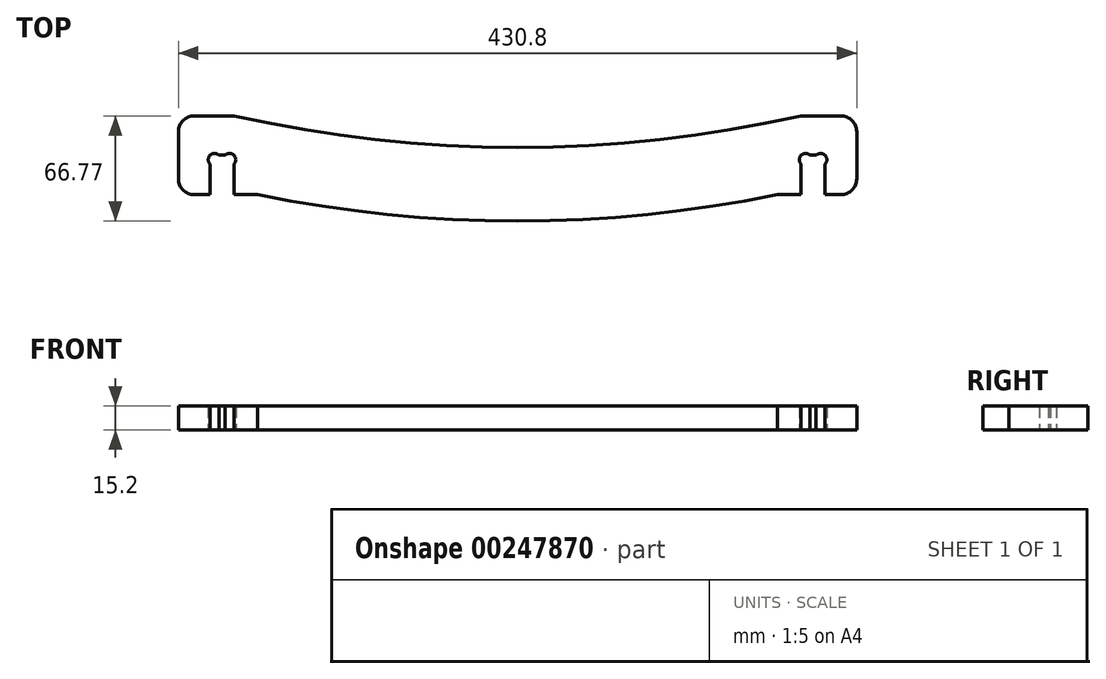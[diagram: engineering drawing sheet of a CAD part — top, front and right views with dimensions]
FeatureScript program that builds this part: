
annotation { "Feature Type Name" : "Feature", "Feature Type Description" : "" }
export const myFeature = defineFeature(function(context is Context, id is Id, definition is map)
    precondition{}
    {
        {
            var Q0;
            Q0=qCreatedBy(makeId("Top.planeOp"),FACE);
            var sketch = newSketch(context, id + "F0", { "sketchPlane" : qUnion([Q0])});
            skLineSegment(sketch, "E0", {"start": v(-2580, 2029) * mm, "end": v(-1360, 2029) * mm});
            skLineSegment(sketch, "E1", {"start": v(-1360, 2029) * mm, "end": v(-1360, -411) * mm});
            skLineSegment(sketch, "E2", {"start": v(-1360, -411) * mm, "end": v(-2580, -411) * mm});
            skLineSegment(sketch, "E3", {"start": v(-2580, -411) * mm, "end": v(-2580, 2029) * mm});
            skLineSegment(sketch, "E4", {"start": v(-2560, 2009) * mm, "end": v(-1380, 2009) * mm});
            skLineSegment(sketch, "E5", {"start": v(-1380, 2009) * mm, "end": v(-1380, -391) * mm});
            skLineSegment(sketch, "E6", {"start": v(-1380, -391) * mm, "end": v(-2560, -391) * mm});
            skLineSegment(sketch, "E7", {"start": v(-2560, -391) * mm, "end": v(-2560, 2009) * mm});
            skLineSegment(sketch, "E8", {"start": v(-1720.35, -206.09) * mm, "end": v(-1725.36, -224.77) * mm});
            skArc(sketch, "E9", {"start": v(-1725.36, -224.77) * mm, "mid": v(-1726.83, -230.23) * mm, "end": v(-1732.29, -228.77) * mm});
            skLineSegment(sketch, "E10", {"start": v(-1732.29, -228.77) * mm, "end": v(-1736.04, -227.76) * mm});
            skArc(sketch, "E11", {"start": v(-1736.04, -227.76) * mm, "mid": v(-1741.5, -226.3) * mm, "end": v(-1740.04, -220.84) * mm});
            skLineSegment(sketch, "E12", {"start": v(-1740.04, -220.84) * mm, "end": v(-1735.04, -202.15) * mm});
            skLineSegment(sketch, "E13", {"start": v(-1735.04, -202.15) * mm, "end": v(-1754.16, -197.03) * mm});
            skLineSegment(sketch, "E14", {"start": v(-1754.16, -197.03) * mm, "end": v(-1759.17, -215.71) * mm});
            skArc(sketch, "E15", {"start": v(-1759.17, -215.71) * mm, "mid": v(-1760.63, -221.18) * mm, "end": v(-1766.1, -219.71) * mm});
            skLineSegment(sketch, "E16", {"start": v(-1766.1, -219.71) * mm, "end": v(-1769.85, -218.7) * mm});
            skArc(sketch, "E17", {"start": v(-1769.85, -218.7) * mm, "mid": v(-1775.31, -217.24) * mm, "end": v(-1773.85, -211.78) * mm});
            skLineSegment(sketch, "E18", {"start": v(-1773.85, -211.78) * mm, "end": v(-1768.84, -193.1) * mm});
            skLineSegment(sketch, "E19", {"start": v(-1768.84, -193.1) * mm, "end": v(-1787.97, -187.97) * mm});
            skLineSegment(sketch, "E20", {"start": v(-1787.97, -187.97) * mm, "end": v(-1792.98, -206.65) * mm});
            skArc(sketch, "E21", {"start": v(-1792.98, -206.65) * mm, "mid": v(-1794.44, -212.12) * mm, "end": v(-1799.9, -210.65) * mm});
            skLineSegment(sketch, "E22", {"start": v(-1799.9, -210.65) * mm, "end": v(-1803.66, -209.65) * mm});
            skArc(sketch, "E23", {"start": v(-1803.66, -209.65) * mm, "mid": v(-1809.12, -208.18) * mm, "end": v(-1807.66, -202.72) * mm});
            skLineSegment(sketch, "E24", {"start": v(-1807.66, -202.72) * mm, "end": v(-1802.65, -184.03) * mm});
            skLineSegment(sketch, "E25", {"start": v(-1802.65, -184.03) * mm, "end": v(-1821.78, -178.9) * mm});
            skLineSegment(sketch, "E26", {"start": v(-1821.78, -178.9) * mm, "end": v(-1826.78, -197.6) * mm});
            skArc(sketch, "E27", {"start": v(-1826.78, -197.6) * mm, "mid": v(-1828.25, -203.06) * mm, "end": v(-1833.71, -201.6) * mm});
            skLineSegment(sketch, "E28", {"start": v(-1833.71, -201.6) * mm, "end": v(-1837.47, -200.59) * mm});
            skArc(sketch, "E29", {"start": v(-1837.47, -200.59) * mm, "mid": v(-1842.93, -199.12) * mm, "end": v(-1841.47, -193.66) * mm});
            skLineSegment(sketch, "E30", {"start": v(-1841.47, -193.66) * mm, "end": v(-1836.46, -174.98) * mm});
            skLineSegment(sketch, "E31", {"start": v(-1836.46, -174.98) * mm, "end": v(-1855.58, -169.85) * mm});
            skLineSegment(sketch, "E32", {"start": v(-1855.58, -169.85) * mm, "end": v(-1860.6, -188.54) * mm});
            skArc(sketch, "E33", {"start": v(-1860.6, -188.54) * mm, "mid": v(-1862.05, -194) * mm, "end": v(-1867.52, -192.53) * mm});
            skLineSegment(sketch, "E34", {"start": v(-1867.52, -192.54) * mm, "end": v(-1871.27, -191.53) * mm});
            skArc(sketch, "E35", {"start": v(-1871.27, -191.53) * mm, "mid": v(-1876.74, -190.07) * mm, "end": v(-1875.27, -184.6) * mm});
            skLineSegment(sketch, "E36", {"start": v(-1875.27, -184.6) * mm, "end": v(-1870.27, -165.92) * mm});
            skLineSegment(sketch, "E37", {"start": v(-1870.27, -165.92) * mm, "end": v(-1891.6, -160.2) * mm});
            skArc(sketch, "E38", {"start": v(-1891.6, -160.2) * mm, "mid": v(-1902.18, -158.55) * mm, "end": v(-1912.87, -159.2) * mm});
            skLineSegment(sketch, "E39", {"start": v(-1912.87, -159.2) * mm, "end": v(-2017.76, -176.28) * mm});
            skArc(sketch, "E40", {"start": v(-2017.76, -176.28) * mm, "mid": v(-2042.3, -169.28) * mm, "end": v(-2052.57, -145.92) * mm});
            skLineSegment(sketch, "E41", {"start": v(-2052.57, -145.92) * mm, "end": v(-2051.8, -115.24) * mm});
            skLineSegment(sketch, "E42", {"start": v(-2051.8, -115.24) * mm, "end": v(-2071.14, -114.76) * mm});
            skArc(sketch, "E43", {"start": v(-2071.14, -114.76) * mm, "mid": v(-2076.8, -114.62) * mm, "end": v(-2076.66, -108.97) * mm});
            skLineSegment(sketch, "E44", {"start": v(-2076.66, -108.97) * mm, "end": v(-2076.56, -105.08) * mm});
            skArc(sketch, "E45", {"start": v(-2076.56, -105.08) * mm, "mid": v(-2076.42, -99.43) * mm, "end": v(-2070.77, -99.57) * mm});
            skLineSegment(sketch, "E46", {"start": v(-2070.77, -99.57) * mm, "end": v(-2051.43, -100.05) * mm});
            skLineSegment(sketch, "E47", {"start": v(-2051.43, -100.05) * mm, "end": v(-2050.93, -80.25) * mm});
            skLineSegment(sketch, "E48", {"start": v(-2050.93, -80.25) * mm, "end": v(-2070.27, -79.77) * mm});
            skArc(sketch, "E49", {"start": v(-2070.27, -79.77) * mm, "mid": v(-2075.93, -79.63) * mm, "end": v(-2075.79, -73.98) * mm});
            skLineSegment(sketch, "E50", {"start": v(-2075.79, -73.98) * mm, "end": v(-2075.69, -70.1) * mm});
            skArc(sketch, "E51", {"start": v(-2075.69, -70.1) * mm, "mid": v(-2075.55, -64.44) * mm, "end": v(-2069.9, -64.58) * mm});
            skLineSegment(sketch, "E52", {"start": v(-2069.9, -64.58) * mm, "end": v(-2050.56, -65.06) * mm});
            skLineSegment(sketch, "E53", {"start": v(-2050.56, -65.06) * mm, "end": v(-2050.06, -45.27) * mm});
            skLineSegment(sketch, "E54", {"start": v(-2050.06, -45.27) * mm, "end": v(-2069.4, -44.78) * mm});
            skArc(sketch, "E55", {"start": v(-2069.4, -44.78) * mm, "mid": v(-2075.05, -44.64) * mm, "end": v(-2074.91, -38.99) * mm});
            skLineSegment(sketch, "E56", {"start": v(-2074.91, -38.99) * mm, "end": v(-2074.82, -35.1) * mm});
            skArc(sketch, "E57", {"start": v(-2074.82, -35.1) * mm, "mid": v(-2074.68, -29.45) * mm, "end": v(-2069.02, -29.59) * mm});
            skLineSegment(sketch, "E58", {"start": v(-2069.02, -29.59) * mm, "end": v(-2049.68, -30.07) * mm});
            skLineSegment(sketch, "E59", {"start": v(-2049.68, -30.07) * mm, "end": v(-2049.2, -10.28) * mm});
            skLineSegment(sketch, "E60", {"start": v(-2049.2, -10.28) * mm, "end": v(-2068.53, -9.8) * mm});
            skArc(sketch, "E61", {"start": v(-2068.53, -9.8) * mm, "mid": v(-2074.18, -9.65) * mm, "end": v(-2074.04, -4) * mm});
            skLineSegment(sketch, "E62", {"start": v(-2074.04, -4) * mm, "end": v(-2073.94, -0.11) * mm});
            skArc(sketch, "E63", {"start": v(-2073.94, -0.11) * mm, "mid": v(-2073.8, 5.54) * mm, "end": v(-2068.15, 5.4) * mm});
            skLineSegment(sketch, "E64", {"start": v(-2068.15, 5.4) * mm, "end": v(-2048.81, 4.92) * mm});
            skLineSegment(sketch, "E65", {"start": v(-2048.81, 4.92) * mm, "end": v(-2048.32, 24.71) * mm});
            skLineSegment(sketch, "E66", {"start": v(-2048.32, 24.71) * mm, "end": v(-2067.66, 25.2) * mm});
            skArc(sketch, "E67", {"start": v(-2067.66, 25.2) * mm, "mid": v(-2073.31, 25.34) * mm, "end": v(-2073.17, 31) * mm});
            skLineSegment(sketch, "E68", {"start": v(-2073.17, 31) * mm, "end": v(-2073.07, 34.88) * mm});
            skArc(sketch, "E69", {"start": v(-2073.07, 34.88) * mm, "mid": v(-2072.93, 40.53) * mm, "end": v(-2067.28, 40.4) * mm});
            skLineSegment(sketch, "E70", {"start": v(-2067.28, 40.4) * mm, "end": v(-2047.94, 39.9) * mm});
            skLineSegment(sketch, "E71", {"start": v(-2047.94, 39.9) * mm, "end": v(-2047.45, 59.7) * mm});
            skLineSegment(sketch, "E72", {"start": v(-2047.45, 59.7) * mm, "end": v(-2066.78, 60.18) * mm});
            skArc(sketch, "E73", {"start": v(-2066.78, 60.18) * mm, "mid": v(-2072.44, 60.33) * mm, "end": v(-2072.3, 65.98) * mm});
            skLineSegment(sketch, "E74", {"start": v(-2072.3, 65.98) * mm, "end": v(-2072.2, 69.87) * mm});
            skArc(sketch, "E75", {"start": v(-2072.2, 69.87) * mm, "mid": v(-2072.06, 75.52) * mm, "end": v(-2066.4, 75.38) * mm});
            skLineSegment(sketch, "E76", {"start": v(-2066.4, 75.38) * mm, "end": v(-2047.07, 74.9) * mm});
            skLineSegment(sketch, "E77", {"start": v(-2047.07, 74.9) * mm, "end": v(-2046.57, 94.7) * mm});
            skLineSegment(sketch, "E78", {"start": v(-2046.57, 94.7) * mm, "end": v(-2065.91, 95.17) * mm});
            skArc(sketch, "E79", {"start": v(-2065.91, 95.17) * mm, "mid": v(-2071.57, 95.31) * mm, "end": v(-2071.42, 100.97) * mm});
            skLineSegment(sketch, "E80", {"start": v(-2071.42, 100.97) * mm, "end": v(-2071.33, 104.85) * mm});
            skArc(sketch, "E81", {"start": v(-2071.33, 104.85) * mm, "mid": v(-2071.19, 110.5) * mm, "end": v(-2065.53, 110.37) * mm});
            skLineSegment(sketch, "E82", {"start": v(-2065.53, 110.37) * mm, "end": v(-2046.2, 109.89) * mm});
            skLineSegment(sketch, "E83", {"start": v(-2046.2, 109.89) * mm, "end": v(-2045.7, 129.68) * mm});
            skLineSegment(sketch, "E84", {"start": v(-2045.7, 129.68) * mm, "end": v(-2065.04, 130.16) * mm});
            skArc(sketch, "E85", {"start": v(-2065.04, 130.16) * mm, "mid": v(-2070.7, 130.3) * mm, "end": v(-2070.55, 135.96) * mm});
            skLineSegment(sketch, "E86", {"start": v(-2070.55, 135.96) * mm, "end": v(-2070.46, 139.84) * mm});
            skArc(sketch, "E87", {"start": v(-2070.46, 139.84) * mm, "mid": v(-2070.31, 145.5) * mm, "end": v(-2064.66, 145.36) * mm});
            skLineSegment(sketch, "E88", {"start": v(-2064.66, 145.36) * mm, "end": v(-2045.32, 144.88) * mm});
            skLineSegment(sketch, "E89", {"start": v(-2045.32, 144.88) * mm, "end": v(-2044.83, 164.67) * mm});
            skLineSegment(sketch, "E90", {"start": v(-2044.83, 164.67) * mm, "end": v(-2064.17, 165.15) * mm});
            skArc(sketch, "E91", {"start": v(-2064.17, 165.15) * mm, "mid": v(-2069.82, 165.3) * mm, "end": v(-2069.68, 170.95) * mm});
            skLineSegment(sketch, "E92", {"start": v(-2069.68, 170.95) * mm, "end": v(-2069.58, 174.83) * mm});
            skArc(sketch, "E93", {"start": v(-2069.58, 174.83) * mm, "mid": v(-2069.44, 180.49) * mm, "end": v(-2063.79, 180.35) * mm});
            skLineSegment(sketch, "E94", {"start": v(-2063.79, 180.35) * mm, "end": v(-2044.45, 179.86) * mm});
            skLineSegment(sketch, "E95", {"start": v(-2044.45, 179.86) * mm, "end": v(-2043.96, 199.66) * mm});
            skLineSegment(sketch, "E96", {"start": v(-2043.96, 199.66) * mm, "end": v(-2063.3, 200.14) * mm});
            skArc(sketch, "E97", {"start": v(-2063.3, 200.14) * mm, "mid": v(-2068.95, 200.28) * mm, "end": v(-2068.8, 205.94) * mm});
            skLineSegment(sketch, "E98", {"start": v(-2068.8, 205.94) * mm, "end": v(-2068.71, 209.82) * mm});
            skArc(sketch, "E99", {"start": v(-2068.71, 209.82) * mm, "mid": v(-2068.57, 215.48) * mm, "end": v(-2062.92, 215.34) * mm});
            skLineSegment(sketch, "E100", {"start": v(-2062.92, 215.34) * mm, "end": v(-2043.58, 214.85) * mm});
            skLineSegment(sketch, "E101", {"start": v(-2043.58, 214.85) * mm, "end": v(-2043.09, 234.63) * mm});
            skLineSegment(sketch, "E102", {"start": v(-2043.09, 234.63) * mm, "end": v(-2267.72, 254.88) * mm});
            skArc(sketch, "E103", {"start": v(-2267.72, 254.88) * mm, "mid": v(-2273.35, 255.39) * mm, "end": v(-2272.84, 261.02) * mm});
            skLineSegment(sketch, "E104", {"start": v(-2272.84, 261.02) * mm, "end": v(-2272.5, 264.9) * mm});
            skArc(sketch, "E105", {"start": v(-2272.5, 264.9) * mm, "mid": v(-2271.99, 270.53) * mm, "end": v(-2266.35, 270.02) * mm});
            skLineSegment(sketch, "E106", {"start": v(-2266.35, 270.02) * mm, "end": v(-2042.7, 249.86) * mm});
            skLineSegment(sketch, "E107", {"start": v(-2042.7, 249.86) * mm, "end": v(-2042.7, 249.96) * mm});
            skArc(sketch, "E108", {"start": v(-2042.7, 249.96) * mm, "mid": v(-2050.38, 270.53) * mm, "end": v(-2070, 280.37) * mm});
            skLineSegment(sketch, "E109", {"start": v(-2070, 280.37) * mm, "end": v(-2502.63, 319.37) * mm});
            skLineSegment(sketch, "E110", {"start": v(-2502.63, 319.37) * mm, "end": v(-2502.63, 256.1) * mm});
            skLineSegment(sketch, "E111", {"start": v(-2502.63, 256.1) * mm, "end": v(-2121.48, 221.73) * mm});
            skArc(sketch, "E112", {"start": v(-2121.48, 221.73) * mm, "mid": v(-2101.78, 211.82) * mm, "end": v(-2094.19, 191.1) * mm});
            skLineSegment(sketch, "E113", {"start": v(-2094.19, 191.1) * mm, "end": v(-2102.69, -150) * mm});
            skArc(sketch, "E114", {"start": v(-2102.69, -150) * mm, "mid": v(-2108.54, -167.07) * mm, "end": v(-2123.12, -177.7) * mm});
            skLineSegment(sketch, "E115", {"start": v(-2123.12, -177.7) * mm, "end": v(-2502.63, -299.61) * mm});
            skLineSegment(sketch, "E116", {"start": v(-2502.63, -299.61) * mm, "end": v(-2502.63, -349.61) * mm});
            skLineSegment(sketch, "E117", {"start": v(-2502.63, -349.61) * mm, "end": v(-2352.73, -314.3) * mm});
            skLineSegment(sketch, "E118", {"start": v(-2352.73, -314.3) * mm, "end": v(-2357.16, -295.47) * mm});
            skArc(sketch, "E119", {"start": v(-2357.16, -295.47) * mm, "mid": v(-2358.46, -289.97) * mm, "end": v(-2352.95, -288.67) * mm});
            skLineSegment(sketch, "E120", {"start": v(-2352.95, -288.67) * mm, "end": v(-2349.17, -287.78) * mm});
            skArc(sketch, "E121", {"start": v(-2349.17, -287.78) * mm, "mid": v(-2343.66, -286.48) * mm, "end": v(-2342.37, -291.99) * mm});
            skLineSegment(sketch, "E122", {"start": v(-2342.37, -291.99) * mm, "end": v(-2337.93, -310.81) * mm});
            skLineSegment(sketch, "E123", {"start": v(-2337.93, -310.81) * mm, "end": v(-1916.35, -211.5) * mm});
            skArc(sketch, "E124", {"start": v(-1916.35, -211.5) * mm, "mid": v(-1904.12, -210.17) * mm, "end": v(-1891.94, -211.87) * mm});
            skLineSegment(sketch, "E125", {"start": v(-1891.94, -211.87) * mm, "end": v(-1685.1, -267.3) * mm});
            skArc(sketch, "E126", {"start": v(-1685.1, -267.3) * mm, "mid": v(-1677.5, -266.3) * mm, "end": v(-1672.85, -260.23) * mm});
            skLineSegment(sketch, "E127", {"start": v(-1672.85, -260.23) * mm, "end": v(-1665.08, -231.25) * mm});
            skArc(sketch, "E128", {"start": v(-1665.08, -231.25) * mm, "mid": v(-1666.08, -223.66) * mm, "end": v(-1672.16, -219) * mm});
            skLineSegment(sketch, "E129", {"start": v(-1672.16, -219) * mm, "end": v(-1686.55, -215.14) * mm});
            skLineSegment(sketch, "E130", {"start": v(-1686.55, -215.14) * mm, "end": v(-1691.55, -233.83) * mm});
            skArc(sketch, "E131", {"start": v(-1691.55, -233.83) * mm, "mid": v(-1693.02, -239.3) * mm, "end": v(-1698.48, -237.83) * mm});
            skLineSegment(sketch, "E132", {"start": v(-1698.48, -237.83) * mm, "end": v(-1702.24, -236.82) * mm});
            skArc(sketch, "E133", {"start": v(-1702.24, -236.82) * mm, "mid": v(-1707.7, -235.36) * mm, "end": v(-1706.24, -229.9) * mm});
            skLineSegment(sketch, "E134", {"start": v(-1706.24, -229.9) * mm, "end": v(-1701.23, -211.21) * mm});
            skLineSegment(sketch, "E135", {"start": v(-1701.23, -211.21) * mm, "end": v(-1720.26, -206.11) * mm});
            skArc(sketch, "E136", {"start": v(-1681.43, -338.92) * mm, "mid": v(-1675.77, -338.92) * mm, "end": v(-1675.77, -344.58) * mm});
            skLineSegment(sketch, "E137", {"start": v(-1675.77, -344.58) * mm, "end": v(-1675.77, -348.47) * mm});
            skArc(sketch, "E138", {"start": v(-1675.77, -348.47) * mm, "mid": v(-1675.77, -354.12) * mm, "end": v(-1681.43, -354.12) * mm});
            skLineSegment(sketch, "E139", {"start": v(-1681.43, -354.12) * mm, "end": v(-1905.99, -354.12) * mm});
            skLineSegment(sketch, "E140", {"start": v(-1905.99, -354.12) * mm, "end": v(-1905.99, -374.22) * mm});
            skLineSegment(sketch, "E141", {"start": v(-1905.99, -374.22) * mm, "end": v(-1455.55, -374.22) * mm});
            skArc(sketch, "E142", {"start": v(-1455.55, -374.22) * mm, "mid": v(-1448.48, -371.3) * mm, "end": v(-1445.55, -364.22) * mm});
            skLineSegment(sketch, "E143", {"start": v(-1445.55, -364.22) * mm, "end": v(-1445.55, -338.79) * mm});
            skArc(sketch, "E144", {"start": v(-1445.55, -338.79) * mm, "mid": v(-1465.55, -158.82) * mm, "end": v(-1445.55, 21.14) * mm});
            skLineSegment(sketch, "E145", {"start": v(-1445.55, 21.14) * mm, "end": v(-1445.55, 46.58) * mm});
            skArc(sketch, "E146", {"start": v(-1445.55, 46.58) * mm, "mid": v(-1448.48, 53.65) * mm, "end": v(-1455.55, 56.58) * mm});
            skLineSegment(sketch, "E147", {"start": v(-1455.55, 56.58) * mm, "end": v(-1905.99, 56.58) * mm});
            skLineSegment(sketch, "E148", {"start": v(-1905.99, 56.58) * mm, "end": v(-1905.99, 36.48) * mm});
            skLineSegment(sketch, "E149", {"start": v(-1905.99, 36.48) * mm, "end": v(-1681.43, 36.48) * mm});
            skArc(sketch, "E150", {"start": v(-1681.43, 36.48) * mm, "mid": v(-1675.77, 36.48) * mm, "end": v(-1675.77, 30.82) * mm});
            skLineSegment(sketch, "E151", {"start": v(-1675.77, 30.82) * mm, "end": v(-1675.77, 26.93) * mm});
            skArc(sketch, "E152", {"start": v(-1675.77, 26.93) * mm, "mid": v(-1675.77, 21.28) * mm, "end": v(-1681.43, 21.28) * mm});
            skLineSegment(sketch, "E153", {"start": v(-1681.43, 21.28) * mm, "end": v(-1905.99, 21.28) * mm});
            skLineSegment(sketch, "E154", {"start": v(-1905.99, 21.28) * mm, "end": v(-1905.99, 1.18) * mm});
            skLineSegment(sketch, "E155", {"start": v(-1905.99, 1.18) * mm, "end": v(-1508.65, 1.18) * mm});
            skArc(sketch, "E156", {"start": v(-1508.65, 1.18) * mm, "mid": v(-1500.97, -2.42) * mm, "end": v(-1498.82, -10.63) * mm});
            skArc(sketch, "E157", {"start": v(-1498.82, -10.63) * mm, "mid": v(-1512.32, -158.82) * mm, "end": v(-1498.82, -307.01) * mm});
            skArc(sketch, "E158", {"start": v(-1498.82, -307.01) * mm, "mid": v(-1500.97, -315.22) * mm, "end": v(-1508.65, -318.82) * mm});
            skLineSegment(sketch, "E159", {"start": v(-1508.65, -318.82) * mm, "end": v(-1905.99, -318.82) * mm});
            skLineSegment(sketch, "E160", {"start": v(-1905.99, -318.82) * mm, "end": v(-1905.99, -338.92) * mm});
            skLineSegment(sketch, "E161", {"start": v(-1905.99, -338.92) * mm, "end": v(-1681.43, -338.92) * mm});
            skArc(sketch, "E162", {"start": v(-1935.54, -36.1) * mm, "mid": v(-1929.88, -36.1) * mm, "end": v(-1929.88, -41.77) * mm});
            skLineSegment(sketch, "E163", {"start": v(-1929.88, -41.77) * mm, "end": v(-1929.88, -61.1) * mm});
            skLineSegment(sketch, "E164", {"start": v(-1929.88, -61.1) * mm, "end": v(-1554.68, -61.1) * mm});
            skLineSegment(sketch, "E165", {"start": v(-1554.68, -61.1) * mm, "end": v(-1554.68, -41.77) * mm});
            skArc(sketch, "E166", {"start": v(-1554.68, -41.77) * mm, "mid": v(-1554.68, -36.1) * mm, "end": v(-1549.03, -36.1) * mm});
            skLineSegment(sketch, "E167", {"start": v(-1549.03, -36.1) * mm, "end": v(-1545.14, -36.1) * mm});
            skArc(sketch, "E168", {"start": v(-1545.14, -36.1) * mm, "mid": v(-1539.48, -36.1) * mm, "end": v(-1539.48, -41.77) * mm});
            skLineSegment(sketch, "E169", {"start": v(-1539.48, -41.77) * mm, "end": v(-1539.48, -61.1) * mm});
            skLineSegment(sketch, "E170", {"start": v(-1539.48, -61.1) * mm, "end": v(-1534.78, -61.1) * mm});
            skArc(sketch, "E171", {"start": v(-1534.78, -61.1) * mm, "mid": v(-1527.71, -58.18) * mm, "end": v(-1524.78, -51.1) * mm});
            skLineSegment(sketch, "E172", {"start": v(-1524.78, -51.1) * mm, "end": v(-1524.78, -21.1) * mm});
            skArc(sketch, "E173", {"start": v(-1524.78, -21.1) * mm, "mid": v(-1527.71, -14.04) * mm, "end": v(-1534.78, -11.1) * mm});
            skLineSegment(sketch, "E174", {"start": v(-1534.78, -11.1) * mm, "end": v(-1949.78, -11.1) * mm});
            skArc(sketch, "E175", {"start": v(-1949.78, -11.1) * mm, "mid": v(-1956.85, -14.04) * mm, "end": v(-1959.78, -21.1) * mm});
            skLineSegment(sketch, "E176", {"start": v(-1959.78, -21.1) * mm, "end": v(-1959.78, -51.1) * mm});
            skArc(sketch, "E177", {"start": v(-1959.78, -51.1) * mm, "mid": v(-1956.85, -58.18) * mm, "end": v(-1949.78, -61.1) * mm});
            skLineSegment(sketch, "E178", {"start": v(-1949.78, -61.1) * mm, "end": v(-1945.08, -61.1) * mm});
            skLineSegment(sketch, "E179", {"start": v(-1945.08, -61.1) * mm, "end": v(-1945.08, -41.77) * mm});
            skArc(sketch, "E180", {"start": v(-1945.08, -41.77) * mm, "mid": v(-1945.08, -36.1) * mm, "end": v(-1939.43, -36.1) * mm});
            skLineSegment(sketch, "E181", {"start": v(-1939.43, -36.1) * mm, "end": v(-1935.54, -36.1) * mm});
            skArc(sketch, "E182", {"start": v(-2222.39, -382.07) * mm, "mid": v(-2052.48, -319.46) * mm, "end": v(-1872.97, -295.7) * mm});
            skLineSegment(sketch, "E183", {"start": v(-1872.97, -295.7) * mm, "end": v(-1848.28, -289.59) * mm});
            skArc(sketch, "E184", {"start": v(-1848.28, -289.59) * mm, "mid": v(-1842.12, -285.05) * mm, "end": v(-1840.98, -277.48) * mm});
            skLineSegment(sketch, "E185", {"start": v(-1840.98, -277.48) * mm, "end": v(-1848.17, -248.36) * mm});
            skArc(sketch, "E186", {"start": v(-1848.17, -248.36) * mm, "mid": v(-1852.71, -242.2) * mm, "end": v(-1860.28, -241.06) * mm});
            skLineSegment(sketch, "E187", {"start": v(-1860.28, -241.06) * mm, "end": v(-1870.08, -243.48) * mm});
            skLineSegment(sketch, "E188", {"start": v(-1870.08, -243.48) * mm, "end": v(-1865.44, -262.26) * mm});
            skArc(sketch, "E189", {"start": v(-1865.44, -262.26) * mm, "mid": v(-1864.09, -267.75) * mm, "end": v(-1869.58, -269.1) * mm});
            skLineSegment(sketch, "E190", {"start": v(-1869.58, -269.1) * mm, "end": v(-1873.35, -270.04) * mm});
            skArc(sketch, "E191", {"start": v(-1873.35, -270.04) * mm, "mid": v(-1878.84, -271.4) * mm, "end": v(-1880.2, -265.9) * mm});
            skLineSegment(sketch, "E192", {"start": v(-1880.2, -265.9) * mm, "end": v(-1884.84, -247.13) * mm});
            skLineSegment(sketch, "E193", {"start": v(-1884.84, -247.13) * mm, "end": v(-1899.5, -250.75) * mm});
            skArc(sketch, "E194", {"start": v(-1899.5, -250.75) * mm, "mid": v(-2063.7, -274.06) * mm, "end": v(-2219.86, -329.94) * mm});
            skLineSegment(sketch, "E195", {"start": v(-2219.86, -329.94) * mm, "end": v(-2234.52, -333.57) * mm});
            skLineSegment(sketch, "E196", {"start": v(-2234.52, -333.57) * mm, "end": v(-2229.87, -352.34) * mm});
            skArc(sketch, "E197", {"start": v(-2229.87, -352.34) * mm, "mid": v(-2228.52, -357.84) * mm, "end": v(-2234, -359.2) * mm});
            skLineSegment(sketch, "E198", {"start": v(-2234, -359.2) * mm, "end": v(-2237.78, -360.13) * mm});
            skArc(sketch, "E199", {"start": v(-2237.78, -360.13) * mm, "mid": v(-2243.27, -361.48) * mm, "end": v(-2244.63, -356) * mm});
            skLineSegment(sketch, "E200", {"start": v(-2244.63, -356) * mm, "end": v(-2249.27, -337.21) * mm});
            skLineSegment(sketch, "E201", {"start": v(-2249.27, -337.21) * mm, "end": v(-2259.08, -339.64) * mm});
            skArc(sketch, "E202", {"start": v(-2259.08, -339.64) * mm, "mid": v(-2265.24, -344.18) * mm, "end": v(-2266.38, -351.74) * mm});
            skLineSegment(sketch, "E203", {"start": v(-2266.38, -351.74) * mm, "end": v(-2259.19, -380.86) * mm});
            skArc(sketch, "E204", {"start": v(-2259.19, -380.86) * mm, "mid": v(-2254.65, -387.02) * mm, "end": v(-2247.08, -388.17) * mm});
            skLineSegment(sketch, "E205", {"start": v(-2247.08, -388.17) * mm, "end": v(-2222.39, -382.07) * mm});
            skArc(sketch, "E206", {"start": v(-1385, 120.69) * mm, "mid": v(-1405, 300.65) * mm, "end": v(-1385, 480.62) * mm});
            skLineSegment(sketch, "E207", {"start": v(-1385, 480.62) * mm, "end": v(-1385, 506.05) * mm});
            skArc(sketch, "E208", {"start": v(-1385, 506.05) * mm, "mid": v(-1387.93, 513.12) * mm, "end": v(-1395, 516.05) * mm});
            skLineSegment(sketch, "E209", {"start": v(-1395, 516.05) * mm, "end": v(-1425, 516.05) * mm});
            skArc(sketch, "E210", {"start": v(-1425, 516.05) * mm, "mid": v(-1432.06, 513.12) * mm, "end": v(-1435, 506.05) * mm});
            skLineSegment(sketch, "E211", {"start": v(-1435, 506.05) * mm, "end": v(-1435, 495.95) * mm});
            skLineSegment(sketch, "E212", {"start": v(-1435, 495.95) * mm, "end": v(-1415.65, 495.95) * mm});
            skArc(sketch, "E213", {"start": v(-1415.65, 495.95) * mm, "mid": v(-1410, 495.95) * mm, "end": v(-1410, 490.3) * mm});
            skLineSegment(sketch, "E214", {"start": v(-1410, 490.3) * mm, "end": v(-1410, 486.41) * mm});
            skArc(sketch, "E215", {"start": v(-1410, 486.41) * mm, "mid": v(-1410, 480.75) * mm, "end": v(-1415.65, 480.75) * mm});
            skLineSegment(sketch, "E216", {"start": v(-1415.65, 480.75) * mm, "end": v(-1435, 480.75) * mm});
            skLineSegment(sketch, "E217", {"start": v(-1435, 480.75) * mm, "end": v(-1435, 465.65) * mm});
            skArc(sketch, "E218", {"start": v(-1435, 465.65) * mm, "mid": v(-1451.77, 300.65) * mm, "end": v(-1435, 135.65) * mm});
            skLineSegment(sketch, "E219", {"start": v(-1435, 135.65) * mm, "end": v(-1435, 120.55) * mm});
            skLineSegment(sketch, "E220", {"start": v(-1435, 120.55) * mm, "end": v(-1415.65, 120.55) * mm});
            skArc(sketch, "E221", {"start": v(-1415.65, 120.55) * mm, "mid": v(-1410, 120.55) * mm, "end": v(-1410, 114.9) * mm});
            skLineSegment(sketch, "E222", {"start": v(-1410, 114.9) * mm, "end": v(-1410, 111.01) * mm});
            skArc(sketch, "E223", {"start": v(-1410, 111.01) * mm, "mid": v(-1410, 105.35) * mm, "end": v(-1415.65, 105.35) * mm});
            skLineSegment(sketch, "E224", {"start": v(-1415.65, 105.35) * mm, "end": v(-1435, 105.35) * mm});
            skLineSegment(sketch, "E225", {"start": v(-1435, 105.35) * mm, "end": v(-1435, 95.25) * mm});
            skArc(sketch, "E226", {"start": v(-1435, 95.25) * mm, "mid": v(-1432.06, 88.18) * mm, "end": v(-1425, 85.25) * mm});
            skLineSegment(sketch, "E227", {"start": v(-1425, 85.25) * mm, "end": v(-1395, 85.25) * mm});
            skArc(sketch, "E228", {"start": v(-1395, 85.25) * mm, "mid": v(-1387.93, 88.18) * mm, "end": v(-1385, 95.25) * mm});
            skLineSegment(sketch, "E229", {"start": v(-1385, 95.25) * mm, "end": v(-1385, 120.69) * mm});
            skArc(sketch, "E230", {"start": v(-2159.63, -49.76) * mm, "mid": v(-2339.6, -69.76) * mm, "end": v(-2519.57, -49.76) * mm});
            skLineSegment(sketch, "E231", {"start": v(-2519.57, -49.76) * mm, "end": v(-2545, -49.76) * mm});
            skArc(sketch, "E232", {"start": v(-2545, -49.76) * mm, "mid": v(-2552.07, -52.7) * mm, "end": v(-2555, -59.76) * mm});
            skLineSegment(sketch, "E233", {"start": v(-2555, -59.76) * mm, "end": v(-2555, -89.75) * mm});
            skArc(sketch, "E234", {"start": v(-2555, -89.75) * mm, "mid": v(-2552.07, -96.83) * mm, "end": v(-2545, -99.75) * mm});
            skLineSegment(sketch, "E235", {"start": v(-2545, -99.75) * mm, "end": v(-2534.9, -99.75) * mm});
            skLineSegment(sketch, "E236", {"start": v(-2534.9, -99.75) * mm, "end": v(-2534.9, -80.41) * mm});
            skArc(sketch, "E237", {"start": v(-2534.9, -80.41) * mm, "mid": v(-2534.9, -74.75) * mm, "end": v(-2529.24, -74.75) * mm});
            skLineSegment(sketch, "E238", {"start": v(-2529.24, -74.75) * mm, "end": v(-2525.36, -74.75) * mm});
            skArc(sketch, "E239", {"start": v(-2525.36, -74.75) * mm, "mid": v(-2519.7, -74.75) * mm, "end": v(-2519.7, -80.41) * mm});
            skLineSegment(sketch, "E240", {"start": v(-2519.7, -80.41) * mm, "end": v(-2519.7, -99.75) * mm});
            skLineSegment(sketch, "E241", {"start": v(-2519.7, -99.75) * mm, "end": v(-2504.6, -99.75) * mm});
            skArc(sketch, "E242", {"start": v(-2504.6, -99.75) * mm, "mid": v(-2339.6, -116.53) * mm, "end": v(-2174.6, -99.75) * mm});
            skLineSegment(sketch, "E243", {"start": v(-2174.6, -99.75) * mm, "end": v(-2159.5, -99.75) * mm});
            skLineSegment(sketch, "E244", {"start": v(-2159.5, -99.75) * mm, "end": v(-2159.5, -80.41) * mm});
            skArc(sketch, "E245", {"start": v(-2159.5, -80.41) * mm, "mid": v(-2159.5, -74.75) * mm, "end": v(-2153.84, -74.75) * mm});
            skLineSegment(sketch, "E246", {"start": v(-2153.84, -74.75) * mm, "end": v(-2149.96, -74.75) * mm});
            skArc(sketch, "E247", {"start": v(-2149.96, -74.75) * mm, "mid": v(-2144.3, -74.75) * mm, "end": v(-2144.3, -80.41) * mm});
            skLineSegment(sketch, "E248", {"start": v(-2144.3, -80.41) * mm, "end": v(-2144.3, -99.75) * mm});
            skLineSegment(sketch, "E249", {"start": v(-2144.3, -99.75) * mm, "end": v(-2134.2, -99.75) * mm});
            skArc(sketch, "E250", {"start": v(-2134.2, -99.75) * mm, "mid": v(-2127.13, -96.83) * mm, "end": v(-2124.2, -89.75) * mm});
            skLineSegment(sketch, "E251", {"start": v(-2124.2, -89.75) * mm, "end": v(-2124.2, -59.76) * mm});
            skArc(sketch, "E252", {"start": v(-2124.2, -59.76) * mm, "mid": v(-2127.13, -52.7) * mm, "end": v(-2134.2, -49.76) * mm});
            skLineSegment(sketch, "E253", {"start": v(-2134.2, -49.76) * mm, "end": v(-2159.63, -49.76) * mm});
            skArc(sketch, "E254", {"start": v(-2159.63, -115.3) * mm, "mid": v(-2339.6, -135.3) * mm, "end": v(-2519.57, -115.3) * mm});
            skLineSegment(sketch, "E255", {"start": v(-2519.57, -115.3) * mm, "end": v(-2545, -115.3) * mm});
            skArc(sketch, "E256", {"start": v(-2545, -115.3) * mm, "mid": v(-2552.07, -118.22) * mm, "end": v(-2555, -125.3) * mm});
            skLineSegment(sketch, "E257", {"start": v(-2555, -125.3) * mm, "end": v(-2555, -155.29) * mm});
            skArc(sketch, "E258", {"start": v(-2555, -155.29) * mm, "mid": v(-2552.07, -162.36) * mm, "end": v(-2545, -165.29) * mm});
            skLineSegment(sketch, "E259", {"start": v(-2545, -165.29) * mm, "end": v(-2534.9, -165.29) * mm});
            skLineSegment(sketch, "E260", {"start": v(-2534.9, -165.29) * mm, "end": v(-2534.9, -145.94) * mm});
            skArc(sketch, "E261", {"start": v(-2534.9, -145.94) * mm, "mid": v(-2534.9, -140.29) * mm, "end": v(-2529.24, -140.29) * mm});
            skLineSegment(sketch, "E262", {"start": v(-2529.24, -140.29) * mm, "end": v(-2525.36, -140.29) * mm});
            skArc(sketch, "E263", {"start": v(-2525.36, -140.29) * mm, "mid": v(-2519.7, -140.29) * mm, "end": v(-2519.7, -145.94) * mm});
            skLineSegment(sketch, "E264", {"start": v(-2519.7, -145.94) * mm, "end": v(-2519.7, -165.29) * mm});
            skLineSegment(sketch, "E265", {"start": v(-2519.7, -165.29) * mm, "end": v(-2504.6, -165.29) * mm});
            skArc(sketch, "E266", {"start": v(-2504.6, -165.29) * mm, "mid": v(-2339.6, -182.06) * mm, "end": v(-2174.6, -165.29) * mm});
            skLineSegment(sketch, "E267", {"start": v(-2174.6, -165.29) * mm, "end": v(-2159.5, -165.29) * mm});
            skLineSegment(sketch, "E268", {"start": v(-2159.5, -165.29) * mm, "end": v(-2159.5, -145.94) * mm});
            skArc(sketch, "E269", {"start": v(-2159.5, -145.94) * mm, "mid": v(-2159.5, -140.29) * mm, "end": v(-2153.84, -140.29) * mm});
            skLineSegment(sketch, "E270", {"start": v(-2153.84, -140.29) * mm, "end": v(-2149.96, -140.29) * mm});
            skArc(sketch, "E271", {"start": v(-2149.96, -140.29) * mm, "mid": v(-2144.3, -140.29) * mm, "end": v(-2144.3, -145.94) * mm});
            skLineSegment(sketch, "E272", {"start": v(-2144.3, -145.94) * mm, "end": v(-2144.3, -165.29) * mm});
            skLineSegment(sketch, "E273", {"start": v(-2144.3, -165.29) * mm, "end": v(-2134.2, -165.29) * mm});
            skArc(sketch, "E274", {"start": v(-2134.2, -165.29) * mm, "mid": v(-2127.13, -162.36) * mm, "end": v(-2124.2, -155.29) * mm});
            skLineSegment(sketch, "E275", {"start": v(-2124.2, -155.29) * mm, "end": v(-2124.2, -125.3) * mm});
            skArc(sketch, "E276", {"start": v(-2124.2, -125.3) * mm, "mid": v(-2127.13, -118.22) * mm, "end": v(-2134.2, -115.3) * mm});
            skLineSegment(sketch, "E277", {"start": v(-2134.2, -115.3) * mm, "end": v(-2159.63, -115.3) * mm});
            skArc(sketch, "E278", {"start": v(-1866.53, 72.65) * mm, "mid": v(-1686.56, 92.65) * mm, "end": v(-1506.6, 72.65) * mm});
            skLineSegment(sketch, "E279", {"start": v(-1506.6, 72.65) * mm, "end": v(-1481.16, 72.65) * mm});
            skArc(sketch, "E280", {"start": v(-1481.16, 72.65) * mm, "mid": v(-1474.09, 75.58) * mm, "end": v(-1471.16, 82.65) * mm});
            skLineSegment(sketch, "E281", {"start": v(-1471.16, 82.65) * mm, "end": v(-1471.16, 112.65) * mm});
            skArc(sketch, "E282", {"start": v(-1471.16, 112.65) * mm, "mid": v(-1474.09, 119.72) * mm, "end": v(-1481.16, 122.65) * mm});
            skLineSegment(sketch, "E283", {"start": v(-1481.16, 122.65) * mm, "end": v(-1491.26, 122.65) * mm});
            skLineSegment(sketch, "E284", {"start": v(-1491.26, 122.65) * mm, "end": v(-1491.26, 103.3) * mm});
            skArc(sketch, "E285", {"start": v(-1491.26, 103.3) * mm, "mid": v(-1491.26, 97.65) * mm, "end": v(-1496.92, 97.65) * mm});
            skLineSegment(sketch, "E286", {"start": v(-1496.92, 97.65) * mm, "end": v(-1500.8, 97.65) * mm});
            skArc(sketch, "E287", {"start": v(-1500.8, 97.65) * mm, "mid": v(-1506.46, 97.65) * mm, "end": v(-1506.46, 103.3) * mm});
            skLineSegment(sketch, "E288", {"start": v(-1506.46, 103.3) * mm, "end": v(-1506.46, 122.65) * mm});
            skLineSegment(sketch, "E289", {"start": v(-1506.46, 122.65) * mm, "end": v(-1521.56, 122.65) * mm});
            skArc(sketch, "E290", {"start": v(-1521.56, 122.65) * mm, "mid": v(-1686.56, 139.42) * mm, "end": v(-1851.56, 122.65) * mm});
            skLineSegment(sketch, "E291", {"start": v(-1851.56, 122.65) * mm, "end": v(-1866.66, 122.65) * mm});
            skLineSegment(sketch, "E292", {"start": v(-1866.66, 122.65) * mm, "end": v(-1866.66, 103.3) * mm});
            skArc(sketch, "E293", {"start": v(-1866.66, 103.3) * mm, "mid": v(-1866.66, 97.65) * mm, "end": v(-1872.32, 97.65) * mm});
            skLineSegment(sketch, "E294", {"start": v(-1872.32, 97.65) * mm, "end": v(-1876.2, 97.65) * mm});
            skArc(sketch, "E295", {"start": v(-1876.2, 97.65) * mm, "mid": v(-1881.86, 97.65) * mm, "end": v(-1881.86, 103.3) * mm});
            skLineSegment(sketch, "E296", {"start": v(-1881.86, 103.3) * mm, "end": v(-1881.86, 122.65) * mm});
            skLineSegment(sketch, "E297", {"start": v(-1881.86, 122.65) * mm, "end": v(-1891.96, 122.65) * mm});
            skArc(sketch, "E298", {"start": v(-1891.96, 122.65) * mm, "mid": v(-1899.03, 119.72) * mm, "end": v(-1901.96, 112.65) * mm});
            skLineSegment(sketch, "E299", {"start": v(-1901.96, 112.65) * mm, "end": v(-1901.96, 82.65) * mm});
            skArc(sketch, "E300", {"start": v(-1901.96, 82.65) * mm, "mid": v(-1899.03, 75.58) * mm, "end": v(-1891.96, 72.65) * mm});
            skLineSegment(sketch, "E301", {"start": v(-1891.96, 72.65) * mm, "end": v(-1866.53, 72.65) * mm});
            skArc(sketch, "E302", {"start": v(-1866.53, 138.19) * mm, "mid": v(-1686.56, 158.19) * mm, "end": v(-1506.6, 138.19) * mm});
            skLineSegment(sketch, "E303", {"start": v(-1506.6, 138.19) * mm, "end": v(-1481.16, 138.19) * mm});
            skArc(sketch, "E304", {"start": v(-1481.16, 138.19) * mm, "mid": v(-1474.09, 141.11) * mm, "end": v(-1471.16, 148.19) * mm});
            skLineSegment(sketch, "E305", {"start": v(-1471.16, 148.19) * mm, "end": v(-1471.16, 178.18) * mm});
            skArc(sketch, "E306", {"start": v(-1471.16, 178.18) * mm, "mid": v(-1474.09, 185.25) * mm, "end": v(-1481.16, 188.18) * mm});
            skLineSegment(sketch, "E307", {"start": v(-1481.16, 188.18) * mm, "end": v(-1491.26, 188.18) * mm});
            skLineSegment(sketch, "E308", {"start": v(-1491.26, 188.18) * mm, "end": v(-1491.26, 168.83) * mm});
            skArc(sketch, "E309", {"start": v(-1491.26, 168.83) * mm, "mid": v(-1491.26, 163.18) * mm, "end": v(-1496.92, 163.18) * mm});
            skLineSegment(sketch, "E310", {"start": v(-1496.92, 163.18) * mm, "end": v(-1500.8, 163.18) * mm});
            skArc(sketch, "E311", {"start": v(-1500.8, 163.18) * mm, "mid": v(-1506.46, 163.18) * mm, "end": v(-1506.46, 168.83) * mm});
            skLineSegment(sketch, "E312", {"start": v(-1506.46, 168.83) * mm, "end": v(-1506.46, 188.18) * mm});
            skLineSegment(sketch, "E313", {"start": v(-1506.46, 188.18) * mm, "end": v(-1521.56, 188.18) * mm});
            skArc(sketch, "E314", {"start": v(-1521.56, 188.18) * mm, "mid": v(-1686.56, 204.96) * mm, "end": v(-1851.56, 188.18) * mm});
            skLineSegment(sketch, "E315", {"start": v(-1851.56, 188.18) * mm, "end": v(-1866.66, 188.18) * mm});
            skLineSegment(sketch, "E316", {"start": v(-1866.66, 188.18) * mm, "end": v(-1866.66, 168.83) * mm});
            skArc(sketch, "E317", {"start": v(-1866.66, 168.83) * mm, "mid": v(-1866.66, 163.18) * mm, "end": v(-1872.32, 163.18) * mm});
            skLineSegment(sketch, "E318", {"start": v(-1872.32, 163.18) * mm, "end": v(-1876.2, 163.18) * mm});
            skArc(sketch, "E319", {"start": v(-1876.2, 163.18) * mm, "mid": v(-1881.86, 163.18) * mm, "end": v(-1881.86, 168.83) * mm});
            skLineSegment(sketch, "E320", {"start": v(-1881.86, 168.83) * mm, "end": v(-1881.86, 188.18) * mm});
            skLineSegment(sketch, "E321", {"start": v(-1881.86, 188.18) * mm, "end": v(-1891.96, 188.18) * mm});
            skArc(sketch, "E322", {"start": v(-1891.96, 188.18) * mm, "mid": v(-1899.03, 185.25) * mm, "end": v(-1901.96, 178.18) * mm});
            skLineSegment(sketch, "E323", {"start": v(-1901.96, 178.18) * mm, "end": v(-1901.96, 148.19) * mm});
            skArc(sketch, "E324", {"start": v(-1901.96, 148.19) * mm, "mid": v(-1899.03, 141.11) * mm, "end": v(-1891.96, 138.19) * mm});
            skLineSegment(sketch, "E325", {"start": v(-1891.96, 138.19) * mm, "end": v(-1866.53, 138.19) * mm});
            skLineSegment(sketch, "E326", {"start": v(-1683.67, 500.3) * mm, "end": v(-1658.98, 506.4) * mm});
            skArc(sketch, "E327", {"start": v(-1658.98, 506.4) * mm, "mid": v(-1652.82, 510.94) * mm, "end": v(-1651.67, 518.51) * mm});
            skLineSegment(sketch, "E328", {"start": v(-1651.67, 518.51) * mm, "end": v(-1658.87, 547.63) * mm});
            skArc(sketch, "E329", {"start": v(-1658.87, 547.63) * mm, "mid": v(-1663.41, 553.79) * mm, "end": v(-1670.98, 554.93) * mm});
            skLineSegment(sketch, "E330", {"start": v(-1670.98, 554.93) * mm, "end": v(-1680.78, 552.51) * mm});
            skLineSegment(sketch, "E331", {"start": v(-1680.78, 552.51) * mm, "end": v(-1676.14, 533.73) * mm});
            skArc(sketch, "E332", {"start": v(-1676.14, 533.73) * mm, "mid": v(-1674.78, 528.24) * mm, "end": v(-1680.27, 526.88) * mm});
            skLineSegment(sketch, "E333", {"start": v(-1680.27, 526.88) * mm, "end": v(-1684.05, 525.95) * mm});
            skArc(sketch, "E334", {"start": v(-1684.05, 525.95) * mm, "mid": v(-1689.54, 524.6) * mm, "end": v(-1690.9, 530.09) * mm});
            skLineSegment(sketch, "E335", {"start": v(-1690.9, 530.09) * mm, "end": v(-1695.54, 548.86) * mm});
            skLineSegment(sketch, "E336", {"start": v(-1695.54, 548.86) * mm, "end": v(-1710.2, 545.24) * mm});
            skArc(sketch, "E337", {"start": v(-1710.2, 545.24) * mm, "mid": v(-1874.4, 521.93) * mm, "end": v(-2030.55, 466.05) * mm});
            skLineSegment(sketch, "E338", {"start": v(-2030.55, 466.05) * mm, "end": v(-2045.21, 462.43) * mm});
            skLineSegment(sketch, "E339", {"start": v(-2045.21, 462.43) * mm, "end": v(-2040.57, 443.65) * mm});
            skArc(sketch, "E340", {"start": v(-2040.57, 443.65) * mm, "mid": v(-2039.21, 438.16) * mm, "end": v(-2044.7, 436.8) * mm});
            skLineSegment(sketch, "E341", {"start": v(-2044.7, 436.8) * mm, "end": v(-2048.48, 435.87) * mm});
            skArc(sketch, "E342", {"start": v(-2048.48, 435.87) * mm, "mid": v(-2053.97, 434.5) * mm, "end": v(-2055.33, 440) * mm});
            skLineSegment(sketch, "E343", {"start": v(-2055.33, 440) * mm, "end": v(-2059.97, 458.78) * mm});
            skLineSegment(sketch, "E344", {"start": v(-2059.97, 458.78) * mm, "end": v(-2069.77, 456.35) * mm});
            skArc(sketch, "E345", {"start": v(-2069.77, 456.35) * mm, "mid": v(-2075.94, 451.81) * mm, "end": v(-2077.08, 444.25) * mm});
            skLineSegment(sketch, "E346", {"start": v(-2077.08, 444.25) * mm, "end": v(-2069.88, 415.13) * mm});
            skArc(sketch, "E347", {"start": v(-2069.88, 415.13) * mm, "mid": v(-2065.34, 408.97) * mm, "end": v(-2057.78, 407.82) * mm});
            skLineSegment(sketch, "E348", {"start": v(-2057.78, 407.82) * mm, "end": v(-2033.09, 413.93) * mm});
            skArc(sketch, "E349", {"start": v(-2033.09, 413.93) * mm, "mid": v(-1863.18, 476.53) * mm, "end": v(-1683.67, 500.3) * mm});
            skLineSegment(sketch, "E350", {"start": v(-2135.13, 480.57) * mm, "end": v(-2109.7, 480.57) * mm});
            skArc(sketch, "E351", {"start": v(-2109.7, 480.57) * mm, "mid": v(-2102.63, 483.5) * mm, "end": v(-2099.7, 490.57) * mm});
            skLineSegment(sketch, "E352", {"start": v(-2099.7, 490.57) * mm, "end": v(-2099.7, 520.56) * mm});
            skArc(sketch, "E353", {"start": v(-2099.7, 520.56) * mm, "mid": v(-2102.63, 527.63) * mm, "end": v(-2109.7, 530.56) * mm});
            skLineSegment(sketch, "E354", {"start": v(-2109.7, 530.56) * mm, "end": v(-2119.8, 530.56) * mm});
            skLineSegment(sketch, "E355", {"start": v(-2119.8, 530.56) * mm, "end": v(-2119.8, 511.22) * mm});
            skArc(sketch, "E356", {"start": v(-2119.8, 511.22) * mm, "mid": v(-2119.8, 505.56) * mm, "end": v(-2125.45, 505.56) * mm});
            skLineSegment(sketch, "E357", {"start": v(-2125.45, 505.56) * mm, "end": v(-2129.34, 505.56) * mm});
            skArc(sketch, "E358", {"start": v(-2129.34, 505.56) * mm, "mid": v(-2135, 505.56) * mm, "end": v(-2135, 511.22) * mm});
            skLineSegment(sketch, "E359", {"start": v(-2135, 511.22) * mm, "end": v(-2135, 530.56) * mm});
            skLineSegment(sketch, "E360", {"start": v(-2135, 530.56) * mm, "end": v(-2150.1, 530.56) * mm});
            skArc(sketch, "E361", {"start": v(-2150.1, 530.56) * mm, "mid": v(-2315.1, 547.34) * mm, "end": v(-2480.1, 530.56) * mm});
            skLineSegment(sketch, "E362", {"start": v(-2480.1, 530.56) * mm, "end": v(-2495.2, 530.56) * mm});
            skLineSegment(sketch, "E363", {"start": v(-2495.2, 530.56) * mm, "end": v(-2495.2, 511.22) * mm});
            skArc(sketch, "E364", {"start": v(-2495.2, 511.22) * mm, "mid": v(-2495.2, 505.56) * mm, "end": v(-2500.85, 505.56) * mm});
            skLineSegment(sketch, "E365", {"start": v(-2500.85, 505.56) * mm, "end": v(-2504.74, 505.56) * mm});
            skArc(sketch, "E366", {"start": v(-2504.74, 505.56) * mm, "mid": v(-2510.4, 505.56) * mm, "end": v(-2510.4, 511.22) * mm});
            skLineSegment(sketch, "E367", {"start": v(-2510.4, 511.22) * mm, "end": v(-2510.4, 530.56) * mm});
            skLineSegment(sketch, "E368", {"start": v(-2510.4, 530.56) * mm, "end": v(-2520.5, 530.56) * mm});
            skArc(sketch, "E369", {"start": v(-2520.5, 530.56) * mm, "mid": v(-2527.57, 527.63) * mm, "end": v(-2530.5, 520.56) * mm});
            skLineSegment(sketch, "E370", {"start": v(-2530.5, 520.56) * mm, "end": v(-2530.5, 490.57) * mm});
            skArc(sketch, "E371", {"start": v(-2530.5, 490.57) * mm, "mid": v(-2527.57, 483.5) * mm, "end": v(-2520.5, 480.57) * mm});
            skLineSegment(sketch, "E372", {"start": v(-2520.5, 480.57) * mm, "end": v(-2495.06, 480.57) * mm});
            skArc(sketch, "E373", {"start": v(-2495.06, 480.57) * mm, "mid": v(-2315.1, 500.57) * mm, "end": v(-2135.13, 480.57) * mm});
            skLineSegment(sketch, "E374", {"start": v(-2135.13, 415.03) * mm, "end": v(-2109.7, 415.03) * mm});
            skArc(sketch, "E375", {"start": v(-2109.7, 415.03) * mm, "mid": v(-2102.63, 417.96) * mm, "end": v(-2099.7, 425.03) * mm});
            skLineSegment(sketch, "E376", {"start": v(-2099.7, 425.03) * mm, "end": v(-2099.7, 455.03) * mm});
            skArc(sketch, "E377", {"start": v(-2099.7, 455.03) * mm, "mid": v(-2102.63, 462.1) * mm, "end": v(-2109.7, 465.03) * mm});
            skLineSegment(sketch, "E378", {"start": v(-2109.7, 465.03) * mm, "end": v(-2119.8, 465.03) * mm});
            skLineSegment(sketch, "E379", {"start": v(-2119.8, 465.03) * mm, "end": v(-2119.8, 445.68) * mm});
            skArc(sketch, "E380", {"start": v(-2119.8, 445.68) * mm, "mid": v(-2119.8, 440.03) * mm, "end": v(-2125.45, 440.03) * mm});
            skLineSegment(sketch, "E381", {"start": v(-2125.45, 440.03) * mm, "end": v(-2129.34, 440.03) * mm});
            skArc(sketch, "E382", {"start": v(-2129.34, 440.03) * mm, "mid": v(-2135, 440.03) * mm, "end": v(-2135, 445.68) * mm});
            skLineSegment(sketch, "E383", {"start": v(-2135, 445.68) * mm, "end": v(-2135, 465.03) * mm});
            skLineSegment(sketch, "E384", {"start": v(-2135, 465.03) * mm, "end": v(-2150.1, 465.03) * mm});
            skArc(sketch, "E385", {"start": v(-2150.1, 465.03) * mm, "mid": v(-2315.1, 481.8) * mm, "end": v(-2480.1, 465.03) * mm});
            skLineSegment(sketch, "E386", {"start": v(-2480.1, 465.03) * mm, "end": v(-2495.2, 465.03) * mm});
            skLineSegment(sketch, "E387", {"start": v(-2495.2, 465.03) * mm, "end": v(-2495.2, 445.68) * mm});
            skArc(sketch, "E388", {"start": v(-2495.2, 445.68) * mm, "mid": v(-2495.2, 440.03) * mm, "end": v(-2500.85, 440.03) * mm});
            skLineSegment(sketch, "E389", {"start": v(-2500.85, 440.03) * mm, "end": v(-2504.74, 440.03) * mm});
            skArc(sketch, "E390", {"start": v(-2504.74, 440.03) * mm, "mid": v(-2510.4, 440.03) * mm, "end": v(-2510.4, 445.68) * mm});
            skLineSegment(sketch, "E391", {"start": v(-2510.4, 445.68) * mm, "end": v(-2510.4, 465.03) * mm});
            skLineSegment(sketch, "E392", {"start": v(-2510.4, 465.03) * mm, "end": v(-2520.5, 465.03) * mm});
            skArc(sketch, "E393", {"start": v(-2520.5, 465.03) * mm, "mid": v(-2527.57, 462.1) * mm, "end": v(-2530.5, 455.03) * mm});
            skLineSegment(sketch, "E394", {"start": v(-2530.5, 455.03) * mm, "end": v(-2530.5, 425.03) * mm});
            skArc(sketch, "E395", {"start": v(-2530.5, 425.03) * mm, "mid": v(-2527.57, 417.96) * mm, "end": v(-2520.5, 415.03) * mm});
            skLineSegment(sketch, "E396", {"start": v(-2520.5, 415.03) * mm, "end": v(-2495.06, 415.03) * mm});
            skArc(sketch, "E397", {"start": v(-2495.06, 415.03) * mm, "mid": v(-2315.1, 435.03) * mm, "end": v(-2135.13, 415.03) * mm});
            skArc(sketch, "E398", {"start": v(-1866.53, 269.25) * mm, "mid": v(-1686.56, 289.25) * mm, "end": v(-1506.6, 269.25) * mm});
            skLineSegment(sketch, "E399", {"start": v(-1506.6, 269.25) * mm, "end": v(-1481.16, 269.25) * mm});
            skArc(sketch, "E400", {"start": v(-1481.16, 269.25) * mm, "mid": v(-1474.09, 272.18) * mm, "end": v(-1471.16, 279.25) * mm});
            skLineSegment(sketch, "E401", {"start": v(-1471.16, 279.25) * mm, "end": v(-1471.16, 309.24) * mm});
            skArc(sketch, "E402", {"start": v(-1471.16, 309.24) * mm, "mid": v(-1474.09, 316.31) * mm, "end": v(-1481.16, 319.24) * mm});
            skLineSegment(sketch, "E403", {"start": v(-1481.16, 319.24) * mm, "end": v(-1491.26, 319.24) * mm});
            skLineSegment(sketch, "E404", {"start": v(-1491.26, 319.24) * mm, "end": v(-1491.26, 299.9) * mm});
            skArc(sketch, "E405", {"start": v(-1491.26, 299.9) * mm, "mid": v(-1491.26, 294.24) * mm, "end": v(-1496.92, 294.24) * mm});
            skLineSegment(sketch, "E406", {"start": v(-1496.92, 294.24) * mm, "end": v(-1500.8, 294.24) * mm});
            skArc(sketch, "E407", {"start": v(-1500.8, 294.24) * mm, "mid": v(-1506.46, 294.24) * mm, "end": v(-1506.46, 299.9) * mm});
            skLineSegment(sketch, "E408", {"start": v(-1506.46, 299.9) * mm, "end": v(-1506.46, 319.24) * mm});
            skLineSegment(sketch, "E409", {"start": v(-1506.46, 319.24) * mm, "end": v(-1521.56, 319.24) * mm});
            skArc(sketch, "E410", {"start": v(-1521.56, 319.24) * mm, "mid": v(-1686.56, 336.02) * mm, "end": v(-1851.56, 319.24) * mm});
            skLineSegment(sketch, "E411", {"start": v(-1851.56, 319.24) * mm, "end": v(-1866.66, 319.24) * mm});
            skLineSegment(sketch, "E412", {"start": v(-1866.66, 319.24) * mm, "end": v(-1866.66, 299.9) * mm});
            skArc(sketch, "E413", {"start": v(-1866.66, 299.9) * mm, "mid": v(-1866.66, 294.24) * mm, "end": v(-1872.32, 294.24) * mm});
            skLineSegment(sketch, "E414", {"start": v(-1872.32, 294.24) * mm, "end": v(-1876.2, 294.24) * mm});
            skArc(sketch, "E415", {"start": v(-1876.2, 294.24) * mm, "mid": v(-1881.86, 294.24) * mm, "end": v(-1881.86, 299.9) * mm});
            skLineSegment(sketch, "E416", {"start": v(-1881.86, 299.9) * mm, "end": v(-1881.86, 319.24) * mm});
            skLineSegment(sketch, "E417", {"start": v(-1881.86, 319.24) * mm, "end": v(-1891.96, 319.24) * mm});
            skArc(sketch, "E418", {"start": v(-1891.96, 319.24) * mm, "mid": v(-1899.03, 316.31) * mm, "end": v(-1901.96, 309.24) * mm});
            skLineSegment(sketch, "E419", {"start": v(-1901.96, 309.24) * mm, "end": v(-1901.96, 279.25) * mm});
            skArc(sketch, "E420", {"start": v(-1901.96, 279.25) * mm, "mid": v(-1899.03, 272.18) * mm, "end": v(-1891.96, 269.25) * mm});
            skLineSegment(sketch, "E421", {"start": v(-1891.96, 269.25) * mm, "end": v(-1866.53, 269.25) * mm});
            skArc(sketch, "E422", {"start": v(-1866.53, 203.72) * mm, "mid": v(-1686.56, 223.72) * mm, "end": v(-1506.6, 203.72) * mm});
            skLineSegment(sketch, "E423", {"start": v(-1506.6, 203.72) * mm, "end": v(-1481.16, 203.72) * mm});
            skArc(sketch, "E424", {"start": v(-1481.16, 203.72) * mm, "mid": v(-1474.09, 206.65) * mm, "end": v(-1471.16, 213.72) * mm});
            skLineSegment(sketch, "E425", {"start": v(-1471.16, 213.72) * mm, "end": v(-1471.16, 243.7) * mm});
            skArc(sketch, "E426", {"start": v(-1471.16, 243.7) * mm, "mid": v(-1474.09, 250.78) * mm, "end": v(-1481.16, 253.7) * mm});
            skLineSegment(sketch, "E427", {"start": v(-1481.16, 253.7) * mm, "end": v(-1491.26, 253.7) * mm});
            skLineSegment(sketch, "E428", {"start": v(-1491.26, 253.7) * mm, "end": v(-1491.26, 234.37) * mm});
            skArc(sketch, "E429", {"start": v(-1491.26, 234.37) * mm, "mid": v(-1491.26, 228.7) * mm, "end": v(-1496.92, 228.7) * mm});
            skLineSegment(sketch, "E430", {"start": v(-1496.92, 228.7) * mm, "end": v(-1500.8, 228.7) * mm});
            skArc(sketch, "E431", {"start": v(-1500.8, 228.7) * mm, "mid": v(-1506.46, 228.7) * mm, "end": v(-1506.46, 234.37) * mm});
            skLineSegment(sketch, "E432", {"start": v(-1506.46, 234.37) * mm, "end": v(-1506.46, 253.7) * mm});
            skLineSegment(sketch, "E433", {"start": v(-1506.46, 253.7) * mm, "end": v(-1521.56, 253.7) * mm});
            skArc(sketch, "E434", {"start": v(-1521.56, 253.7) * mm, "mid": v(-1686.56, 270.49) * mm, "end": v(-1851.56, 253.7) * mm});
            skLineSegment(sketch, "E435", {"start": v(-1851.56, 253.7) * mm, "end": v(-1866.66, 253.7) * mm});
            skLineSegment(sketch, "E436", {"start": v(-1866.66, 253.7) * mm, "end": v(-1866.66, 234.37) * mm});
            skArc(sketch, "E437", {"start": v(-1866.66, 234.37) * mm, "mid": v(-1866.66, 228.7) * mm, "end": v(-1872.32, 228.7) * mm});
            skLineSegment(sketch, "E438", {"start": v(-1872.32, 228.7) * mm, "end": v(-1876.2, 228.7) * mm});
            skArc(sketch, "E439", {"start": v(-1876.2, 228.7) * mm, "mid": v(-1881.86, 228.7) * mm, "end": v(-1881.86, 234.37) * mm});
            skLineSegment(sketch, "E440", {"start": v(-1881.86, 234.37) * mm, "end": v(-1881.86, 253.7) * mm});
            skLineSegment(sketch, "E441", {"start": v(-1881.86, 253.7) * mm, "end": v(-1891.96, 253.7) * mm});
            skArc(sketch, "E442", {"start": v(-1891.96, 253.7) * mm, "mid": v(-1899.03, 250.78) * mm, "end": v(-1901.96, 243.7) * mm});
            skLineSegment(sketch, "E443", {"start": v(-1901.96, 243.7) * mm, "end": v(-1901.96, 213.72) * mm});
            skArc(sketch, "E444", {"start": v(-1901.96, 213.72) * mm, "mid": v(-1899.03, 206.65) * mm, "end": v(-1891.96, 203.72) * mm});
            skLineSegment(sketch, "E445", {"start": v(-1891.96, 203.72) * mm, "end": v(-1866.53, 203.72) * mm});
            skArc(sketch, "E446", {"start": v(-2159.63, 81.3) * mm, "mid": v(-2339.6, 61.3) * mm, "end": v(-2519.57, 81.3) * mm});
            skLineSegment(sketch, "E447", {"start": v(-2519.57, 81.3) * mm, "end": v(-2545, 81.3) * mm});
            skArc(sketch, "E448", {"start": v(-2545, 81.3) * mm, "mid": v(-2552.07, 78.37) * mm, "end": v(-2555, 71.3) * mm});
            skLineSegment(sketch, "E449", {"start": v(-2555, 71.3) * mm, "end": v(-2555, 41.3) * mm});
            skArc(sketch, "E450", {"start": v(-2555, 41.3) * mm, "mid": v(-2552.07, 34.24) * mm, "end": v(-2545, 31.3) * mm});
            skLineSegment(sketch, "E451", {"start": v(-2545, 31.3) * mm, "end": v(-2534.9, 31.3) * mm});
            skLineSegment(sketch, "E452", {"start": v(-2534.9, 31.3) * mm, "end": v(-2534.9, 50.65) * mm});
            skArc(sketch, "E453", {"start": v(-2534.9, 50.65) * mm, "mid": v(-2534.9, 56.3) * mm, "end": v(-2529.24, 56.3) * mm});
            skLineSegment(sketch, "E454", {"start": v(-2529.24, 56.3) * mm, "end": v(-2525.36, 56.3) * mm});
            skArc(sketch, "E455", {"start": v(-2525.36, 56.3) * mm, "mid": v(-2519.7, 56.3) * mm, "end": v(-2519.7, 50.65) * mm});
            skLineSegment(sketch, "E456", {"start": v(-2519.7, 50.65) * mm, "end": v(-2519.7, 31.3) * mm});
            skLineSegment(sketch, "E457", {"start": v(-2519.7, 31.3) * mm, "end": v(-2504.6, 31.3) * mm});
            skArc(sketch, "E458", {"start": v(-2504.6, 31.3) * mm, "mid": v(-2339.6, 14.53) * mm, "end": v(-2174.6, 31.3) * mm});
            skLineSegment(sketch, "E459", {"start": v(-2174.6, 31.3) * mm, "end": v(-2159.5, 31.3) * mm});
            skLineSegment(sketch, "E460", {"start": v(-2159.5, 31.3) * mm, "end": v(-2159.5, 50.65) * mm});
            skArc(sketch, "E461", {"start": v(-2159.5, 50.65) * mm, "mid": v(-2159.5, 56.3) * mm, "end": v(-2153.84, 56.3) * mm});
            skLineSegment(sketch, "E462", {"start": v(-2153.84, 56.3) * mm, "end": v(-2149.96, 56.3) * mm});
            skArc(sketch, "E463", {"start": v(-2149.96, 56.3) * mm, "mid": v(-2144.3, 56.3) * mm, "end": v(-2144.3, 50.65) * mm});
            skLineSegment(sketch, "E464", {"start": v(-2144.3, 50.65) * mm, "end": v(-2144.3, 31.3) * mm});
            skLineSegment(sketch, "E465", {"start": v(-2144.3, 31.3) * mm, "end": v(-2134.2, 31.3) * mm});
            skArc(sketch, "E466", {"start": v(-2134.2, 31.3) * mm, "mid": v(-2127.13, 34.24) * mm, "end": v(-2124.2, 41.3) * mm});
            skLineSegment(sketch, "E467", {"start": v(-2124.2, 41.3) * mm, "end": v(-2124.2, 71.3) * mm});
            skArc(sketch, "E468", {"start": v(-2124.2, 71.3) * mm, "mid": v(-2127.13, 78.37) * mm, "end": v(-2134.2, 81.3) * mm});
            skLineSegment(sketch, "E469", {"start": v(-2134.2, 81.3) * mm, "end": v(-2159.63, 81.3) * mm});
            skArc(sketch, "E470", {"start": v(-2159.63, 15.77) * mm, "mid": v(-2339.6, -4.23) * mm, "end": v(-2519.57, 15.77) * mm});
            skLineSegment(sketch, "E471", {"start": v(-2519.57, 15.77) * mm, "end": v(-2545, 15.77) * mm});
            skArc(sketch, "E472", {"start": v(-2545, 15.77) * mm, "mid": v(-2552.07, 12.84) * mm, "end": v(-2555, 5.77) * mm});
            skLineSegment(sketch, "E473", {"start": v(-2555, 5.77) * mm, "end": v(-2555, -24.22) * mm});
            skArc(sketch, "E474", {"start": v(-2555, -24.22) * mm, "mid": v(-2552.07, -31.3) * mm, "end": v(-2545, -34.22) * mm});
            skLineSegment(sketch, "E475", {"start": v(-2545, -34.22) * mm, "end": v(-2534.9, -34.22) * mm});
            skLineSegment(sketch, "E476", {"start": v(-2534.9, -34.22) * mm, "end": v(-2534.9, -14.88) * mm});
            skArc(sketch, "E477", {"start": v(-2534.9, -14.88) * mm, "mid": v(-2534.9, -9.22) * mm, "end": v(-2529.24, -9.22) * mm});
            skLineSegment(sketch, "E478", {"start": v(-2529.24, -9.22) * mm, "end": v(-2525.36, -9.22) * mm});
            skArc(sketch, "E479", {"start": v(-2525.36, -9.22) * mm, "mid": v(-2519.7, -9.22) * mm, "end": v(-2519.7, -14.88) * mm});
            skLineSegment(sketch, "E480", {"start": v(-2519.7, -14.88) * mm, "end": v(-2519.7, -34.22) * mm});
            skLineSegment(sketch, "E481", {"start": v(-2519.7, -34.22) * mm, "end": v(-2504.6, -34.22) * mm});
            skArc(sketch, "E482", {"start": v(-2504.6, -34.22) * mm, "mid": v(-2339.6, -51) * mm, "end": v(-2174.6, -34.22) * mm});
            skLineSegment(sketch, "E483", {"start": v(-2174.6, -34.22) * mm, "end": v(-2159.5, -34.22) * mm});
            skLineSegment(sketch, "E484", {"start": v(-2159.5, -34.22) * mm, "end": v(-2159.5, -14.88) * mm});
            skArc(sketch, "E485", {"start": v(-2159.5, -14.88) * mm, "mid": v(-2159.5, -9.22) * mm, "end": v(-2153.84, -9.22) * mm});
            skLineSegment(sketch, "E486", {"start": v(-2153.84, -9.22) * mm, "end": v(-2149.96, -9.22) * mm});
            skArc(sketch, "E487", {"start": v(-2149.96, -9.22) * mm, "mid": v(-2144.3, -9.22) * mm, "end": v(-2144.3, -14.88) * mm});
            skLineSegment(sketch, "E488", {"start": v(-2144.3, -14.88) * mm, "end": v(-2144.3, -34.22) * mm});
            skLineSegment(sketch, "E489", {"start": v(-2144.3, -34.22) * mm, "end": v(-2134.2, -34.22) * mm});
            skArc(sketch, "E490", {"start": v(-2134.2, -34.22) * mm, "mid": v(-2127.13, -31.3) * mm, "end": v(-2124.2, -24.22) * mm});
            skLineSegment(sketch, "E491", {"start": v(-2124.2, -24.22) * mm, "end": v(-2124.2, 5.77) * mm});
            skArc(sketch, "E492", {"start": v(-2124.2, 5.77) * mm, "mid": v(-2127.13, 12.84) * mm, "end": v(-2134.2, 15.77) * mm});
            skLineSegment(sketch, "E493", {"start": v(-2134.2, 15.77) * mm, "end": v(-2159.63, 15.77) * mm});
            skArc(sketch, "E494", {"start": v(-2159.63, 146.83) * mm, "mid": v(-2339.6, 126.83) * mm, "end": v(-2519.57, 146.83) * mm});
            skLineSegment(sketch, "E495", {"start": v(-2519.57, 146.83) * mm, "end": v(-2545, 146.83) * mm});
            skArc(sketch, "E496", {"start": v(-2545, 146.83) * mm, "mid": v(-2552.07, 143.9) * mm, "end": v(-2555, 136.83) * mm});
            skLineSegment(sketch, "E497", {"start": v(-2555, 136.83) * mm, "end": v(-2555, 106.84) * mm});
            skArc(sketch, "E498", {"start": v(-2555, 106.84) * mm, "mid": v(-2552.07, 99.77) * mm, "end": v(-2545, 96.84) * mm});
            skLineSegment(sketch, "E499", {"start": v(-2545, 96.84) * mm, "end": v(-2534.9, 96.84) * mm});
            skLineSegment(sketch, "E500", {"start": v(-2534.9, 96.84) * mm, "end": v(-2534.9, 116.18) * mm});
            skArc(sketch, "E501", {"start": v(-2534.9, 116.18) * mm, "mid": v(-2534.9, 121.84) * mm, "end": v(-2529.24, 121.84) * mm});
            skLineSegment(sketch, "E502", {"start": v(-2529.24, 121.84) * mm, "end": v(-2525.36, 121.84) * mm});
            skArc(sketch, "E503", {"start": v(-2525.36, 121.84) * mm, "mid": v(-2519.7, 121.84) * mm, "end": v(-2519.7, 116.18) * mm});
            skLineSegment(sketch, "E504", {"start": v(-2519.7, 116.18) * mm, "end": v(-2519.7, 96.84) * mm});
            skLineSegment(sketch, "E505", {"start": v(-2519.7, 96.84) * mm, "end": v(-2504.6, 96.84) * mm});
            skArc(sketch, "E506", {"start": v(-2504.6, 96.84) * mm, "mid": v(-2339.6, 80.06) * mm, "end": v(-2174.6, 96.84) * mm});
            skLineSegment(sketch, "E507", {"start": v(-2174.6, 96.84) * mm, "end": v(-2159.5, 96.84) * mm});
            skLineSegment(sketch, "E508", {"start": v(-2159.5, 96.84) * mm, "end": v(-2159.5, 116.18) * mm});
            skArc(sketch, "E509", {"start": v(-2159.5, 116.18) * mm, "mid": v(-2159.5, 121.84) * mm, "end": v(-2153.84, 121.84) * mm});
            skLineSegment(sketch, "E510", {"start": v(-2153.84, 121.84) * mm, "end": v(-2149.96, 121.84) * mm});
            skArc(sketch, "E511", {"start": v(-2149.96, 121.84) * mm, "mid": v(-2144.3, 121.84) * mm, "end": v(-2144.3, 116.18) * mm});
            skLineSegment(sketch, "E512", {"start": v(-2144.3, 116.18) * mm, "end": v(-2144.3, 96.84) * mm});
            skLineSegment(sketch, "E513", {"start": v(-2144.3, 96.84) * mm, "end": v(-2134.2, 96.84) * mm});
            skArc(sketch, "E514", {"start": v(-2134.2, 96.84) * mm, "mid": v(-2127.13, 99.77) * mm, "end": v(-2124.2, 106.84) * mm});
            skLineSegment(sketch, "E515", {"start": v(-2124.2, 106.84) * mm, "end": v(-2124.2, 136.83) * mm});
            skArc(sketch, "E516", {"start": v(-2124.2, 136.83) * mm, "mid": v(-2127.13, 143.9) * mm, "end": v(-2134.2, 146.83) * mm});
            skLineSegment(sketch, "E517", {"start": v(-2134.2, 146.83) * mm, "end": v(-2159.63, 146.83) * mm});
            skArc(sketch, "E518", {"start": v(-2159.63, 212.37) * mm, "mid": v(-2339.6, 192.37) * mm, "end": v(-2519.57, 212.37) * mm});
            skLineSegment(sketch, "E519", {"start": v(-2519.57, 212.37) * mm, "end": v(-2545, 212.37) * mm});
            skArc(sketch, "E520", {"start": v(-2545, 212.37) * mm, "mid": v(-2552.07, 209.44) * mm, "end": v(-2555, 202.37) * mm});
            skLineSegment(sketch, "E521", {"start": v(-2555, 202.37) * mm, "end": v(-2555, 172.37) * mm});
            skArc(sketch, "E522", {"start": v(-2555, 172.37) * mm, "mid": v(-2552.07, 165.3) * mm, "end": v(-2545, 162.37) * mm});
            skLineSegment(sketch, "E523", {"start": v(-2545, 162.37) * mm, "end": v(-2534.9, 162.37) * mm});
            skLineSegment(sketch, "E524", {"start": v(-2534.9, 162.37) * mm, "end": v(-2534.9, 181.72) * mm});
            skArc(sketch, "E525", {"start": v(-2534.9, 181.72) * mm, "mid": v(-2534.9, 187.37) * mm, "end": v(-2529.24, 187.37) * mm});
            skLineSegment(sketch, "E526", {"start": v(-2529.24, 187.37) * mm, "end": v(-2525.36, 187.37) * mm});
            skArc(sketch, "E527", {"start": v(-2525.36, 187.37) * mm, "mid": v(-2519.7, 187.37) * mm, "end": v(-2519.7, 181.72) * mm});
            skLineSegment(sketch, "E528", {"start": v(-2519.7, 181.72) * mm, "end": v(-2519.7, 162.37) * mm});
            skLineSegment(sketch, "E529", {"start": v(-2519.7, 162.37) * mm, "end": v(-2504.6, 162.37) * mm});
            skArc(sketch, "E530", {"start": v(-2504.6, 162.37) * mm, "mid": v(-2339.6, 145.6) * mm, "end": v(-2174.6, 162.37) * mm});
            skLineSegment(sketch, "E531", {"start": v(-2174.6, 162.37) * mm, "end": v(-2159.5, 162.37) * mm});
            skLineSegment(sketch, "E532", {"start": v(-2159.5, 162.37) * mm, "end": v(-2159.5, 181.72) * mm});
            skArc(sketch, "E533", {"start": v(-2159.5, 181.72) * mm, "mid": v(-2159.5, 187.37) * mm, "end": v(-2153.84, 187.37) * mm});
            skLineSegment(sketch, "E534", {"start": v(-2153.84, 187.37) * mm, "end": v(-2149.96, 187.37) * mm});
            skArc(sketch, "E535", {"start": v(-2149.96, 187.37) * mm, "mid": v(-2144.3, 187.37) * mm, "end": v(-2144.3, 181.72) * mm});
            skLineSegment(sketch, "E536", {"start": v(-2144.3, 181.72) * mm, "end": v(-2144.3, 162.37) * mm});
            skLineSegment(sketch, "E537", {"start": v(-2144.3, 162.37) * mm, "end": v(-2134.2, 162.37) * mm});
            skArc(sketch, "E538", {"start": v(-2134.2, 162.37) * mm, "mid": v(-2127.13, 165.3) * mm, "end": v(-2124.2, 172.37) * mm});
            skLineSegment(sketch, "E539", {"start": v(-2124.2, 172.37) * mm, "end": v(-2124.2, 202.37) * mm});
            skArc(sketch, "E540", {"start": v(-2124.2, 202.37) * mm, "mid": v(-2127.13, 209.44) * mm, "end": v(-2134.2, 212.37) * mm});
            skLineSegment(sketch, "E541", {"start": v(-2134.2, 212.37) * mm, "end": v(-2159.63, 212.37) * mm});
            skArc(sketch, "E542", {"start": v(-1385, -338.79) * mm, "mid": v(-1405, -158.82) * mm, "end": v(-1385, 21.14) * mm});
            skLineSegment(sketch, "E543", {"start": v(-1385, 21.14) * mm, "end": v(-1385, 46.58) * mm});
            skArc(sketch, "E544", {"start": v(-1385, 46.58) * mm, "mid": v(-1387.93, 53.65) * mm, "end": v(-1395, 56.58) * mm});
            skLineSegment(sketch, "E545", {"start": v(-1395, 56.58) * mm, "end": v(-1425, 56.58) * mm});
            skArc(sketch, "E546", {"start": v(-1425, 56.58) * mm, "mid": v(-1432.06, 53.65) * mm, "end": v(-1435, 46.58) * mm});
            skLineSegment(sketch, "E547", {"start": v(-1435, 46.58) * mm, "end": v(-1435, 36.48) * mm});
            skLineSegment(sketch, "E548", {"start": v(-1435, 36.48) * mm, "end": v(-1415.65, 36.48) * mm});
            skArc(sketch, "E549", {"start": v(-1415.65, 36.48) * mm, "mid": v(-1410, 36.48) * mm, "end": v(-1410, 30.82) * mm});
            skLineSegment(sketch, "E550", {"start": v(-1410, 30.82) * mm, "end": v(-1410, 26.93) * mm});
            skArc(sketch, "E551", {"start": v(-1410, 26.93) * mm, "mid": v(-1410, 21.28) * mm, "end": v(-1415.65, 21.28) * mm});
            skLineSegment(sketch, "E552", {"start": v(-1415.65, 21.28) * mm, "end": v(-1435, 21.28) * mm});
            skLineSegment(sketch, "E553", {"start": v(-1435, 21.28) * mm, "end": v(-1435, 6.18) * mm});
            skArc(sketch, "E554", {"start": v(-1435, 6.18) * mm, "mid": v(-1451.77, -158.82) * mm, "end": v(-1435, -323.82) * mm});
            skLineSegment(sketch, "E555", {"start": v(-1435, -323.82) * mm, "end": v(-1435, -338.92) * mm});
            skLineSegment(sketch, "E556", {"start": v(-1435, -338.92) * mm, "end": v(-1415.65, -338.92) * mm});
            skArc(sketch, "E557", {"start": v(-1415.65, -338.92) * mm, "mid": v(-1410, -338.92) * mm, "end": v(-1410, -344.58) * mm});
            skLineSegment(sketch, "E558", {"start": v(-1410, -344.58) * mm, "end": v(-1410, -348.47) * mm});
            skArc(sketch, "E559", {"start": v(-1410, -348.47) * mm, "mid": v(-1410, -354.12) * mm, "end": v(-1415.65, -354.12) * mm});
            skLineSegment(sketch, "E560", {"start": v(-1415.65, -354.12) * mm, "end": v(-1435, -354.12) * mm});
            skLineSegment(sketch, "E561", {"start": v(-1435, -354.12) * mm, "end": v(-1435, -364.22) * mm});
            skArc(sketch, "E562", {"start": v(-1435, -364.22) * mm, "mid": v(-1432.06, -371.3) * mm, "end": v(-1425, -374.22) * mm});
            skLineSegment(sketch, "E563", {"start": v(-1425, -374.22) * mm, "end": v(-1395, -374.22) * mm});
            skArc(sketch, "E564", {"start": v(-1395, -374.22) * mm, "mid": v(-1387.93, -371.3) * mm, "end": v(-1385, -364.22) * mm});
            skLineSegment(sketch, "E565", {"start": v(-1385, -364.22) * mm, "end": v(-1385, -338.79) * mm});
            skLineSegment(sketch, "E566", {"start": v(-2353.4, 351.52) * mm, "end": v(-2348.38, 370.2) * mm});
            skArc(sketch, "E567", {"start": v(-2348.38, 370.2) * mm, "mid": v(-2346.92, 375.66) * mm, "end": v(-2341.46, 374.2) * mm});
            skLineSegment(sketch, "E568", {"start": v(-2341.46, 374.2) * mm, "end": v(-2337.7, 373.2) * mm});
            skArc(sketch, "E569", {"start": v(-2337.7, 373.2) * mm, "mid": v(-2332.24, 371.73) * mm, "end": v(-2333.7, 366.27) * mm});
            skLineSegment(sketch, "E570", {"start": v(-2333.7, 366.27) * mm, "end": v(-2338.7, 347.58) * mm});
            skLineSegment(sketch, "E571", {"start": v(-2338.7, 347.58) * mm, "end": v(-2319.58, 342.46) * mm});
            skLineSegment(sketch, "E572", {"start": v(-2319.58, 342.46) * mm, "end": v(-2314.58, 361.14) * mm});
            skArc(sketch, "E573", {"start": v(-2314.58, 361.14) * mm, "mid": v(-2313.11, 366.6) * mm, "end": v(-2307.65, 365.14) * mm});
            skLineSegment(sketch, "E574", {"start": v(-2307.65, 365.14) * mm, "end": v(-2303.9, 364.13) * mm});
            skArc(sketch, "E575", {"start": v(-2303.9, 364.13) * mm, "mid": v(-2298.43, 362.67) * mm, "end": v(-2299.9, 357.2) * mm});
            skLineSegment(sketch, "E576", {"start": v(-2299.9, 357.2) * mm, "end": v(-2304.9, 338.52) * mm});
            skLineSegment(sketch, "E577", {"start": v(-2304.9, 338.52) * mm, "end": v(-2285.78, 333.4) * mm});
            skLineSegment(sketch, "E578", {"start": v(-2285.78, 333.4) * mm, "end": v(-2280.77, 352.08) * mm});
            skArc(sketch, "E579", {"start": v(-2280.77, 352.08) * mm, "mid": v(-2279.3, 357.55) * mm, "end": v(-2273.84, 356.08) * mm});
            skLineSegment(sketch, "E580", {"start": v(-2273.84, 356.08) * mm, "end": v(-2270.09, 355.08) * mm});
            skArc(sketch, "E581", {"start": v(-2270.09, 355.08) * mm, "mid": v(-2264.62, 353.61) * mm, "end": v(-2266.09, 348.15) * mm});
            skLineSegment(sketch, "E582", {"start": v(-2266.09, 348.15) * mm, "end": v(-2271.1, 329.46) * mm});
            skLineSegment(sketch, "E583", {"start": v(-2271.1, 329.46) * mm, "end": v(-2251.97, 324.34) * mm});
            skLineSegment(sketch, "E584", {"start": v(-2251.97, 324.34) * mm, "end": v(-2246.96, 343.02) * mm});
            skArc(sketch, "E585", {"start": v(-2246.96, 343.02) * mm, "mid": v(-2245.5, 348.49) * mm, "end": v(-2240.03, 347.02) * mm});
            skLineSegment(sketch, "E586", {"start": v(-2240.03, 347.02) * mm, "end": v(-2236.28, 346.02) * mm});
            skArc(sketch, "E587", {"start": v(-2236.28, 346.02) * mm, "mid": v(-2230.82, 344.55) * mm, "end": v(-2232.28, 339.09) * mm});
            skLineSegment(sketch, "E588", {"start": v(-2232.28, 339.09) * mm, "end": v(-2237.29, 320.4) * mm});
            skLineSegment(sketch, "E589", {"start": v(-2237.29, 320.4) * mm, "end": v(-2218.16, 315.28) * mm});
            skLineSegment(sketch, "E590", {"start": v(-2218.16, 315.28) * mm, "end": v(-2213.15, 333.96) * mm});
            skArc(sketch, "E591", {"start": v(-2213.15, 333.96) * mm, "mid": v(-2211.7, 339.43) * mm, "end": v(-2206.23, 337.96) * mm});
            skLineSegment(sketch, "E592", {"start": v(-2206.23, 337.96) * mm, "end": v(-2202.47, 336.96) * mm});
            skArc(sketch, "E593", {"start": v(-2202.47, 336.96) * mm, "mid": v(-2197, 335.5) * mm, "end": v(-2198.47, 330.03) * mm});
            skLineSegment(sketch, "E594", {"start": v(-2198.47, 330.03) * mm, "end": v(-2203.48, 311.35) * mm});
            skLineSegment(sketch, "E595", {"start": v(-2203.48, 311.35) * mm, "end": v(-2182.14, 305.63) * mm});
            skArc(sketch, "E596", {"start": v(-2182.14, 305.63) * mm, "mid": v(-2171.56, 303.98) * mm, "end": v(-2160.87, 304.62) * mm});
            skLineSegment(sketch, "E597", {"start": v(-2160.87, 304.62) * mm, "end": v(-2055.99, 321.7) * mm});
            skArc(sketch, "E598", {"start": v(-2055.99, 321.7) * mm, "mid": v(-2031.45, 314.7) * mm, "end": v(-2021.17, 291.35) * mm});
            skLineSegment(sketch, "E599", {"start": v(-2021.17, 291.35) * mm, "end": v(-2021.94, 260.67) * mm});
            skLineSegment(sketch, "E600", {"start": v(-2021.94, 260.67) * mm, "end": v(-2002.6, 260.2) * mm});
            skArc(sketch, "E601", {"start": v(-2002.6, 260.2) * mm, "mid": v(-1996.95, 260.05) * mm, "end": v(-1997.09, 254.4) * mm});
            skLineSegment(sketch, "E602", {"start": v(-1997.09, 254.4) * mm, "end": v(-1997.18, 250.5) * mm});
            skArc(sketch, "E603", {"start": v(-1997.18, 250.5) * mm, "mid": v(-1997.33, 244.85) * mm, "end": v(-2002.98, 245) * mm});
            skLineSegment(sketch, "E604", {"start": v(-2002.98, 245) * mm, "end": v(-2022.32, 245.48) * mm});
            skLineSegment(sketch, "E605", {"start": v(-2022.32, 245.48) * mm, "end": v(-2022.81, 225.68) * mm});
            skLineSegment(sketch, "E606", {"start": v(-2022.81, 225.68) * mm, "end": v(-2003.47, 225.2) * mm});
            skArc(sketch, "E607", {"start": v(-2003.47, 225.2) * mm, "mid": v(-1997.82, 225.06) * mm, "end": v(-1997.96, 219.4) * mm});
            skLineSegment(sketch, "E608", {"start": v(-1997.96, 219.4) * mm, "end": v(-1998.06, 215.52) * mm});
            skArc(sketch, "E609", {"start": v(-1998.06, 215.52) * mm, "mid": v(-1998.2, 209.87) * mm, "end": v(-2003.85, 210) * mm});
            skLineSegment(sketch, "E610", {"start": v(-2003.85, 210) * mm, "end": v(-2023.19, 210.49) * mm});
            skLineSegment(sketch, "E611", {"start": v(-2023.19, 210.49) * mm, "end": v(-2023.68, 190.7) * mm});
            skLineSegment(sketch, "E612", {"start": v(-2023.68, 190.7) * mm, "end": v(-2004.35, 190.21) * mm});
            skArc(sketch, "E613", {"start": v(-2004.35, 190.21) * mm, "mid": v(-1998.7, 190.07) * mm, "end": v(-1998.83, 184.42) * mm});
            skLineSegment(sketch, "E614", {"start": v(-1998.83, 184.42) * mm, "end": v(-1998.93, 180.53) * mm});
            skArc(sketch, "E615", {"start": v(-1998.93, 180.53) * mm, "mid": v(-1999.07, 174.88) * mm, "end": v(-2004.72, 175.02) * mm});
            skLineSegment(sketch, "E616", {"start": v(-2004.72, 175.02) * mm, "end": v(-2024.06, 175.5) * mm});
            skLineSegment(sketch, "E617", {"start": v(-2024.06, 175.5) * mm, "end": v(-2024.56, 155.7) * mm});
            skLineSegment(sketch, "E618", {"start": v(-2024.56, 155.7) * mm, "end": v(-2005.22, 155.22) * mm});
            skArc(sketch, "E619", {"start": v(-2005.22, 155.22) * mm, "mid": v(-1999.56, 155.08) * mm, "end": v(-1999.7, 149.43) * mm});
            skLineSegment(sketch, "E620", {"start": v(-1999.7, 149.43) * mm, "end": v(-1999.8, 145.54) * mm});
            skArc(sketch, "E621", {"start": v(-1999.8, 145.54) * mm, "mid": v(-1999.94, 139.89) * mm, "end": v(-2005.6, 140.03) * mm});
            skLineSegment(sketch, "E622", {"start": v(-2005.6, 140.03) * mm, "end": v(-2024.93, 140.51) * mm});
            skLineSegment(sketch, "E623", {"start": v(-2024.93, 140.51) * mm, "end": v(-2025.43, 120.72) * mm});
            skLineSegment(sketch, "E624", {"start": v(-2025.43, 120.72) * mm, "end": v(-2006.1, 120.23) * mm});
            skArc(sketch, "E625", {"start": v(-2006.1, 120.23) * mm, "mid": v(-2000.44, 120.1) * mm, "end": v(-2000.58, 114.44) * mm});
            skLineSegment(sketch, "E626", {"start": v(-2000.58, 114.44) * mm, "end": v(-2000.67, 110.55) * mm});
            skArc(sketch, "E627", {"start": v(-2000.67, 110.55) * mm, "mid": v(-2000.81, 104.9) * mm, "end": v(-2006.47, 105.04) * mm});
            skLineSegment(sketch, "E628", {"start": v(-2006.47, 105.04) * mm, "end": v(-2025.8, 105.52) * mm});
            skLineSegment(sketch, "E629", {"start": v(-2025.8, 105.52) * mm, "end": v(-2026.3, 85.73) * mm});
            skLineSegment(sketch, "E630", {"start": v(-2026.3, 85.73) * mm, "end": v(-2006.96, 85.25) * mm});
            skArc(sketch, "E631", {"start": v(-2006.96, 85.25) * mm, "mid": v(-2001.3, 85.1) * mm, "end": v(-2001.45, 79.45) * mm});
            skLineSegment(sketch, "E632", {"start": v(-2001.45, 79.45) * mm, "end": v(-2001.55, 75.56) * mm});
            skArc(sketch, "E633", {"start": v(-2001.55, 75.56) * mm, "mid": v(-2001.69, 69.9) * mm, "end": v(-2007.34, 70.05) * mm});
            skLineSegment(sketch, "E634", {"start": v(-2007.34, 70.05) * mm, "end": v(-2026.68, 70.53) * mm});
            skLineSegment(sketch, "E635", {"start": v(-2026.68, 70.53) * mm, "end": v(-2027.17, 50.74) * mm});
            skLineSegment(sketch, "E636", {"start": v(-2027.17, 50.74) * mm, "end": v(-2007.83, 50.26) * mm});
            skArc(sketch, "E637", {"start": v(-2007.83, 50.26) * mm, "mid": v(-2002.18, 50.12) * mm, "end": v(-2002.32, 44.46) * mm});
            skLineSegment(sketch, "E638", {"start": v(-2002.32, 44.46) * mm, "end": v(-2002.42, 40.58) * mm});
            skArc(sketch, "E639", {"start": v(-2002.42, 40.58) * mm, "mid": v(-2002.56, 34.92) * mm, "end": v(-2008.21, 35.06) * mm});
            skLineSegment(sketch, "E640", {"start": v(-2008.21, 35.06) * mm, "end": v(-2027.55, 35.54) * mm});
            skLineSegment(sketch, "E641", {"start": v(-2027.55, 35.54) * mm, "end": v(-2028.04, 15.75) * mm});
            skLineSegment(sketch, "E642", {"start": v(-2028.04, 15.75) * mm, "end": v(-2008.7, 15.27) * mm});
            skArc(sketch, "E643", {"start": v(-2008.7, 15.27) * mm, "mid": v(-2003.05, 15.13) * mm, "end": v(-2003.2, 9.47) * mm});
            skLineSegment(sketch, "E644", {"start": v(-2003.2, 9.47) * mm, "end": v(-2003.29, 5.59) * mm});
            skArc(sketch, "E645", {"start": v(-2003.29, 5.59) * mm, "mid": v(-2003.43, -0.07) * mm, "end": v(-2009.09, 0.07) * mm});
            skLineSegment(sketch, "E646", {"start": v(-2009.09, 0.07) * mm, "end": v(-2028.42, 0.55) * mm});
            skLineSegment(sketch, "E647", {"start": v(-2028.42, 0.55) * mm, "end": v(-2028.92, -19.24) * mm});
            skLineSegment(sketch, "E648", {"start": v(-2028.92, -19.24) * mm, "end": v(-2009.58, -19.72) * mm});
            skArc(sketch, "E649", {"start": v(-2009.58, -19.72) * mm, "mid": v(-2003.92, -19.86) * mm, "end": v(-2004.06, -25.52) * mm});
            skLineSegment(sketch, "E650", {"start": v(-2004.06, -25.52) * mm, "end": v(-2004.16, -29.4) * mm});
            skArc(sketch, "E651", {"start": v(-2004.16, -29.4) * mm, "mid": v(-2004.3, -35.06) * mm, "end": v(-2009.96, -34.92) * mm});
            skLineSegment(sketch, "E652", {"start": v(-2009.96, -34.92) * mm, "end": v(-2029.3, -34.44) * mm});
            skLineSegment(sketch, "E653", {"start": v(-2029.3, -34.44) * mm, "end": v(-2029.79, -54.23) * mm});
            skLineSegment(sketch, "E654", {"start": v(-2029.79, -54.23) * mm, "end": v(-2010.45, -54.71) * mm});
            skArc(sketch, "E655", {"start": v(-2010.45, -54.71) * mm, "mid": v(-2004.8, -54.85) * mm, "end": v(-2004.94, -60.5) * mm});
            skLineSegment(sketch, "E656", {"start": v(-2004.94, -60.5) * mm, "end": v(-2005.03, -64.4) * mm});
            skArc(sketch, "E657", {"start": v(-2005.03, -64.4) * mm, "mid": v(-2005.17, -70.05) * mm, "end": v(-2010.83, -69.9) * mm});
            skLineSegment(sketch, "E658", {"start": v(-2010.83, -69.9) * mm, "end": v(-2030.17, -69.42) * mm});
            skLineSegment(sketch, "E659", {"start": v(-2030.17, -69.42) * mm, "end": v(-2030.66, -89.2) * mm});
            skLineSegment(sketch, "E660", {"start": v(-2030.66, -89.2) * mm, "end": v(-1806.03, -109.45) * mm});
            skArc(sketch, "E661", {"start": v(-1806.03, -109.45) * mm, "mid": v(-1800.4, -109.96) * mm, "end": v(-1800.9, -115.6) * mm});
            skLineSegment(sketch, "E662", {"start": v(-1800.9, -115.6) * mm, "end": v(-1801.25, -119.46) * mm});
            skArc(sketch, "E663", {"start": v(-1801.25, -119.46) * mm, "mid": v(-1801.76, -125.1) * mm, "end": v(-1807.4, -124.6) * mm});
            skLineSegment(sketch, "E664", {"start": v(-1807.4, -124.6) * mm, "end": v(-2031.04, -104.43) * mm});
            skLineSegment(sketch, "E665", {"start": v(-2031.04, -104.43) * mm, "end": v(-2031.04, -104.53) * mm});
            skArc(sketch, "E666", {"start": v(-2031.04, -104.53) * mm, "mid": v(-2023.37, -125.1) * mm, "end": v(-2003.74, -134.94) * mm});
            skLineSegment(sketch, "E667", {"start": v(-2003.74, -134.94) * mm, "end": v(-1571.12, -173.94) * mm});
            skLineSegment(sketch, "E668", {"start": v(-1571.12, -173.94) * mm, "end": v(-1571.12, -110.66) * mm});
            skLineSegment(sketch, "E669", {"start": v(-1571.12, -110.66) * mm, "end": v(-1952.26, -76.3) * mm});
            skArc(sketch, "E670", {"start": v(-1952.26, -76.3) * mm, "mid": v(-1971.96, -66.39) * mm, "end": v(-1979.56, -45.68) * mm});
            skLineSegment(sketch, "E671", {"start": v(-1979.56, -45.68) * mm, "end": v(-1971.06, 295.44) * mm});
            skArc(sketch, "E672", {"start": v(-1971.06, 295.44) * mm, "mid": v(-1965.2, 312.5) * mm, "end": v(-1950.63, 323.12) * mm});
            skLineSegment(sketch, "E673", {"start": v(-1950.63, 323.12) * mm, "end": v(-1571.12, 445.04) * mm});
            skLineSegment(sketch, "E674", {"start": v(-1571.12, 445.04) * mm, "end": v(-1571.12, 495.04) * mm});
            skLineSegment(sketch, "E675", {"start": v(-1571.12, 495.04) * mm, "end": v(-1721.02, 459.73) * mm});
            skLineSegment(sketch, "E676", {"start": v(-1721.02, 459.73) * mm, "end": v(-1716.58, 440.9) * mm});
            skArc(sketch, "E677", {"start": v(-1716.58, 440.9) * mm, "mid": v(-1715.29, 435.4) * mm, "end": v(-1720.8, 434.1) * mm});
            skLineSegment(sketch, "E678", {"start": v(-1720.8, 434.1) * mm, "end": v(-1724.58, 433.2) * mm});
            skArc(sketch, "E679", {"start": v(-1724.58, 433.2) * mm, "mid": v(-1730.08, 431.9) * mm, "end": v(-1731.38, 437.42) * mm});
            skLineSegment(sketch, "E680", {"start": v(-1731.38, 437.42) * mm, "end": v(-1735.82, 456.24) * mm});
            skLineSegment(sketch, "E681", {"start": v(-1735.82, 456.24) * mm, "end": v(-2157.4, 356.93) * mm});
            skArc(sketch, "E682", {"start": v(-2157.4, 356.93) * mm, "mid": v(-2169.62, 355.6) * mm, "end": v(-2181.8, 357.3) * mm});
            skLineSegment(sketch, "E683", {"start": v(-2181.8, 357.3) * mm, "end": v(-2388.65, 412.73) * mm});
            skArc(sketch, "E684", {"start": v(-2388.65, 412.73) * mm, "mid": v(-2396.24, 411.73) * mm, "end": v(-2400.9, 405.66) * mm});
            skLineSegment(sketch, "E685", {"start": v(-2400.9, 405.66) * mm, "end": v(-2408.66, 376.68) * mm});
            skArc(sketch, "E686", {"start": v(-2408.66, 376.68) * mm, "mid": v(-2407.66, 369.09) * mm, "end": v(-2401.6, 364.43) * mm});
            skLineSegment(sketch, "E687", {"start": v(-2401.6, 364.43) * mm, "end": v(-2387.2, 360.57) * mm});
            skLineSegment(sketch, "E688", {"start": v(-2387.2, 360.57) * mm, "end": v(-2382.2, 379.26) * mm});
            skArc(sketch, "E689", {"start": v(-2382.2, 379.26) * mm, "mid": v(-2380.73, 384.72) * mm, "end": v(-2375.26, 383.26) * mm});
            skLineSegment(sketch, "E690", {"start": v(-2375.26, 383.26) * mm, "end": v(-2371.5, 382.25) * mm});
            skArc(sketch, "E691", {"start": v(-2371.5, 382.25) * mm, "mid": v(-2366.05, 380.79) * mm, "end": v(-2367.5, 375.32) * mm});
            skLineSegment(sketch, "E692", {"start": v(-2367.5, 375.32) * mm, "end": v(-2372.52, 356.64) * mm});
            skLineSegment(sketch, "E693", {"start": v(-2372.52, 356.64) * mm, "end": v(-2353.49, 351.54) * mm});
            skLineSegment(sketch, "E694", {"start": v(-1720.35, 772.25) * mm, "end": v(-1725.36, 753.57) * mm});
            skArc(sketch, "E695", {"start": v(-1725.36, 753.57) * mm, "mid": v(-1726.83, 748.1) * mm, "end": v(-1732.29, 749.57) * mm});
            skLineSegment(sketch, "E696", {"start": v(-1732.29, 749.57) * mm, "end": v(-1736.04, 750.57) * mm});
            skArc(sketch, "E697", {"start": v(-1736.04, 750.57) * mm, "mid": v(-1741.5, 752.04) * mm, "end": v(-1740.04, 757.5) * mm});
            skLineSegment(sketch, "E698", {"start": v(-1740.04, 757.5) * mm, "end": v(-1735.04, 776.19) * mm});
            skLineSegment(sketch, "E699", {"start": v(-1735.04, 776.19) * mm, "end": v(-1754.16, 781.31) * mm});
            skLineSegment(sketch, "E700", {"start": v(-1754.16, 781.31) * mm, "end": v(-1759.17, 762.63) * mm});
            skArc(sketch, "E701", {"start": v(-1759.17, 762.63) * mm, "mid": v(-1760.63, 757.16) * mm, "end": v(-1766.1, 758.63) * mm});
            skLineSegment(sketch, "E702", {"start": v(-1766.1, 758.63) * mm, "end": v(-1769.85, 759.63) * mm});
            skArc(sketch, "E703", {"start": v(-1769.85, 759.63) * mm, "mid": v(-1775.31, 761.1) * mm, "end": v(-1773.85, 766.56) * mm});
            skLineSegment(sketch, "E704", {"start": v(-1773.85, 766.56) * mm, "end": v(-1768.84, 785.24) * mm});
            skLineSegment(sketch, "E705", {"start": v(-1768.84, 785.24) * mm, "end": v(-1787.97, 790.37) * mm});
            skLineSegment(sketch, "E706", {"start": v(-1787.97, 790.37) * mm, "end": v(-1792.98, 771.68) * mm});
            skArc(sketch, "E707", {"start": v(-1792.98, 771.68) * mm, "mid": v(-1794.44, 766.22) * mm, "end": v(-1799.9, 767.68) * mm});
            skLineSegment(sketch, "E708", {"start": v(-1799.9, 767.68) * mm, "end": v(-1803.66, 768.7) * mm});
            skArc(sketch, "E709", {"start": v(-1803.66, 768.7) * mm, "mid": v(-1809.12, 770.15) * mm, "end": v(-1807.66, 775.62) * mm});
            skLineSegment(sketch, "E710", {"start": v(-1807.66, 775.62) * mm, "end": v(-1802.65, 794.3) * mm});
            skLineSegment(sketch, "E711", {"start": v(-1802.65, 794.3) * mm, "end": v(-1821.78, 799.43) * mm});
            skLineSegment(sketch, "E712", {"start": v(-1821.78, 799.43) * mm, "end": v(-1826.78, 780.74) * mm});
            skArc(sketch, "E713", {"start": v(-1826.78, 780.74) * mm, "mid": v(-1828.25, 775.28) * mm, "end": v(-1833.71, 776.74) * mm});
            skLineSegment(sketch, "E714", {"start": v(-1833.71, 776.74) * mm, "end": v(-1837.47, 777.75) * mm});
            skArc(sketch, "E715", {"start": v(-1837.47, 777.75) * mm, "mid": v(-1842.93, 779.21) * mm, "end": v(-1841.47, 784.68) * mm});
            skLineSegment(sketch, "E716", {"start": v(-1841.47, 784.68) * mm, "end": v(-1836.46, 803.36) * mm});
            skLineSegment(sketch, "E717", {"start": v(-1836.46, 803.36) * mm, "end": v(-1855.58, 808.49) * mm});
            skLineSegment(sketch, "E718", {"start": v(-1855.58, 808.49) * mm, "end": v(-1860.6, 789.8) * mm});
            skArc(sketch, "E719", {"start": v(-1860.6, 789.8) * mm, "mid": v(-1862.05, 784.34) * mm, "end": v(-1867.52, 785.8) * mm});
            skLineSegment(sketch, "E720", {"start": v(-1867.52, 785.8) * mm, "end": v(-1871.27, 786.8) * mm});
            skArc(sketch, "E721", {"start": v(-1871.27, 786.8) * mm, "mid": v(-1876.74, 788.27) * mm, "end": v(-1875.27, 793.74) * mm});
            skLineSegment(sketch, "E722", {"start": v(-1875.27, 793.74) * mm, "end": v(-1870.27, 812.42) * mm});
            skLineSegment(sketch, "E723", {"start": v(-1870.27, 812.42) * mm, "end": v(-1891.6, 818.14) * mm});
            skArc(sketch, "E724", {"start": v(-1891.6, 818.14) * mm, "mid": v(-1902.18, 819.79) * mm, "end": v(-1912.87, 819.14) * mm});
            skLineSegment(sketch, "E725", {"start": v(-1912.87, 819.14) * mm, "end": v(-2017.76, 802.06) * mm});
            skArc(sketch, "E726", {"start": v(-2017.76, 802.06) * mm, "mid": v(-2042.3, 809.06) * mm, "end": v(-2052.57, 832.42) * mm});
            skLineSegment(sketch, "E727", {"start": v(-2052.57, 832.42) * mm, "end": v(-2051.8, 863.1) * mm});
            skLineSegment(sketch, "E728", {"start": v(-2051.8, 863.1) * mm, "end": v(-2071.14, 863.58) * mm});
            skArc(sketch, "E729", {"start": v(-2071.14, 863.58) * mm, "mid": v(-2076.8, 863.72) * mm, "end": v(-2076.66, 869.37) * mm});
            skLineSegment(sketch, "E730", {"start": v(-2076.66, 869.37) * mm, "end": v(-2076.56, 873.26) * mm});
            skArc(sketch, "E731", {"start": v(-2076.56, 873.26) * mm, "mid": v(-2076.42, 878.91) * mm, "end": v(-2070.77, 878.77) * mm});
            skLineSegment(sketch, "E732", {"start": v(-2070.77, 878.77) * mm, "end": v(-2051.43, 878.29) * mm});
            skLineSegment(sketch, "E733", {"start": v(-2051.43, 878.29) * mm, "end": v(-2050.93, 898.08) * mm});
            skLineSegment(sketch, "E734", {"start": v(-2050.93, 898.08) * mm, "end": v(-2070.27, 898.57) * mm});
            skArc(sketch, "E735", {"start": v(-2070.27, 898.57) * mm, "mid": v(-2075.93, 898.7) * mm, "end": v(-2075.79, 904.36) * mm});
            skLineSegment(sketch, "E736", {"start": v(-2075.79, 904.36) * mm, "end": v(-2075.69, 908.25) * mm});
            skArc(sketch, "E737", {"start": v(-2075.69, 908.25) * mm, "mid": v(-2075.55, 913.9) * mm, "end": v(-2069.9, 913.76) * mm});
            skLineSegment(sketch, "E738", {"start": v(-2069.9, 913.76) * mm, "end": v(-2050.56, 913.28) * mm});
            skLineSegment(sketch, "E739", {"start": v(-2050.56, 913.28) * mm, "end": v(-2050.06, 933.07) * mm});
            skLineSegment(sketch, "E740", {"start": v(-2050.06, 933.07) * mm, "end": v(-2069.4, 933.55) * mm});
            skArc(sketch, "E741", {"start": v(-2069.4, 933.55) * mm, "mid": v(-2075.05, 933.7) * mm, "end": v(-2074.91, 939.35) * mm});
            skLineSegment(sketch, "E742", {"start": v(-2074.91, 939.35) * mm, "end": v(-2074.82, 943.24) * mm});
            skArc(sketch, "E743", {"start": v(-2074.82, 943.24) * mm, "mid": v(-2074.68, 948.9) * mm, "end": v(-2069.02, 948.75) * mm});
            skLineSegment(sketch, "E744", {"start": v(-2069.02, 948.75) * mm, "end": v(-2049.68, 948.27) * mm});
            skLineSegment(sketch, "E745", {"start": v(-2049.68, 948.27) * mm, "end": v(-2049.2, 968.06) * mm});
            skLineSegment(sketch, "E746", {"start": v(-2049.2, 968.06) * mm, "end": v(-2068.53, 968.54) * mm});
            skArc(sketch, "E747", {"start": v(-2068.53, 968.54) * mm, "mid": v(-2074.18, 968.68) * mm, "end": v(-2074.04, 974.34) * mm});
            skLineSegment(sketch, "E748", {"start": v(-2074.04, 974.34) * mm, "end": v(-2073.94, 978.22) * mm});
            skArc(sketch, "E749", {"start": v(-2073.94, 978.22) * mm, "mid": v(-2073.8, 983.88) * mm, "end": v(-2068.15, 983.74) * mm});
            skLineSegment(sketch, "E750", {"start": v(-2068.15, 983.74) * mm, "end": v(-2048.81, 983.26) * mm});
            skLineSegment(sketch, "E751", {"start": v(-2048.81, 983.26) * mm, "end": v(-2048.32, 1003.05) * mm});
            skLineSegment(sketch, "E752", {"start": v(-2048.32, 1003.05) * mm, "end": v(-2067.66, 1003.53) * mm});
            skArc(sketch, "E753", {"start": v(-2067.66, 1003.53) * mm, "mid": v(-2073.31, 1003.67) * mm, "end": v(-2073.17, 1009.33) * mm});
            skLineSegment(sketch, "E754", {"start": v(-2073.17, 1009.33) * mm, "end": v(-2073.07, 1013.21) * mm});
            skArc(sketch, "E755", {"start": v(-2073.07, 1013.21) * mm, "mid": v(-2072.93, 1018.87) * mm, "end": v(-2067.28, 1018.73) * mm});
            skLineSegment(sketch, "E756", {"start": v(-2067.28, 1018.73) * mm, "end": v(-2047.94, 1018.25) * mm});
            skLineSegment(sketch, "E757", {"start": v(-2047.94, 1018.25) * mm, "end": v(-2047.45, 1038.04) * mm});
            skLineSegment(sketch, "E758", {"start": v(-2047.45, 1038.04) * mm, "end": v(-2066.78, 1038.52) * mm});
            skArc(sketch, "E759", {"start": v(-2066.78, 1038.52) * mm, "mid": v(-2072.44, 1038.66) * mm, "end": v(-2072.3, 1044.32) * mm});
            skLineSegment(sketch, "E760", {"start": v(-2072.3, 1044.32) * mm, "end": v(-2072.2, 1048.2) * mm});
            skArc(sketch, "E761", {"start": v(-2072.2, 1048.2) * mm, "mid": v(-2072.06, 1053.86) * mm, "end": v(-2066.4, 1053.72) * mm});
            skLineSegment(sketch, "E762", {"start": v(-2066.4, 1053.72) * mm, "end": v(-2047.07, 1053.23) * mm});
            skLineSegment(sketch, "E763", {"start": v(-2047.07, 1053.23) * mm, "end": v(-2046.57, 1073.03) * mm});
            skLineSegment(sketch, "E764", {"start": v(-2046.57, 1073.03) * mm, "end": v(-2065.91, 1073.51) * mm});
            skArc(sketch, "E765", {"start": v(-2065.91, 1073.51) * mm, "mid": v(-2071.57, 1073.65) * mm, "end": v(-2071.42, 1079.3) * mm});
            skLineSegment(sketch, "E766", {"start": v(-2071.42, 1079.3) * mm, "end": v(-2071.33, 1083.2) * mm});
            skArc(sketch, "E767", {"start": v(-2071.33, 1083.2) * mm, "mid": v(-2071.19, 1088.85) * mm, "end": v(-2065.53, 1088.7) * mm});
            skLineSegment(sketch, "E768", {"start": v(-2065.53, 1088.7) * mm, "end": v(-2046.2, 1088.22) * mm});
            skLineSegment(sketch, "E769", {"start": v(-2046.2, 1088.22) * mm, "end": v(-2045.7, 1108.02) * mm});
            skLineSegment(sketch, "E770", {"start": v(-2045.7, 1108.02) * mm, "end": v(-2065.04, 1108.5) * mm});
            skArc(sketch, "E771", {"start": v(-2065.04, 1108.5) * mm, "mid": v(-2070.7, 1108.64) * mm, "end": v(-2070.55, 1114.3) * mm});
            skLineSegment(sketch, "E772", {"start": v(-2070.55, 1114.3) * mm, "end": v(-2070.46, 1118.18) * mm});
            skArc(sketch, "E773", {"start": v(-2070.46, 1118.18) * mm, "mid": v(-2070.31, 1123.84) * mm, "end": v(-2064.66, 1123.7) * mm});
            skLineSegment(sketch, "E774", {"start": v(-2064.66, 1123.7) * mm, "end": v(-2045.32, 1123.21) * mm});
            skLineSegment(sketch, "E775", {"start": v(-2045.32, 1123.21) * mm, "end": v(-2044.83, 1143) * mm});
            skLineSegment(sketch, "E776", {"start": v(-2044.83, 1143) * mm, "end": v(-2064.17, 1143.49) * mm});
            skArc(sketch, "E777", {"start": v(-2064.17, 1143.49) * mm, "mid": v(-2069.82, 1143.63) * mm, "end": v(-2069.68, 1149.29) * mm});
            skLineSegment(sketch, "E778", {"start": v(-2069.68, 1149.29) * mm, "end": v(-2069.58, 1153.17) * mm});
            skArc(sketch, "E779", {"start": v(-2069.58, 1153.17) * mm, "mid": v(-2069.44, 1158.83) * mm, "end": v(-2063.79, 1158.68) * mm});
            skLineSegment(sketch, "E780", {"start": v(-2063.79, 1158.68) * mm, "end": v(-2044.45, 1158.2) * mm});
            skLineSegment(sketch, "E781", {"start": v(-2044.45, 1158.2) * mm, "end": v(-2043.96, 1178) * mm});
            skLineSegment(sketch, "E782", {"start": v(-2043.96, 1178) * mm, "end": v(-2063.3, 1178.48) * mm});
            skArc(sketch, "E783", {"start": v(-2063.3, 1178.48) * mm, "mid": v(-2068.95, 1178.62) * mm, "end": v(-2068.8, 1184.27) * mm});
            skLineSegment(sketch, "E784", {"start": v(-2068.8, 1184.27) * mm, "end": v(-2068.71, 1188.16) * mm});
            skArc(sketch, "E785", {"start": v(-2068.71, 1188.16) * mm, "mid": v(-2068.57, 1193.81) * mm, "end": v(-2062.92, 1193.67) * mm});
            skLineSegment(sketch, "E786", {"start": v(-2062.92, 1193.67) * mm, "end": v(-2043.58, 1193.2) * mm});
            skLineSegment(sketch, "E787", {"start": v(-2043.58, 1193.2) * mm, "end": v(-2043.09, 1212.97) * mm});
            skLineSegment(sketch, "E788", {"start": v(-2043.09, 1212.97) * mm, "end": v(-2267.72, 1233.22) * mm});
            skArc(sketch, "E789", {"start": v(-2267.72, 1233.22) * mm, "mid": v(-2273.35, 1233.73) * mm, "end": v(-2272.84, 1239.36) * mm});
            skLineSegment(sketch, "E790", {"start": v(-2272.84, 1239.36) * mm, "end": v(-2272.5, 1243.23) * mm});
            skArc(sketch, "E791", {"start": v(-2272.5, 1243.23) * mm, "mid": v(-2271.99, 1248.87) * mm, "end": v(-2266.35, 1248.36) * mm});
            skLineSegment(sketch, "E792", {"start": v(-2266.35, 1248.36) * mm, "end": v(-2042.7, 1228.2) * mm});
            skLineSegment(sketch, "E793", {"start": v(-2042.7, 1228.2) * mm, "end": v(-2042.7, 1228.3) * mm});
            skArc(sketch, "E794", {"start": v(-2042.7, 1228.3) * mm, "mid": v(-2050.38, 1248.87) * mm, "end": v(-2070, 1258.7) * mm});
            skLineSegment(sketch, "E795", {"start": v(-2070, 1258.7) * mm, "end": v(-2502.63, 1297.7) * mm});
            skLineSegment(sketch, "E796", {"start": v(-2502.63, 1297.7) * mm, "end": v(-2502.63, 1234.43) * mm});
            skLineSegment(sketch, "E797", {"start": v(-2502.63, 1234.43) * mm, "end": v(-2121.48, 1200.07) * mm});
            skArc(sketch, "E798", {"start": v(-2121.48, 1200.07) * mm, "mid": v(-2101.78, 1190.15) * mm, "end": v(-2094.19, 1169.45) * mm});
            skLineSegment(sketch, "E799", {"start": v(-2094.19, 1169.45) * mm, "end": v(-2102.69, 828.33) * mm});
            skArc(sketch, "E800", {"start": v(-2102.69, 828.33) * mm, "mid": v(-2108.54, 811.27) * mm, "end": v(-2123.12, 800.64) * mm});
            skLineSegment(sketch, "E801", {"start": v(-2123.12, 800.64) * mm, "end": v(-2502.63, 678.73) * mm});
            skLineSegment(sketch, "E802", {"start": v(-2502.63, 678.73) * mm, "end": v(-2502.63, 628.73) * mm});
            skLineSegment(sketch, "E803", {"start": v(-2502.63, 628.73) * mm, "end": v(-2352.73, 664.04) * mm});
            skLineSegment(sketch, "E804", {"start": v(-2352.73, 664.04) * mm, "end": v(-2357.16, 682.87) * mm});
            skArc(sketch, "E805", {"start": v(-2357.16, 682.87) * mm, "mid": v(-2358.46, 688.37) * mm, "end": v(-2352.95, 689.67) * mm});
            skLineSegment(sketch, "E806", {"start": v(-2352.95, 689.67) * mm, "end": v(-2349.17, 690.56) * mm});
            skArc(sketch, "E807", {"start": v(-2349.17, 690.56) * mm, "mid": v(-2343.66, 691.86) * mm, "end": v(-2342.37, 686.35) * mm});
            skLineSegment(sketch, "E808", {"start": v(-2342.37, 686.35) * mm, "end": v(-2337.93, 667.52) * mm});
            skLineSegment(sketch, "E809", {"start": v(-2337.93, 667.52) * mm, "end": v(-1916.35, 766.84) * mm});
            skArc(sketch, "E810", {"start": v(-1916.35, 766.84) * mm, "mid": v(-1904.12, 768.16) * mm, "end": v(-1891.94, 766.46) * mm});
            skLineSegment(sketch, "E811", {"start": v(-1891.94, 766.46) * mm, "end": v(-1685.1, 711.04) * mm});
            skArc(sketch, "E812", {"start": v(-1685.1, 711.04) * mm, "mid": v(-1677.5, 712.04) * mm, "end": v(-1672.85, 718.11) * mm});
            skLineSegment(sketch, "E813", {"start": v(-1672.85, 718.11) * mm, "end": v(-1665.08, 747.09) * mm});
            skArc(sketch, "E814", {"start": v(-1665.08, 747.09) * mm, "mid": v(-1666.08, 754.68) * mm, "end": v(-1672.16, 759.34) * mm});
            skLineSegment(sketch, "E815", {"start": v(-1672.16, 759.34) * mm, "end": v(-1686.55, 763.2) * mm});
            skLineSegment(sketch, "E816", {"start": v(-1686.55, 763.2) * mm, "end": v(-1691.55, 744.5) * mm});
            skArc(sketch, "E817", {"start": v(-1691.55, 744.5) * mm, "mid": v(-1693.02, 739.04) * mm, "end": v(-1698.48, 740.5) * mm});
            skLineSegment(sketch, "E818", {"start": v(-1698.48, 740.5) * mm, "end": v(-1702.24, 741.51) * mm});
            skArc(sketch, "E819", {"start": v(-1702.24, 741.51) * mm, "mid": v(-1707.7, 742.98) * mm, "end": v(-1706.24, 748.44) * mm});
            skLineSegment(sketch, "E820", {"start": v(-1706.24, 748.44) * mm, "end": v(-1701.23, 767.13) * mm});
            skLineSegment(sketch, "E821", {"start": v(-1701.23, 767.13) * mm, "end": v(-1720.26, 772.23) * mm});
            skArc(sketch, "E822", {"start": v(-1681.43, 639.42) * mm, "mid": v(-1675.77, 639.42) * mm, "end": v(-1675.77, 633.76) * mm});
            skLineSegment(sketch, "E823", {"start": v(-1675.77, 633.76) * mm, "end": v(-1675.77, 629.87) * mm});
            skArc(sketch, "E824", {"start": v(-1675.77, 629.87) * mm, "mid": v(-1675.77, 624.22) * mm, "end": v(-1681.43, 624.22) * mm});
            skLineSegment(sketch, "E825", {"start": v(-1681.43, 624.22) * mm, "end": v(-1905.99, 624.22) * mm});
            skLineSegment(sketch, "E826", {"start": v(-1905.99, 624.22) * mm, "end": v(-1905.99, 604.12) * mm});
            skLineSegment(sketch, "E827", {"start": v(-1905.99, 604.12) * mm, "end": v(-1455.55, 604.12) * mm});
            skArc(sketch, "E828", {"start": v(-1455.55, 604.12) * mm, "mid": v(-1448.48, 607.04) * mm, "end": v(-1445.55, 614.12) * mm});
            skLineSegment(sketch, "E829", {"start": v(-1445.55, 614.12) * mm, "end": v(-1445.55, 639.55) * mm});
            skArc(sketch, "E830", {"start": v(-1445.55, 639.55) * mm, "mid": v(-1465.55, 819.52) * mm, "end": v(-1445.55, 999.48) * mm});
            skLineSegment(sketch, "E831", {"start": v(-1445.55, 999.48) * mm, "end": v(-1445.55, 1024.92) * mm});
            skArc(sketch, "E832", {"start": v(-1445.55, 1024.92) * mm, "mid": v(-1448.48, 1031.99) * mm, "end": v(-1455.55, 1034.92) * mm});
            skLineSegment(sketch, "E833", {"start": v(-1455.55, 1034.92) * mm, "end": v(-1905.99, 1034.92) * mm});
            skLineSegment(sketch, "E834", {"start": v(-1905.99, 1034.92) * mm, "end": v(-1905.99, 1014.82) * mm});
            skLineSegment(sketch, "E835", {"start": v(-1905.99, 1014.82) * mm, "end": v(-1681.43, 1014.82) * mm});
            skArc(sketch, "E836", {"start": v(-1681.43, 1014.82) * mm, "mid": v(-1675.77, 1014.82) * mm, "end": v(-1675.77, 1009.16) * mm});
            skLineSegment(sketch, "E837", {"start": v(-1675.77, 1009.16) * mm, "end": v(-1675.77, 1005.27) * mm});
            skArc(sketch, "E838", {"start": v(-1675.77, 1005.27) * mm, "mid": v(-1675.77, 999.62) * mm, "end": v(-1681.43, 999.62) * mm});
            skLineSegment(sketch, "E839", {"start": v(-1681.43, 999.62) * mm, "end": v(-1905.99, 999.62) * mm});
            skLineSegment(sketch, "E840", {"start": v(-1905.99, 999.62) * mm, "end": v(-1905.99, 979.52) * mm});
            skLineSegment(sketch, "E841", {"start": v(-1905.99, 979.52) * mm, "end": v(-1508.65, 979.52) * mm});
            skArc(sketch, "E842", {"start": v(-1508.65, 979.52) * mm, "mid": v(-1500.97, 975.92) * mm, "end": v(-1498.82, 967.7) * mm});
            skArc(sketch, "E843", {"start": v(-1498.82, 967.7) * mm, "mid": v(-1512.32, 819.52) * mm, "end": v(-1498.82, 671.32) * mm});
            skArc(sketch, "E844", {"start": v(-1498.82, 671.32) * mm, "mid": v(-1500.97, 663.12) * mm, "end": v(-1508.65, 659.52) * mm});
            skLineSegment(sketch, "E845", {"start": v(-1508.65, 659.52) * mm, "end": v(-1905.99, 659.52) * mm});
            skLineSegment(sketch, "E846", {"start": v(-1905.99, 659.52) * mm, "end": v(-1905.99, 639.42) * mm});
            skLineSegment(sketch, "E847", {"start": v(-1905.99, 639.42) * mm, "end": v(-1681.43, 639.42) * mm});
            skArc(sketch, "E848", {"start": v(-1935.54, 942.23) * mm, "mid": v(-1929.88, 942.23) * mm, "end": v(-1929.88, 936.57) * mm});
            skLineSegment(sketch, "E849", {"start": v(-1929.88, 936.57) * mm, "end": v(-1929.88, 917.23) * mm});
            skLineSegment(sketch, "E850", {"start": v(-1929.88, 917.23) * mm, "end": v(-1554.68, 917.23) * mm});
            skLineSegment(sketch, "E851", {"start": v(-1554.68, 917.23) * mm, "end": v(-1554.68, 936.57) * mm});
            skArc(sketch, "E852", {"start": v(-1554.68, 936.57) * mm, "mid": v(-1554.68, 942.23) * mm, "end": v(-1549.03, 942.23) * mm});
            skLineSegment(sketch, "E853", {"start": v(-1549.03, 942.23) * mm, "end": v(-1545.14, 942.23) * mm});
            skArc(sketch, "E854", {"start": v(-1545.14, 942.23) * mm, "mid": v(-1539.48, 942.23) * mm, "end": v(-1539.48, 936.57) * mm});
            skLineSegment(sketch, "E855", {"start": v(-1539.48, 936.57) * mm, "end": v(-1539.48, 917.23) * mm});
            skLineSegment(sketch, "E856", {"start": v(-1539.48, 917.23) * mm, "end": v(-1534.78, 917.23) * mm});
            skArc(sketch, "E857", {"start": v(-1534.78, 917.23) * mm, "mid": v(-1527.71, 920.16) * mm, "end": v(-1524.78, 927.23) * mm});
            skLineSegment(sketch, "E858", {"start": v(-1524.78, 927.23) * mm, "end": v(-1524.78, 957.23) * mm});
            skArc(sketch, "E859", {"start": v(-1524.78, 957.23) * mm, "mid": v(-1527.71, 964.3) * mm, "end": v(-1534.78, 967.23) * mm});
            skLineSegment(sketch, "E860", {"start": v(-1534.78, 967.23) * mm, "end": v(-1949.78, 967.23) * mm});
            skArc(sketch, "E861", {"start": v(-1949.78, 967.23) * mm, "mid": v(-1956.85, 964.3) * mm, "end": v(-1959.78, 957.23) * mm});
            skLineSegment(sketch, "E862", {"start": v(-1959.78, 957.23) * mm, "end": v(-1959.78, 927.23) * mm});
            skArc(sketch, "E863", {"start": v(-1959.78, 927.23) * mm, "mid": v(-1956.85, 920.16) * mm, "end": v(-1949.78, 917.23) * mm});
            skLineSegment(sketch, "E864", {"start": v(-1949.78, 917.23) * mm, "end": v(-1945.08, 917.23) * mm});
            skLineSegment(sketch, "E865", {"start": v(-1945.08, 917.23) * mm, "end": v(-1945.08, 936.57) * mm});
            skArc(sketch, "E866", {"start": v(-1945.08, 936.57) * mm, "mid": v(-1945.08, 942.23) * mm, "end": v(-1939.43, 942.23) * mm});
            skLineSegment(sketch, "E867", {"start": v(-1939.43, 942.23) * mm, "end": v(-1935.54, 942.23) * mm});
            skArc(sketch, "E868", {"start": v(-2222.39, 596.27) * mm, "mid": v(-2052.48, 658.87) * mm, "end": v(-1872.97, 682.65) * mm});
            skLineSegment(sketch, "E869", {"start": v(-1872.97, 682.65) * mm, "end": v(-1848.28, 688.75) * mm});
            skArc(sketch, "E870", {"start": v(-1848.28, 688.75) * mm, "mid": v(-1842.12, 693.29) * mm, "end": v(-1840.98, 700.86) * mm});
            skLineSegment(sketch, "E871", {"start": v(-1840.98, 700.86) * mm, "end": v(-1848.17, 729.97) * mm});
            skArc(sketch, "E872", {"start": v(-1848.17, 729.97) * mm, "mid": v(-1852.71, 736.13) * mm, "end": v(-1860.28, 737.28) * mm});
            skLineSegment(sketch, "E873", {"start": v(-1860.28, 737.28) * mm, "end": v(-1870.08, 734.86) * mm});
            skLineSegment(sketch, "E874", {"start": v(-1870.08, 734.86) * mm, "end": v(-1865.44, 716.08) * mm});
            skArc(sketch, "E875", {"start": v(-1865.44, 716.08) * mm, "mid": v(-1864.09, 710.59) * mm, "end": v(-1869.58, 709.23) * mm});
            skLineSegment(sketch, "E876", {"start": v(-1869.58, 709.23) * mm, "end": v(-1873.35, 708.3) * mm});
            skArc(sketch, "E877", {"start": v(-1873.35, 708.3) * mm, "mid": v(-1878.84, 706.94) * mm, "end": v(-1880.2, 712.43) * mm});
            skLineSegment(sketch, "E878", {"start": v(-1880.2, 712.43) * mm, "end": v(-1884.84, 731.2) * mm});
            skLineSegment(sketch, "E879", {"start": v(-1884.84, 731.2) * mm, "end": v(-1899.5, 727.59) * mm});
            skArc(sketch, "E880", {"start": v(-1899.5, 727.59) * mm, "mid": v(-2063.7, 704.28) * mm, "end": v(-2219.86, 648.4) * mm});
            skLineSegment(sketch, "E881", {"start": v(-2219.86, 648.4) * mm, "end": v(-2234.52, 644.77) * mm});
            skLineSegment(sketch, "E882", {"start": v(-2234.52, 644.77) * mm, "end": v(-2229.87, 626) * mm});
            skArc(sketch, "E883", {"start": v(-2229.87, 626) * mm, "mid": v(-2228.52, 620.5) * mm, "end": v(-2234, 619.14) * mm});
            skLineSegment(sketch, "E884", {"start": v(-2234, 619.14) * mm, "end": v(-2237.78, 618.21) * mm});
            skArc(sketch, "E885", {"start": v(-2237.78, 618.21) * mm, "mid": v(-2243.27, 616.85) * mm, "end": v(-2244.63, 622.35) * mm});
            skLineSegment(sketch, "E886", {"start": v(-2244.63, 622.35) * mm, "end": v(-2249.27, 641.12) * mm});
            skLineSegment(sketch, "E887", {"start": v(-2249.27, 641.12) * mm, "end": v(-2259.08, 638.7) * mm});
            skArc(sketch, "E888", {"start": v(-2259.08, 638.7) * mm, "mid": v(-2265.24, 634.16) * mm, "end": v(-2266.38, 626.6) * mm});
            skLineSegment(sketch, "E889", {"start": v(-2266.38, 626.6) * mm, "end": v(-2259.19, 597.48) * mm});
            skArc(sketch, "E890", {"start": v(-2259.19, 597.48) * mm, "mid": v(-2254.65, 591.32) * mm, "end": v(-2247.08, 590.17) * mm});
            skLineSegment(sketch, "E891", {"start": v(-2247.08, 590.17) * mm, "end": v(-2222.39, 596.27) * mm});
            skArc(sketch, "E892", {"start": v(-1385, 1099.02) * mm, "mid": v(-1405, 1279) * mm, "end": v(-1385, 1458.96) * mm});
            skLineSegment(sketch, "E893", {"start": v(-1385, 1458.96) * mm, "end": v(-1385, 1484.4) * mm});
            skArc(sketch, "E894", {"start": v(-1385, 1484.4) * mm, "mid": v(-1387.93, 1491.46) * mm, "end": v(-1395, 1494.4) * mm});
            skLineSegment(sketch, "E895", {"start": v(-1395, 1494.4) * mm, "end": v(-1425, 1494.4) * mm});
            skArc(sketch, "E896", {"start": v(-1425, 1494.4) * mm, "mid": v(-1432.06, 1491.46) * mm, "end": v(-1435, 1484.4) * mm});
            skLineSegment(sketch, "E897", {"start": v(-1435, 1484.4) * mm, "end": v(-1435, 1474.3) * mm});
            skLineSegment(sketch, "E898", {"start": v(-1435, 1474.3) * mm, "end": v(-1415.65, 1474.3) * mm});
            skArc(sketch, "E899", {"start": v(-1415.65, 1474.3) * mm, "mid": v(-1410, 1474.3) * mm, "end": v(-1410, 1468.63) * mm});
            skLineSegment(sketch, "E900", {"start": v(-1410, 1468.63) * mm, "end": v(-1410, 1464.75) * mm});
            skArc(sketch, "E901", {"start": v(-1410, 1464.75) * mm, "mid": v(-1410, 1459.1) * mm, "end": v(-1415.65, 1459.1) * mm});
            skLineSegment(sketch, "E902", {"start": v(-1415.65, 1459.1) * mm, "end": v(-1435, 1459.1) * mm});
            skLineSegment(sketch, "E903", {"start": v(-1435, 1459.1) * mm, "end": v(-1435, 1444) * mm});
            skArc(sketch, "E904", {"start": v(-1435, 1444) * mm, "mid": v(-1451.77, 1279) * mm, "end": v(-1435, 1114) * mm});
            skLineSegment(sketch, "E905", {"start": v(-1435, 1114) * mm, "end": v(-1435, 1098.9) * mm});
            skLineSegment(sketch, "E906", {"start": v(-1435, 1098.9) * mm, "end": v(-1415.65, 1098.9) * mm});
            skArc(sketch, "E907", {"start": v(-1415.65, 1098.9) * mm, "mid": v(-1410, 1098.9) * mm, "end": v(-1410, 1093.23) * mm});
            skLineSegment(sketch, "E908", {"start": v(-1410, 1093.23) * mm, "end": v(-1410, 1089.35) * mm});
            skArc(sketch, "E909", {"start": v(-1410, 1089.35) * mm, "mid": v(-1410, 1083.7) * mm, "end": v(-1415.65, 1083.7) * mm});
            skLineSegment(sketch, "E910", {"start": v(-1415.65, 1083.7) * mm, "end": v(-1435, 1083.7) * mm});
            skLineSegment(sketch, "E911", {"start": v(-1435, 1083.7) * mm, "end": v(-1435, 1073.6) * mm});
            skArc(sketch, "E912", {"start": v(-1435, 1073.6) * mm, "mid": v(-1432.06, 1066.52) * mm, "end": v(-1425, 1063.6) * mm});
            skLineSegment(sketch, "E913", {"start": v(-1425, 1063.6) * mm, "end": v(-1395, 1063.6) * mm});
            skArc(sketch, "E914", {"start": v(-1395, 1063.6) * mm, "mid": v(-1387.93, 1066.52) * mm, "end": v(-1385, 1073.6) * mm});
            skLineSegment(sketch, "E915", {"start": v(-1385, 1073.6) * mm, "end": v(-1385, 1099.02) * mm});
            skArc(sketch, "E916", {"start": v(-2159.63, 928.58) * mm, "mid": v(-2339.6, 908.58) * mm, "end": v(-2519.57, 928.58) * mm});
            skLineSegment(sketch, "E917", {"start": v(-2519.57, 928.58) * mm, "end": v(-2545, 928.58) * mm});
            skArc(sketch, "E918", {"start": v(-2545, 928.58) * mm, "mid": v(-2552.07, 925.65) * mm, "end": v(-2555, 918.58) * mm});
            skLineSegment(sketch, "E919", {"start": v(-2555, 918.58) * mm, "end": v(-2555, 888.58) * mm});
            skArc(sketch, "E920", {"start": v(-2555, 888.58) * mm, "mid": v(-2552.07, 881.51) * mm, "end": v(-2545, 878.58) * mm});
            skLineSegment(sketch, "E921", {"start": v(-2545, 878.58) * mm, "end": v(-2534.9, 878.58) * mm});
            skLineSegment(sketch, "E922", {"start": v(-2534.9, 878.58) * mm, "end": v(-2534.9, 897.93) * mm});
            skArc(sketch, "E923", {"start": v(-2534.9, 897.93) * mm, "mid": v(-2534.9, 903.58) * mm, "end": v(-2529.24, 903.58) * mm});
            skLineSegment(sketch, "E924", {"start": v(-2529.24, 903.58) * mm, "end": v(-2525.36, 903.58) * mm});
            skArc(sketch, "E925", {"start": v(-2525.36, 903.58) * mm, "mid": v(-2519.7, 903.58) * mm, "end": v(-2519.7, 897.93) * mm});
            skLineSegment(sketch, "E926", {"start": v(-2519.7, 897.93) * mm, "end": v(-2519.7, 878.58) * mm});
            skLineSegment(sketch, "E927", {"start": v(-2519.7, 878.58) * mm, "end": v(-2504.6, 878.58) * mm});
            skArc(sketch, "E928", {"start": v(-2504.6, 878.58) * mm, "mid": v(-2339.6, 861.8) * mm, "end": v(-2174.6, 878.58) * mm});
            skLineSegment(sketch, "E929", {"start": v(-2174.6, 878.58) * mm, "end": v(-2159.5, 878.58) * mm});
            skLineSegment(sketch, "E930", {"start": v(-2159.5, 878.58) * mm, "end": v(-2159.5, 897.93) * mm});
            skArc(sketch, "E931", {"start": v(-2159.5, 897.93) * mm, "mid": v(-2159.5, 903.58) * mm, "end": v(-2153.84, 903.58) * mm});
            skLineSegment(sketch, "E932", {"start": v(-2153.84, 903.58) * mm, "end": v(-2149.96, 903.58) * mm});
            skArc(sketch, "E933", {"start": v(-2149.96, 903.58) * mm, "mid": v(-2144.3, 903.58) * mm, "end": v(-2144.3, 897.93) * mm});
            skLineSegment(sketch, "E934", {"start": v(-2144.3, 897.93) * mm, "end": v(-2144.3, 878.58) * mm});
            skLineSegment(sketch, "E935", {"start": v(-2144.3, 878.58) * mm, "end": v(-2134.2, 878.58) * mm});
            skArc(sketch, "E936", {"start": v(-2134.2, 878.58) * mm, "mid": v(-2127.13, 881.51) * mm, "end": v(-2124.2, 888.58) * mm});
            skLineSegment(sketch, "E937", {"start": v(-2124.2, 888.58) * mm, "end": v(-2124.2, 918.58) * mm});
            skArc(sketch, "E938", {"start": v(-2124.2, 918.58) * mm, "mid": v(-2127.13, 925.65) * mm, "end": v(-2134.2, 928.58) * mm});
            skLineSegment(sketch, "E939", {"start": v(-2134.2, 928.58) * mm, "end": v(-2159.63, 928.58) * mm});
            skArc(sketch, "E940", {"start": v(-2159.63, 863.04) * mm, "mid": v(-2339.6, 843.04) * mm, "end": v(-2519.57, 863.04) * mm});
            skLineSegment(sketch, "E941", {"start": v(-2519.57, 863.04) * mm, "end": v(-2545, 863.04) * mm});
            skArc(sketch, "E942", {"start": v(-2545, 863.04) * mm, "mid": v(-2552.07, 860.12) * mm, "end": v(-2555, 853.04) * mm});
            skLineSegment(sketch, "E943", {"start": v(-2555, 853.04) * mm, "end": v(-2555, 823.05) * mm});
            skArc(sketch, "E944", {"start": v(-2555, 823.05) * mm, "mid": v(-2552.07, 815.98) * mm, "end": v(-2545, 813.05) * mm});
            skLineSegment(sketch, "E945", {"start": v(-2545, 813.05) * mm, "end": v(-2534.9, 813.05) * mm});
            skLineSegment(sketch, "E946", {"start": v(-2534.9, 813.05) * mm, "end": v(-2534.9, 832.4) * mm});
            skArc(sketch, "E947", {"start": v(-2534.9, 832.4) * mm, "mid": v(-2534.9, 838.05) * mm, "end": v(-2529.24, 838.05) * mm});
            skLineSegment(sketch, "E948", {"start": v(-2529.24, 838.05) * mm, "end": v(-2525.36, 838.05) * mm});
            skArc(sketch, "E949", {"start": v(-2525.36, 838.05) * mm, "mid": v(-2519.7, 838.05) * mm, "end": v(-2519.7, 832.4) * mm});
            skLineSegment(sketch, "E950", {"start": v(-2519.7, 832.4) * mm, "end": v(-2519.7, 813.05) * mm});
            skLineSegment(sketch, "E951", {"start": v(-2519.7, 813.05) * mm, "end": v(-2504.6, 813.05) * mm});
            skArc(sketch, "E952", {"start": v(-2504.6, 813.05) * mm, "mid": v(-2339.6, 796.27) * mm, "end": v(-2174.6, 813.05) * mm});
            skLineSegment(sketch, "E953", {"start": v(-2174.6, 813.05) * mm, "end": v(-2159.5, 813.05) * mm});
            skLineSegment(sketch, "E954", {"start": v(-2159.5, 813.05) * mm, "end": v(-2159.5, 832.4) * mm});
            skArc(sketch, "E955", {"start": v(-2159.5, 832.4) * mm, "mid": v(-2159.5, 838.05) * mm, "end": v(-2153.84, 838.05) * mm});
            skLineSegment(sketch, "E956", {"start": v(-2153.84, 838.05) * mm, "end": v(-2149.96, 838.05) * mm});
            skArc(sketch, "E957", {"start": v(-2149.96, 838.05) * mm, "mid": v(-2144.3, 838.05) * mm, "end": v(-2144.3, 832.4) * mm});
            skLineSegment(sketch, "E958", {"start": v(-2144.3, 832.4) * mm, "end": v(-2144.3, 813.05) * mm});
            skLineSegment(sketch, "E959", {"start": v(-2144.3, 813.05) * mm, "end": v(-2134.2, 813.05) * mm});
            skArc(sketch, "E960", {"start": v(-2134.2, 813.05) * mm, "mid": v(-2127.13, 815.98) * mm, "end": v(-2124.2, 823.05) * mm});
            skLineSegment(sketch, "E961", {"start": v(-2124.2, 823.05) * mm, "end": v(-2124.2, 853.04) * mm});
            skArc(sketch, "E962", {"start": v(-2124.2, 853.04) * mm, "mid": v(-2127.13, 860.12) * mm, "end": v(-2134.2, 863.04) * mm});
            skLineSegment(sketch, "E963", {"start": v(-2134.2, 863.04) * mm, "end": v(-2159.63, 863.04) * mm});
            skArc(sketch, "E964", {"start": v(-1866.53, 1051) * mm, "mid": v(-1686.56, 1071) * mm, "end": v(-1506.6, 1051) * mm});
            skLineSegment(sketch, "E965", {"start": v(-1506.6, 1051) * mm, "end": v(-1481.16, 1051) * mm});
            skArc(sketch, "E966", {"start": v(-1481.16, 1051) * mm, "mid": v(-1474.09, 1053.92) * mm, "end": v(-1471.16, 1061) * mm});
            skLineSegment(sketch, "E967", {"start": v(-1471.16, 1061) * mm, "end": v(-1471.16, 1090.98) * mm});
            skArc(sketch, "E968", {"start": v(-1471.16, 1090.98) * mm, "mid": v(-1474.09, 1098.05) * mm, "end": v(-1481.16, 1100.98) * mm});
            skLineSegment(sketch, "E969", {"start": v(-1481.16, 1100.98) * mm, "end": v(-1491.26, 1100.98) * mm});
            skLineSegment(sketch, "E970", {"start": v(-1491.26, 1100.98) * mm, "end": v(-1491.26, 1081.64) * mm});
            skArc(sketch, "E971", {"start": v(-1491.26, 1081.64) * mm, "mid": v(-1491.26, 1075.98) * mm, "end": v(-1496.92, 1075.98) * mm});
            skLineSegment(sketch, "E972", {"start": v(-1496.92, 1075.98) * mm, "end": v(-1500.8, 1075.98) * mm});
            skArc(sketch, "E973", {"start": v(-1500.8, 1075.98) * mm, "mid": v(-1506.46, 1075.98) * mm, "end": v(-1506.46, 1081.64) * mm});
            skLineSegment(sketch, "E974", {"start": v(-1506.46, 1081.64) * mm, "end": v(-1506.46, 1100.98) * mm});
            skLineSegment(sketch, "E975", {"start": v(-1506.46, 1100.98) * mm, "end": v(-1521.56, 1100.98) * mm});
            skArc(sketch, "E976", {"start": v(-1521.56, 1100.98) * mm, "mid": v(-1686.56, 1117.76) * mm, "end": v(-1851.56, 1100.98) * mm});
            skLineSegment(sketch, "E977", {"start": v(-1851.56, 1100.98) * mm, "end": v(-1866.66, 1100.98) * mm});
            skLineSegment(sketch, "E978", {"start": v(-1866.66, 1100.98) * mm, "end": v(-1866.66, 1081.64) * mm});
            skArc(sketch, "E979", {"start": v(-1866.66, 1081.64) * mm, "mid": v(-1866.66, 1075.98) * mm, "end": v(-1872.32, 1075.98) * mm});
            skLineSegment(sketch, "E980", {"start": v(-1872.32, 1075.98) * mm, "end": v(-1876.2, 1075.98) * mm});
            skArc(sketch, "E981", {"start": v(-1876.2, 1075.98) * mm, "mid": v(-1881.86, 1075.98) * mm, "end": v(-1881.86, 1081.64) * mm});
            skLineSegment(sketch, "E982", {"start": v(-1881.86, 1081.64) * mm, "end": v(-1881.86, 1100.98) * mm});
            skLineSegment(sketch, "E983", {"start": v(-1881.86, 1100.98) * mm, "end": v(-1891.96, 1100.98) * mm});
            skArc(sketch, "E984", {"start": v(-1891.96, 1100.98) * mm, "mid": v(-1899.03, 1098.05) * mm, "end": v(-1901.96, 1090.98) * mm});
            skLineSegment(sketch, "E985", {"start": v(-1901.96, 1090.98) * mm, "end": v(-1901.96, 1061) * mm});
            skArc(sketch, "E986", {"start": v(-1901.96, 1061) * mm, "mid": v(-1899.03, 1053.92) * mm, "end": v(-1891.96, 1051) * mm});
            skLineSegment(sketch, "E987", {"start": v(-1891.96, 1051) * mm, "end": v(-1866.53, 1051) * mm});
            skArc(sketch, "E988", {"start": v(-1866.53, 1116.52) * mm, "mid": v(-1686.56, 1136.52) * mm, "end": v(-1506.6, 1116.52) * mm});
            skLineSegment(sketch, "E989", {"start": v(-1506.6, 1116.52) * mm, "end": v(-1481.16, 1116.52) * mm});
            skArc(sketch, "E990", {"start": v(-1481.16, 1116.52) * mm, "mid": v(-1474.09, 1119.45) * mm, "end": v(-1471.16, 1126.52) * mm});
            skLineSegment(sketch, "E991", {"start": v(-1471.16, 1126.52) * mm, "end": v(-1471.16, 1156.51) * mm});
            skArc(sketch, "E992", {"start": v(-1471.16, 1156.51) * mm, "mid": v(-1474.09, 1163.59) * mm, "end": v(-1481.16, 1166.51) * mm});
            skLineSegment(sketch, "E993", {"start": v(-1481.16, 1166.51) * mm, "end": v(-1491.26, 1166.51) * mm});
            skLineSegment(sketch, "E994", {"start": v(-1491.26, 1166.51) * mm, "end": v(-1491.26, 1147.17) * mm});
            skArc(sketch, "E995", {"start": v(-1491.26, 1147.17) * mm, "mid": v(-1491.26, 1141.51) * mm, "end": v(-1496.92, 1141.51) * mm});
            skLineSegment(sketch, "E996", {"start": v(-1496.92, 1141.51) * mm, "end": v(-1500.8, 1141.51) * mm});
            skArc(sketch, "E997", {"start": v(-1500.8, 1141.51) * mm, "mid": v(-1506.46, 1141.51) * mm, "end": v(-1506.46, 1147.17) * mm});
            skLineSegment(sketch, "E998", {"start": v(-1506.46, 1147.17) * mm, "end": v(-1506.46, 1166.51) * mm});
            skLineSegment(sketch, "E999", {"start": v(-1506.46, 1166.51) * mm, "end": v(-1521.56, 1166.51) * mm});
            skArc(sketch, "E1000", {"start": v(-1521.56, 1166.51) * mm, "mid": v(-1686.56, 1183.3) * mm, "end": v(-1851.56, 1166.51) * mm});
            skLineSegment(sketch, "E1001", {"start": v(-1851.56, 1166.51) * mm, "end": v(-1866.66, 1166.51) * mm});
            skLineSegment(sketch, "E1002", {"start": v(-1866.66, 1166.51) * mm, "end": v(-1866.66, 1147.17) * mm});
            skArc(sketch, "E1003", {"start": v(-1866.66, 1147.17) * mm, "mid": v(-1866.66, 1141.51) * mm, "end": v(-1872.32, 1141.51) * mm});
            skLineSegment(sketch, "E1004", {"start": v(-1872.32, 1141.51) * mm, "end": v(-1876.2, 1141.51) * mm});
            skArc(sketch, "E1005", {"start": v(-1876.2, 1141.51) * mm, "mid": v(-1881.86, 1141.51) * mm, "end": v(-1881.86, 1147.17) * mm});
            skLineSegment(sketch, "E1006", {"start": v(-1881.86, 1147.17) * mm, "end": v(-1881.86, 1166.51) * mm});
            skLineSegment(sketch, "E1007", {"start": v(-1881.86, 1166.51) * mm, "end": v(-1891.96, 1166.51) * mm});
            skArc(sketch, "E1008", {"start": v(-1891.96, 1166.51) * mm, "mid": v(-1899.03, 1163.59) * mm, "end": v(-1901.96, 1156.51) * mm});
            skLineSegment(sketch, "E1009", {"start": v(-1901.96, 1156.51) * mm, "end": v(-1901.96, 1126.52) * mm});
            skArc(sketch, "E1010", {"start": v(-1901.96, 1126.52) * mm, "mid": v(-1899.03, 1119.45) * mm, "end": v(-1891.96, 1116.52) * mm});
            skLineSegment(sketch, "E1011", {"start": v(-1891.96, 1116.52) * mm, "end": v(-1866.53, 1116.52) * mm});
            skLineSegment(sketch, "E1012", {"start": v(-1683.67, 1478.64) * mm, "end": v(-1658.98, 1484.74) * mm});
            skArc(sketch, "E1013", {"start": v(-1658.98, 1484.74) * mm, "mid": v(-1652.82, 1489.28) * mm, "end": v(-1651.67, 1496.85) * mm});
            skLineSegment(sketch, "E1014", {"start": v(-1651.67, 1496.85) * mm, "end": v(-1658.87, 1525.96) * mm});
            skArc(sketch, "E1015", {"start": v(-1658.87, 1525.96) * mm, "mid": v(-1663.41, 1532.13) * mm, "end": v(-1670.98, 1533.27) * mm});
            skLineSegment(sketch, "E1016", {"start": v(-1670.98, 1533.27) * mm, "end": v(-1680.78, 1530.85) * mm});
            skLineSegment(sketch, "E1017", {"start": v(-1680.78, 1530.85) * mm, "end": v(-1676.14, 1512.07) * mm});
            skArc(sketch, "E1018", {"start": v(-1676.14, 1512.07) * mm, "mid": v(-1674.78, 1506.58) * mm, "end": v(-1680.27, 1505.22) * mm});
            skLineSegment(sketch, "E1019", {"start": v(-1680.27, 1505.22) * mm, "end": v(-1684.05, 1504.29) * mm});
            skArc(sketch, "E1020", {"start": v(-1684.05, 1504.29) * mm, "mid": v(-1689.54, 1502.93) * mm, "end": v(-1690.9, 1508.42) * mm});
            skLineSegment(sketch, "E1021", {"start": v(-1690.9, 1508.42) * mm, "end": v(-1695.54, 1527.2) * mm});
            skLineSegment(sketch, "E1022", {"start": v(-1695.54, 1527.2) * mm, "end": v(-1710.2, 1523.58) * mm});
            skArc(sketch, "E1023", {"start": v(-1710.2, 1523.58) * mm, "mid": v(-1874.4, 1500.27) * mm, "end": v(-2030.55, 1444.39) * mm});
            skLineSegment(sketch, "E1024", {"start": v(-2030.55, 1444.39) * mm, "end": v(-2045.21, 1440.76) * mm});
            skLineSegment(sketch, "E1025", {"start": v(-2045.21, 1440.76) * mm, "end": v(-2040.57, 1421.99) * mm});
            skArc(sketch, "E1026", {"start": v(-2040.57, 1421.99) * mm, "mid": v(-2039.21, 1416.5) * mm, "end": v(-2044.7, 1415.14) * mm});
            skLineSegment(sketch, "E1027", {"start": v(-2044.7, 1415.14) * mm, "end": v(-2048.48, 1414.2) * mm});
            skArc(sketch, "E1028", {"start": v(-2048.48, 1414.2) * mm, "mid": v(-2053.97, 1412.85) * mm, "end": v(-2055.33, 1418.34) * mm});
            skLineSegment(sketch, "E1029", {"start": v(-2055.33, 1418.34) * mm, "end": v(-2059.97, 1437.12) * mm});
            skLineSegment(sketch, "E1030", {"start": v(-2059.97, 1437.12) * mm, "end": v(-2069.77, 1434.7) * mm});
            skArc(sketch, "E1031", {"start": v(-2069.77, 1434.7) * mm, "mid": v(-2075.94, 1430.15) * mm, "end": v(-2077.08, 1422.58) * mm});
            skLineSegment(sketch, "E1032", {"start": v(-2077.08, 1422.58) * mm, "end": v(-2069.88, 1393.47) * mm});
            skArc(sketch, "E1033", {"start": v(-2069.88, 1393.47) * mm, "mid": v(-2065.34, 1387.3) * mm, "end": v(-2057.78, 1386.16) * mm});
            skLineSegment(sketch, "E1034", {"start": v(-2057.78, 1386.16) * mm, "end": v(-2033.09, 1392.26) * mm});
            skArc(sketch, "E1035", {"start": v(-2033.09, 1392.26) * mm, "mid": v(-1863.18, 1454.87) * mm, "end": v(-1683.67, 1478.64) * mm});
            skLineSegment(sketch, "E1036", {"start": v(-2135.13, 1458.9) * mm, "end": v(-2109.7, 1458.9) * mm});
            skArc(sketch, "E1037", {"start": v(-2109.7, 1458.9) * mm, "mid": v(-2102.63, 1461.83) * mm, "end": v(-2099.7, 1468.9) * mm});
            skLineSegment(sketch, "E1038", {"start": v(-2099.7, 1468.9) * mm, "end": v(-2099.7, 1498.9) * mm});
            skArc(sketch, "E1039", {"start": v(-2099.7, 1498.9) * mm, "mid": v(-2102.63, 1505.97) * mm, "end": v(-2109.7, 1508.9) * mm});
            skLineSegment(sketch, "E1040", {"start": v(-2109.7, 1508.9) * mm, "end": v(-2119.8, 1508.9) * mm});
            skLineSegment(sketch, "E1041", {"start": v(-2119.8, 1508.9) * mm, "end": v(-2119.8, 1489.55) * mm});
            skArc(sketch, "E1042", {"start": v(-2119.8, 1489.55) * mm, "mid": v(-2119.8, 1483.9) * mm, "end": v(-2125.45, 1483.9) * mm});
            skLineSegment(sketch, "E1043", {"start": v(-2125.45, 1483.9) * mm, "end": v(-2129.34, 1483.9) * mm});
            skArc(sketch, "E1044", {"start": v(-2129.34, 1483.9) * mm, "mid": v(-2135, 1483.9) * mm, "end": v(-2135, 1489.55) * mm});
            skLineSegment(sketch, "E1045", {"start": v(-2135, 1489.55) * mm, "end": v(-2135, 1508.9) * mm});
            skLineSegment(sketch, "E1046", {"start": v(-2135, 1508.9) * mm, "end": v(-2150.1, 1508.9) * mm});
            skArc(sketch, "E1047", {"start": v(-2150.1, 1508.9) * mm, "mid": v(-2315.1, 1525.67) * mm, "end": v(-2480.1, 1508.9) * mm});
            skLineSegment(sketch, "E1048", {"start": v(-2480.1, 1508.9) * mm, "end": v(-2495.2, 1508.9) * mm});
            skLineSegment(sketch, "E1049", {"start": v(-2495.2, 1508.9) * mm, "end": v(-2495.2, 1489.55) * mm});
            skArc(sketch, "E1050", {"start": v(-2495.2, 1489.55) * mm, "mid": v(-2495.2, 1483.9) * mm, "end": v(-2500.85, 1483.9) * mm});
            skLineSegment(sketch, "E1051", {"start": v(-2500.85, 1483.9) * mm, "end": v(-2504.74, 1483.9) * mm});
            skArc(sketch, "E1052", {"start": v(-2504.74, 1483.9) * mm, "mid": v(-2510.4, 1483.9) * mm, "end": v(-2510.4, 1489.55) * mm});
            skLineSegment(sketch, "E1053", {"start": v(-2510.4, 1489.55) * mm, "end": v(-2510.4, 1508.9) * mm});
            skLineSegment(sketch, "E1054", {"start": v(-2510.4, 1508.9) * mm, "end": v(-2520.5, 1508.9) * mm});
            skArc(sketch, "E1055", {"start": v(-2520.5, 1508.9) * mm, "mid": v(-2527.57, 1505.97) * mm, "end": v(-2530.5, 1498.9) * mm});
            skLineSegment(sketch, "E1056", {"start": v(-2530.5, 1498.9) * mm, "end": v(-2530.5, 1468.9) * mm});
            skArc(sketch, "E1057", {"start": v(-2530.5, 1468.9) * mm, "mid": v(-2527.57, 1461.83) * mm, "end": v(-2520.5, 1458.9) * mm});
            skLineSegment(sketch, "E1058", {"start": v(-2520.5, 1458.9) * mm, "end": v(-2495.06, 1458.9) * mm});
            skArc(sketch, "E1059", {"start": v(-2495.06, 1458.9) * mm, "mid": v(-2315.1, 1478.9) * mm, "end": v(-2135.13, 1458.9) * mm});
            skLineSegment(sketch, "E1060", {"start": v(-2135.13, 1393.37) * mm, "end": v(-2109.7, 1393.37) * mm});
            skArc(sketch, "E1061", {"start": v(-2109.7, 1393.37) * mm, "mid": v(-2102.63, 1396.3) * mm, "end": v(-2099.7, 1403.37) * mm});
            skLineSegment(sketch, "E1062", {"start": v(-2099.7, 1403.37) * mm, "end": v(-2099.7, 1433.36) * mm});
            skArc(sketch, "E1063", {"start": v(-2099.7, 1433.36) * mm, "mid": v(-2102.63, 1440.44) * mm, "end": v(-2109.7, 1443.36) * mm});
            skLineSegment(sketch, "E1064", {"start": v(-2109.7, 1443.36) * mm, "end": v(-2119.8, 1443.36) * mm});
            skLineSegment(sketch, "E1065", {"start": v(-2119.8, 1443.36) * mm, "end": v(-2119.8, 1424.02) * mm});
            skArc(sketch, "E1066", {"start": v(-2119.8, 1424.02) * mm, "mid": v(-2119.8, 1418.36) * mm, "end": v(-2125.45, 1418.36) * mm});
            skLineSegment(sketch, "E1067", {"start": v(-2125.45, 1418.36) * mm, "end": v(-2129.34, 1418.36) * mm});
            skArc(sketch, "E1068", {"start": v(-2129.34, 1418.36) * mm, "mid": v(-2135, 1418.36) * mm, "end": v(-2135, 1424.02) * mm});
            skLineSegment(sketch, "E1069", {"start": v(-2135, 1424.02) * mm, "end": v(-2135, 1443.36) * mm});
            skLineSegment(sketch, "E1070", {"start": v(-2135, 1443.36) * mm, "end": v(-2150.1, 1443.36) * mm});
            skArc(sketch, "E1071", {"start": v(-2150.1, 1443.36) * mm, "mid": v(-2315.1, 1460.14) * mm, "end": v(-2480.1, 1443.36) * mm});
            skLineSegment(sketch, "E1072", {"start": v(-2480.1, 1443.36) * mm, "end": v(-2495.2, 1443.36) * mm});
            skLineSegment(sketch, "E1073", {"start": v(-2495.2, 1443.36) * mm, "end": v(-2495.2, 1424.02) * mm});
            skArc(sketch, "E1074", {"start": v(-2495.2, 1424.02) * mm, "mid": v(-2495.2, 1418.36) * mm, "end": v(-2500.85, 1418.36) * mm});
            skLineSegment(sketch, "E1075", {"start": v(-2500.85, 1418.36) * mm, "end": v(-2504.74, 1418.36) * mm});
            skArc(sketch, "E1076", {"start": v(-2504.74, 1418.36) * mm, "mid": v(-2510.4, 1418.36) * mm, "end": v(-2510.4, 1424.02) * mm});
            skLineSegment(sketch, "E1077", {"start": v(-2510.4, 1424.02) * mm, "end": v(-2510.4, 1443.36) * mm});
            skLineSegment(sketch, "E1078", {"start": v(-2510.4, 1443.36) * mm, "end": v(-2520.5, 1443.36) * mm});
            skArc(sketch, "E1079", {"start": v(-2520.5, 1443.36) * mm, "mid": v(-2527.57, 1440.44) * mm, "end": v(-2530.5, 1433.36) * mm});
            skLineSegment(sketch, "E1080", {"start": v(-2530.5, 1433.36) * mm, "end": v(-2530.5, 1403.37) * mm});
            skArc(sketch, "E1081", {"start": v(-2530.5, 1403.37) * mm, "mid": v(-2527.57, 1396.3) * mm, "end": v(-2520.5, 1393.37) * mm});
            skLineSegment(sketch, "E1082", {"start": v(-2520.5, 1393.37) * mm, "end": v(-2495.06, 1393.37) * mm});
            skArc(sketch, "E1083", {"start": v(-2495.06, 1393.37) * mm, "mid": v(-2315.1, 1413.37) * mm, "end": v(-2135.13, 1393.37) * mm});
            skArc(sketch, "E1084", {"start": v(-1866.53, 1247.59) * mm, "mid": v(-1686.56, 1267.59) * mm, "end": v(-1506.6, 1247.59) * mm});
            skLineSegment(sketch, "E1085", {"start": v(-1506.6, 1247.59) * mm, "end": v(-1481.16, 1247.59) * mm});
            skArc(sketch, "E1086", {"start": v(-1481.16, 1247.59) * mm, "mid": v(-1474.09, 1250.51) * mm, "end": v(-1471.16, 1257.59) * mm});
            skLineSegment(sketch, "E1087", {"start": v(-1471.16, 1257.59) * mm, "end": v(-1471.16, 1287.58) * mm});
            skArc(sketch, "E1088", {"start": v(-1471.16, 1287.58) * mm, "mid": v(-1474.09, 1294.65) * mm, "end": v(-1481.16, 1297.58) * mm});
            skLineSegment(sketch, "E1089", {"start": v(-1481.16, 1297.58) * mm, "end": v(-1491.26, 1297.58) * mm});
            skLineSegment(sketch, "E1090", {"start": v(-1491.26, 1297.58) * mm, "end": v(-1491.26, 1278.24) * mm});
            skArc(sketch, "E1091", {"start": v(-1491.26, 1278.24) * mm, "mid": v(-1491.26, 1272.58) * mm, "end": v(-1496.92, 1272.58) * mm});
            skLineSegment(sketch, "E1092", {"start": v(-1496.92, 1272.58) * mm, "end": v(-1500.8, 1272.58) * mm});
            skArc(sketch, "E1093", {"start": v(-1500.8, 1272.58) * mm, "mid": v(-1506.46, 1272.58) * mm, "end": v(-1506.46, 1278.24) * mm});
            skLineSegment(sketch, "E1094", {"start": v(-1506.46, 1278.24) * mm, "end": v(-1506.46, 1297.58) * mm});
            skLineSegment(sketch, "E1095", {"start": v(-1506.46, 1297.58) * mm, "end": v(-1521.56, 1297.58) * mm});
            skArc(sketch, "E1096", {"start": v(-1521.56, 1297.58) * mm, "mid": v(-1686.56, 1314.36) * mm, "end": v(-1851.56, 1297.58) * mm});
            skLineSegment(sketch, "E1097", {"start": v(-1851.56, 1297.58) * mm, "end": v(-1866.66, 1297.58) * mm});
            skLineSegment(sketch, "E1098", {"start": v(-1866.66, 1297.58) * mm, "end": v(-1866.66, 1278.24) * mm});
            skArc(sketch, "E1099", {"start": v(-1866.66, 1278.24) * mm, "mid": v(-1866.66, 1272.58) * mm, "end": v(-1872.32, 1272.58) * mm});
            skLineSegment(sketch, "E1100", {"start": v(-1872.32, 1272.58) * mm, "end": v(-1876.2, 1272.58) * mm});
            skArc(sketch, "E1101", {"start": v(-1876.2, 1272.58) * mm, "mid": v(-1881.86, 1272.58) * mm, "end": v(-1881.86, 1278.24) * mm});
            skLineSegment(sketch, "E1102", {"start": v(-1881.86, 1278.24) * mm, "end": v(-1881.86, 1297.58) * mm});
            skLineSegment(sketch, "E1103", {"start": v(-1881.86, 1297.58) * mm, "end": v(-1891.96, 1297.58) * mm});
            skArc(sketch, "E1104", {"start": v(-1891.96, 1297.58) * mm, "mid": v(-1899.03, 1294.65) * mm, "end": v(-1901.96, 1287.58) * mm});
            skLineSegment(sketch, "E1105", {"start": v(-1901.96, 1287.58) * mm, "end": v(-1901.96, 1257.59) * mm});
            skArc(sketch, "E1106", {"start": v(-1901.96, 1257.59) * mm, "mid": v(-1899.03, 1250.51) * mm, "end": v(-1891.96, 1247.59) * mm});
            skLineSegment(sketch, "E1107", {"start": v(-1891.96, 1247.59) * mm, "end": v(-1866.53, 1247.59) * mm});
            skArc(sketch, "E1108", {"start": v(-1866.53, 1182.05) * mm, "mid": v(-1686.56, 1202.05) * mm, "end": v(-1506.6, 1182.05) * mm});
            skLineSegment(sketch, "E1109", {"start": v(-1506.6, 1182.05) * mm, "end": v(-1481.16, 1182.05) * mm});
            skArc(sketch, "E1110", {"start": v(-1481.16, 1182.05) * mm, "mid": v(-1474.09, 1184.98) * mm, "end": v(-1471.16, 1192.05) * mm});
            skLineSegment(sketch, "E1111", {"start": v(-1471.16, 1192.05) * mm, "end": v(-1471.16, 1222.05) * mm});
            skArc(sketch, "E1112", {"start": v(-1471.16, 1222.05) * mm, "mid": v(-1474.09, 1229.12) * mm, "end": v(-1481.16, 1232.05) * mm});
            skLineSegment(sketch, "E1113", {"start": v(-1481.16, 1232.05) * mm, "end": v(-1491.26, 1232.05) * mm});
            skLineSegment(sketch, "E1114", {"start": v(-1491.26, 1232.05) * mm, "end": v(-1491.26, 1212.7) * mm});
            skArc(sketch, "E1115", {"start": v(-1491.26, 1212.7) * mm, "mid": v(-1491.26, 1207.05) * mm, "end": v(-1496.92, 1207.05) * mm});
            skLineSegment(sketch, "E1116", {"start": v(-1496.92, 1207.05) * mm, "end": v(-1500.8, 1207.05) * mm});
            skArc(sketch, "E1117", {"start": v(-1500.8, 1207.05) * mm, "mid": v(-1506.46, 1207.05) * mm, "end": v(-1506.46, 1212.7) * mm});
            skLineSegment(sketch, "E1118", {"start": v(-1506.46, 1212.7) * mm, "end": v(-1506.46, 1232.05) * mm});
            skLineSegment(sketch, "E1119", {"start": v(-1506.46, 1232.05) * mm, "end": v(-1521.56, 1232.05) * mm});
            skArc(sketch, "E1120", {"start": v(-1521.56, 1232.05) * mm, "mid": v(-1686.56, 1248.83) * mm, "end": v(-1851.56, 1232.05) * mm});
            skLineSegment(sketch, "E1121", {"start": v(-1851.56, 1232.05) * mm, "end": v(-1866.66, 1232.05) * mm});
            skLineSegment(sketch, "E1122", {"start": v(-1866.66, 1232.05) * mm, "end": v(-1866.66, 1212.7) * mm});
            skArc(sketch, "E1123", {"start": v(-1866.66, 1212.7) * mm, "mid": v(-1866.66, 1207.05) * mm, "end": v(-1872.32, 1207.05) * mm});
            skLineSegment(sketch, "E1124", {"start": v(-1872.32, 1207.05) * mm, "end": v(-1876.2, 1207.05) * mm});
            skArc(sketch, "E1125", {"start": v(-1876.2, 1207.05) * mm, "mid": v(-1881.86, 1207.05) * mm, "end": v(-1881.86, 1212.7) * mm});
            skLineSegment(sketch, "E1126", {"start": v(-1881.86, 1212.7) * mm, "end": v(-1881.86, 1232.05) * mm});
            skLineSegment(sketch, "E1127", {"start": v(-1881.86, 1232.05) * mm, "end": v(-1891.96, 1232.05) * mm});
            skArc(sketch, "E1128", {"start": v(-1891.96, 1232.05) * mm, "mid": v(-1899.03, 1229.12) * mm, "end": v(-1901.96, 1222.05) * mm});
            skLineSegment(sketch, "E1129", {"start": v(-1901.96, 1222.05) * mm, "end": v(-1901.96, 1192.05) * mm});
            skArc(sketch, "E1130", {"start": v(-1901.96, 1192.05) * mm, "mid": v(-1899.03, 1184.98) * mm, "end": v(-1891.96, 1182.05) * mm});
            skLineSegment(sketch, "E1131", {"start": v(-1891.96, 1182.05) * mm, "end": v(-1866.53, 1182.05) * mm});
            skArc(sketch, "E1132", {"start": v(-2159.63, 1059.64) * mm, "mid": v(-2339.6, 1039.64) * mm, "end": v(-2519.57, 1059.64) * mm});
            skLineSegment(sketch, "E1133", {"start": v(-2519.57, 1059.64) * mm, "end": v(-2545, 1059.64) * mm});
            skArc(sketch, "E1134", {"start": v(-2545, 1059.64) * mm, "mid": v(-2552.07, 1056.71) * mm, "end": v(-2555, 1049.64) * mm});
            skLineSegment(sketch, "E1135", {"start": v(-2555, 1049.64) * mm, "end": v(-2555, 1019.65) * mm});
            skArc(sketch, "E1136", {"start": v(-2555, 1019.65) * mm, "mid": v(-2552.07, 1012.58) * mm, "end": v(-2545, 1009.65) * mm});
            skLineSegment(sketch, "E1137", {"start": v(-2545, 1009.65) * mm, "end": v(-2534.9, 1009.65) * mm});
            skLineSegment(sketch, "E1138", {"start": v(-2534.9, 1009.65) * mm, "end": v(-2534.9, 1028.99) * mm});
            skArc(sketch, "E1139", {"start": v(-2534.9, 1028.99) * mm, "mid": v(-2534.9, 1034.65) * mm, "end": v(-2529.24, 1034.65) * mm});
            skLineSegment(sketch, "E1140", {"start": v(-2529.24, 1034.65) * mm, "end": v(-2525.36, 1034.65) * mm});
            skArc(sketch, "E1141", {"start": v(-2525.36, 1034.65) * mm, "mid": v(-2519.7, 1034.65) * mm, "end": v(-2519.7, 1028.99) * mm});
            skLineSegment(sketch, "E1142", {"start": v(-2519.7, 1028.99) * mm, "end": v(-2519.7, 1009.65) * mm});
            skLineSegment(sketch, "E1143", {"start": v(-2519.7, 1009.65) * mm, "end": v(-2504.6, 1009.65) * mm});
            skArc(sketch, "E1144", {"start": v(-2504.6, 1009.65) * mm, "mid": v(-2339.6, 992.87) * mm, "end": v(-2174.6, 1009.65) * mm});
            skLineSegment(sketch, "E1145", {"start": v(-2174.6, 1009.65) * mm, "end": v(-2159.5, 1009.65) * mm});
            skLineSegment(sketch, "E1146", {"start": v(-2159.5, 1009.65) * mm, "end": v(-2159.5, 1028.99) * mm});
            skArc(sketch, "E1147", {"start": v(-2159.5, 1028.99) * mm, "mid": v(-2159.5, 1034.65) * mm, "end": v(-2153.84, 1034.65) * mm});
            skLineSegment(sketch, "E1148", {"start": v(-2153.84, 1034.65) * mm, "end": v(-2149.96, 1034.65) * mm});
            skArc(sketch, "E1149", {"start": v(-2149.96, 1034.65) * mm, "mid": v(-2144.3, 1034.65) * mm, "end": v(-2144.3, 1028.99) * mm});
            skLineSegment(sketch, "E1150", {"start": v(-2144.3, 1028.99) * mm, "end": v(-2144.3, 1009.65) * mm});
            skLineSegment(sketch, "E1151", {"start": v(-2144.3, 1009.65) * mm, "end": v(-2134.2, 1009.65) * mm});
            skArc(sketch, "E1152", {"start": v(-2134.2, 1009.65) * mm, "mid": v(-2127.13, 1012.58) * mm, "end": v(-2124.2, 1019.65) * mm});
            skLineSegment(sketch, "E1153", {"start": v(-2124.2, 1019.65) * mm, "end": v(-2124.2, 1049.64) * mm});
            skArc(sketch, "E1154", {"start": v(-2124.2, 1049.64) * mm, "mid": v(-2127.13, 1056.71) * mm, "end": v(-2134.2, 1059.64) * mm});
            skLineSegment(sketch, "E1155", {"start": v(-2134.2, 1059.64) * mm, "end": v(-2159.63, 1059.64) * mm});
            skArc(sketch, "E1156", {"start": v(-2159.63, 994.1) * mm, "mid": v(-2339.6, 974.1) * mm, "end": v(-2519.57, 994.1) * mm});
            skLineSegment(sketch, "E1157", {"start": v(-2519.57, 994.1) * mm, "end": v(-2545, 994.1) * mm});
            skArc(sketch, "E1158", {"start": v(-2545, 994.1) * mm, "mid": v(-2552.07, 991.18) * mm, "end": v(-2555, 984.1) * mm});
            skLineSegment(sketch, "E1159", {"start": v(-2555, 984.1) * mm, "end": v(-2555, 954.11) * mm});
            skArc(sketch, "E1160", {"start": v(-2555, 954.11) * mm, "mid": v(-2552.07, 947.04) * mm, "end": v(-2545, 944.11) * mm});
            skLineSegment(sketch, "E1161", {"start": v(-2545, 944.11) * mm, "end": v(-2534.9, 944.11) * mm});
            skLineSegment(sketch, "E1162", {"start": v(-2534.9, 944.11) * mm, "end": v(-2534.9, 963.46) * mm});
            skArc(sketch, "E1163", {"start": v(-2534.9, 963.46) * mm, "mid": v(-2534.9, 969.11) * mm, "end": v(-2529.24, 969.11) * mm});
            skLineSegment(sketch, "E1164", {"start": v(-2529.24, 969.11) * mm, "end": v(-2525.36, 969.11) * mm});
            skArc(sketch, "E1165", {"start": v(-2525.36, 969.11) * mm, "mid": v(-2519.7, 969.11) * mm, "end": v(-2519.7, 963.46) * mm});
            skLineSegment(sketch, "E1166", {"start": v(-2519.7, 963.46) * mm, "end": v(-2519.7, 944.11) * mm});
            skLineSegment(sketch, "E1167", {"start": v(-2519.7, 944.11) * mm, "end": v(-2504.6, 944.11) * mm});
            skArc(sketch, "E1168", {"start": v(-2504.6, 944.11) * mm, "mid": v(-2339.6, 927.34) * mm, "end": v(-2174.6, 944.11) * mm});
            skLineSegment(sketch, "E1169", {"start": v(-2174.6, 944.11) * mm, "end": v(-2159.5, 944.11) * mm});
            skLineSegment(sketch, "E1170", {"start": v(-2159.5, 944.11) * mm, "end": v(-2159.5, 963.46) * mm});
            skArc(sketch, "E1171", {"start": v(-2159.5, 963.46) * mm, "mid": v(-2159.5, 969.11) * mm, "end": v(-2153.84, 969.11) * mm});
            skLineSegment(sketch, "E1172", {"start": v(-2153.84, 969.11) * mm, "end": v(-2149.96, 969.11) * mm});
            skArc(sketch, "E1173", {"start": v(-2149.96, 969.11) * mm, "mid": v(-2144.3, 969.11) * mm, "end": v(-2144.3, 963.46) * mm});
            skLineSegment(sketch, "E1174", {"start": v(-2144.3, 963.46) * mm, "end": v(-2144.3, 944.11) * mm});
            skLineSegment(sketch, "E1175", {"start": v(-2144.3, 944.11) * mm, "end": v(-2134.2, 944.11) * mm});
            skArc(sketch, "E1176", {"start": v(-2134.2, 944.11) * mm, "mid": v(-2127.13, 947.04) * mm, "end": v(-2124.2, 954.11) * mm});
            skLineSegment(sketch, "E1177", {"start": v(-2124.2, 954.11) * mm, "end": v(-2124.2, 984.1) * mm});
            skArc(sketch, "E1178", {"start": v(-2124.2, 984.1) * mm, "mid": v(-2127.13, 991.18) * mm, "end": v(-2134.2, 994.1) * mm});
            skLineSegment(sketch, "E1179", {"start": v(-2134.2, 994.1) * mm, "end": v(-2159.63, 994.1) * mm});
            skArc(sketch, "E1180", {"start": v(-2159.63, 1125.17) * mm, "mid": v(-2339.6, 1105.17) * mm, "end": v(-2519.57, 1125.17) * mm});
            skLineSegment(sketch, "E1181", {"start": v(-2519.57, 1125.17) * mm, "end": v(-2545, 1125.17) * mm});
            skArc(sketch, "E1182", {"start": v(-2545, 1125.17) * mm, "mid": v(-2552.07, 1122.24) * mm, "end": v(-2555, 1115.17) * mm});
            skLineSegment(sketch, "E1183", {"start": v(-2555, 1115.17) * mm, "end": v(-2555, 1085.18) * mm});
            skArc(sketch, "E1184", {"start": v(-2555, 1085.18) * mm, "mid": v(-2552.07, 1078.1) * mm, "end": v(-2545, 1075.18) * mm});
            skLineSegment(sketch, "E1185", {"start": v(-2545, 1075.18) * mm, "end": v(-2534.9, 1075.18) * mm});
            skLineSegment(sketch, "E1186", {"start": v(-2534.9, 1075.18) * mm, "end": v(-2534.9, 1094.52) * mm});
            skArc(sketch, "E1187", {"start": v(-2534.9, 1094.52) * mm, "mid": v(-2534.9, 1100.18) * mm, "end": v(-2529.24, 1100.18) * mm});
            skLineSegment(sketch, "E1188", {"start": v(-2529.24, 1100.18) * mm, "end": v(-2525.36, 1100.18) * mm});
            skArc(sketch, "E1189", {"start": v(-2525.36, 1100.18) * mm, "mid": v(-2519.7, 1100.18) * mm, "end": v(-2519.7, 1094.52) * mm});
            skLineSegment(sketch, "E1190", {"start": v(-2519.7, 1094.52) * mm, "end": v(-2519.7, 1075.18) * mm});
            skLineSegment(sketch, "E1191", {"start": v(-2519.7, 1075.18) * mm, "end": v(-2504.6, 1075.18) * mm});
            skArc(sketch, "E1192", {"start": v(-2504.6, 1075.18) * mm, "mid": v(-2339.6, 1058.4) * mm, "end": v(-2174.6, 1075.18) * mm});
            skLineSegment(sketch, "E1193", {"start": v(-2174.6, 1075.18) * mm, "end": v(-2159.5, 1075.18) * mm});
            skLineSegment(sketch, "E1194", {"start": v(-2159.5, 1075.18) * mm, "end": v(-2159.5, 1094.52) * mm});
            skArc(sketch, "E1195", {"start": v(-2159.5, 1094.52) * mm, "mid": v(-2159.5, 1100.18) * mm, "end": v(-2153.84, 1100.18) * mm});
            skLineSegment(sketch, "E1196", {"start": v(-2153.84, 1100.18) * mm, "end": v(-2149.96, 1100.18) * mm});
            skArc(sketch, "E1197", {"start": v(-2149.96, 1100.18) * mm, "mid": v(-2144.3, 1100.18) * mm, "end": v(-2144.3, 1094.52) * mm});
            skLineSegment(sketch, "E1198", {"start": v(-2144.3, 1094.52) * mm, "end": v(-2144.3, 1075.18) * mm});
            skLineSegment(sketch, "E1199", {"start": v(-2144.3, 1075.18) * mm, "end": v(-2134.2, 1075.18) * mm});
            skArc(sketch, "E1200", {"start": v(-2134.2, 1075.18) * mm, "mid": v(-2127.13, 1078.1) * mm, "end": v(-2124.2, 1085.18) * mm});
            skLineSegment(sketch, "E1201", {"start": v(-2124.2, 1085.18) * mm, "end": v(-2124.2, 1115.17) * mm});
            skArc(sketch, "E1202", {"start": v(-2124.2, 1115.17) * mm, "mid": v(-2127.13, 1122.24) * mm, "end": v(-2134.2, 1125.17) * mm});
            skLineSegment(sketch, "E1203", {"start": v(-2134.2, 1125.17) * mm, "end": v(-2159.63, 1125.17) * mm});
            skArc(sketch, "E1204", {"start": v(-2159.63, 1190.7) * mm, "mid": v(-2339.6, 1170.7) * mm, "end": v(-2519.57, 1190.7) * mm});
            skLineSegment(sketch, "E1205", {"start": v(-2519.57, 1190.7) * mm, "end": v(-2545, 1190.7) * mm});
            skArc(sketch, "E1206", {"start": v(-2545, 1190.7) * mm, "mid": v(-2552.07, 1187.77) * mm, "end": v(-2555, 1180.7) * mm});
            skLineSegment(sketch, "E1207", {"start": v(-2555, 1180.7) * mm, "end": v(-2555, 1150.7) * mm});
            skArc(sketch, "E1208", {"start": v(-2555, 1150.7) * mm, "mid": v(-2552.07, 1143.64) * mm, "end": v(-2545, 1140.7) * mm});
            skLineSegment(sketch, "E1209", {"start": v(-2545, 1140.7) * mm, "end": v(-2534.9, 1140.7) * mm});
            skLineSegment(sketch, "E1210", {"start": v(-2534.9, 1140.7) * mm, "end": v(-2534.9, 1160.05) * mm});
            skArc(sketch, "E1211", {"start": v(-2534.9, 1160.05) * mm, "mid": v(-2534.9, 1165.7) * mm, "end": v(-2529.24, 1165.7) * mm});
            skLineSegment(sketch, "E1212", {"start": v(-2529.24, 1165.7) * mm, "end": v(-2525.36, 1165.7) * mm});
            skArc(sketch, "E1213", {"start": v(-2525.36, 1165.7) * mm, "mid": v(-2519.7, 1165.7) * mm, "end": v(-2519.7, 1160.05) * mm});
            skLineSegment(sketch, "E1214", {"start": v(-2519.7, 1160.05) * mm, "end": v(-2519.7, 1140.7) * mm});
            skLineSegment(sketch, "E1215", {"start": v(-2519.7, 1140.7) * mm, "end": v(-2504.6, 1140.7) * mm});
            skArc(sketch, "E1216", {"start": v(-2504.6, 1140.7) * mm, "mid": v(-2339.6, 1123.93) * mm, "end": v(-2174.6, 1140.7) * mm});
            skLineSegment(sketch, "E1217", {"start": v(-2174.6, 1140.7) * mm, "end": v(-2159.5, 1140.7) * mm});
            skLineSegment(sketch, "E1218", {"start": v(-2159.5, 1140.7) * mm, "end": v(-2159.5, 1160.05) * mm});
            skArc(sketch, "E1219", {"start": v(-2159.5, 1160.05) * mm, "mid": v(-2159.5, 1165.7) * mm, "end": v(-2153.84, 1165.7) * mm});
            skLineSegment(sketch, "E1220", {"start": v(-2153.84, 1165.7) * mm, "end": v(-2149.96, 1165.7) * mm});
            skArc(sketch, "E1221", {"start": v(-2149.96, 1165.7) * mm, "mid": v(-2144.3, 1165.7) * mm, "end": v(-2144.3, 1160.05) * mm});
            skLineSegment(sketch, "E1222", {"start": v(-2144.3, 1160.05) * mm, "end": v(-2144.3, 1140.7) * mm});
            skLineSegment(sketch, "E1223", {"start": v(-2144.3, 1140.7) * mm, "end": v(-2134.2, 1140.7) * mm});
            skArc(sketch, "E1224", {"start": v(-2134.2, 1140.7) * mm, "mid": v(-2127.13, 1143.64) * mm, "end": v(-2124.2, 1150.7) * mm});
            skLineSegment(sketch, "E1225", {"start": v(-2124.2, 1150.7) * mm, "end": v(-2124.2, 1180.7) * mm});
            skArc(sketch, "E1226", {"start": v(-2124.2, 1180.7) * mm, "mid": v(-2127.13, 1187.77) * mm, "end": v(-2134.2, 1190.7) * mm});
            skLineSegment(sketch, "E1227", {"start": v(-2134.2, 1190.7) * mm, "end": v(-2159.63, 1190.7) * mm});
            skArc(sketch, "E1228", {"start": v(-1385, 639.55) * mm, "mid": v(-1405, 819.52) * mm, "end": v(-1385, 999.48) * mm});
            skLineSegment(sketch, "E1229", {"start": v(-1385, 999.48) * mm, "end": v(-1385, 1024.92) * mm});
            skArc(sketch, "E1230", {"start": v(-1385, 1024.92) * mm, "mid": v(-1387.93, 1031.99) * mm, "end": v(-1395, 1034.92) * mm});
            skLineSegment(sketch, "E1231", {"start": v(-1395, 1034.92) * mm, "end": v(-1425, 1034.92) * mm});
            skArc(sketch, "E1232", {"start": v(-1425, 1034.92) * mm, "mid": v(-1432.06, 1031.99) * mm, "end": v(-1435, 1024.92) * mm});
            skLineSegment(sketch, "E1233", {"start": v(-1435, 1024.92) * mm, "end": v(-1435, 1014.82) * mm});
            skLineSegment(sketch, "E1234", {"start": v(-1435, 1014.82) * mm, "end": v(-1415.65, 1014.82) * mm});
            skArc(sketch, "E1235", {"start": v(-1415.65, 1014.82) * mm, "mid": v(-1410, 1014.82) * mm, "end": v(-1410, 1009.16) * mm});
            skLineSegment(sketch, "E1236", {"start": v(-1410, 1009.16) * mm, "end": v(-1410, 1005.27) * mm});
            skArc(sketch, "E1237", {"start": v(-1410, 1005.27) * mm, "mid": v(-1410, 999.62) * mm, "end": v(-1415.65, 999.62) * mm});
            skLineSegment(sketch, "E1238", {"start": v(-1415.65, 999.62) * mm, "end": v(-1435, 999.62) * mm});
            skLineSegment(sketch, "E1239", {"start": v(-1435, 999.62) * mm, "end": v(-1435, 984.52) * mm});
            skArc(sketch, "E1240", {"start": v(-1435, 984.52) * mm, "mid": v(-1451.77, 819.52) * mm, "end": v(-1435, 654.52) * mm});
            skLineSegment(sketch, "E1241", {"start": v(-1435, 654.52) * mm, "end": v(-1435, 639.42) * mm});
            skLineSegment(sketch, "E1242", {"start": v(-1435, 639.42) * mm, "end": v(-1415.65, 639.42) * mm});
            skArc(sketch, "E1243", {"start": v(-1415.65, 639.42) * mm, "mid": v(-1410, 639.42) * mm, "end": v(-1410, 633.76) * mm});
            skLineSegment(sketch, "E1244", {"start": v(-1410, 633.76) * mm, "end": v(-1410, 629.87) * mm});
            skArc(sketch, "E1245", {"start": v(-1410, 629.87) * mm, "mid": v(-1410, 624.22) * mm, "end": v(-1415.65, 624.22) * mm});
            skLineSegment(sketch, "E1246", {"start": v(-1415.65, 624.22) * mm, "end": v(-1435, 624.22) * mm});
            skLineSegment(sketch, "E1247", {"start": v(-1435, 624.22) * mm, "end": v(-1435, 614.12) * mm});
            skArc(sketch, "E1248", {"start": v(-1435, 614.12) * mm, "mid": v(-1432.06, 607.04) * mm, "end": v(-1425, 604.12) * mm});
            skLineSegment(sketch, "E1249", {"start": v(-1425, 604.12) * mm, "end": v(-1395, 604.12) * mm});
            skArc(sketch, "E1250", {"start": v(-1395, 604.12) * mm, "mid": v(-1387.93, 607.04) * mm, "end": v(-1385, 614.12) * mm});
            skLineSegment(sketch, "E1251", {"start": v(-1385, 614.12) * mm, "end": v(-1385, 639.55) * mm});
            skLineSegment(sketch, "E1252", {"start": v(-2353.4, 1329.85) * mm, "end": v(-2348.38, 1348.54) * mm});
            skArc(sketch, "E1253", {"start": v(-2348.38, 1348.54) * mm, "mid": v(-2346.92, 1354) * mm, "end": v(-2341.46, 1352.54) * mm});
            skLineSegment(sketch, "E1254", {"start": v(-2341.46, 1352.54) * mm, "end": v(-2337.7, 1351.53) * mm});
            skArc(sketch, "E1255", {"start": v(-2337.7, 1351.53) * mm, "mid": v(-2332.24, 1350.07) * mm, "end": v(-2333.7, 1344.6) * mm});
            skLineSegment(sketch, "E1256", {"start": v(-2333.7, 1344.6) * mm, "end": v(-2338.7, 1325.92) * mm});
            skLineSegment(sketch, "E1257", {"start": v(-2338.7, 1325.92) * mm, "end": v(-2319.58, 1320.8) * mm});
            skLineSegment(sketch, "E1258", {"start": v(-2319.58, 1320.8) * mm, "end": v(-2314.58, 1339.48) * mm});
            skArc(sketch, "E1259", {"start": v(-2314.58, 1339.48) * mm, "mid": v(-2313.11, 1344.94) * mm, "end": v(-2307.65, 1343.48) * mm});
            skLineSegment(sketch, "E1260", {"start": v(-2307.65, 1343.48) * mm, "end": v(-2303.9, 1342.47) * mm});
            skArc(sketch, "E1261", {"start": v(-2303.9, 1342.47) * mm, "mid": v(-2298.43, 1341) * mm, "end": v(-2299.9, 1335.54) * mm});
            skLineSegment(sketch, "E1262", {"start": v(-2299.9, 1335.54) * mm, "end": v(-2304.9, 1316.86) * mm});
            skLineSegment(sketch, "E1263", {"start": v(-2304.9, 1316.86) * mm, "end": v(-2285.78, 1311.74) * mm});
            skLineSegment(sketch, "E1264", {"start": v(-2285.78, 1311.74) * mm, "end": v(-2280.77, 1330.42) * mm});
            skArc(sketch, "E1265", {"start": v(-2280.77, 1330.42) * mm, "mid": v(-2279.3, 1335.88) * mm, "end": v(-2273.84, 1334.42) * mm});
            skLineSegment(sketch, "E1266", {"start": v(-2273.84, 1334.42) * mm, "end": v(-2270.09, 1333.41) * mm});
            skArc(sketch, "E1267", {"start": v(-2270.09, 1333.41) * mm, "mid": v(-2264.62, 1331.95) * mm, "end": v(-2266.09, 1326.49) * mm});
            skLineSegment(sketch, "E1268", {"start": v(-2266.09, 1326.49) * mm, "end": v(-2271.1, 1307.8) * mm});
            skLineSegment(sketch, "E1269", {"start": v(-2271.1, 1307.8) * mm, "end": v(-2251.97, 1302.68) * mm});
            skLineSegment(sketch, "E1270", {"start": v(-2251.97, 1302.68) * mm, "end": v(-2246.96, 1321.36) * mm});
            skArc(sketch, "E1271", {"start": v(-2246.96, 1321.36) * mm, "mid": v(-2245.5, 1326.82) * mm, "end": v(-2240.03, 1325.36) * mm});
            skLineSegment(sketch, "E1272", {"start": v(-2240.03, 1325.36) * mm, "end": v(-2236.28, 1324.35) * mm});
            skArc(sketch, "E1273", {"start": v(-2236.28, 1324.35) * mm, "mid": v(-2230.82, 1322.9) * mm, "end": v(-2232.28, 1317.43) * mm});
            skLineSegment(sketch, "E1274", {"start": v(-2232.28, 1317.43) * mm, "end": v(-2237.29, 1298.74) * mm});
            skLineSegment(sketch, "E1275", {"start": v(-2237.29, 1298.74) * mm, "end": v(-2218.16, 1293.62) * mm});
            skLineSegment(sketch, "E1276", {"start": v(-2218.16, 1293.62) * mm, "end": v(-2213.15, 1312.3) * mm});
            skArc(sketch, "E1277", {"start": v(-2213.15, 1312.3) * mm, "mid": v(-2211.7, 1317.77) * mm, "end": v(-2206.23, 1316.3) * mm});
            skLineSegment(sketch, "E1278", {"start": v(-2206.23, 1316.3) * mm, "end": v(-2202.47, 1315.3) * mm});
            skArc(sketch, "E1279", {"start": v(-2202.47, 1315.3) * mm, "mid": v(-2197, 1313.83) * mm, "end": v(-2198.47, 1308.37) * mm});
            skLineSegment(sketch, "E1280", {"start": v(-2198.47, 1308.37) * mm, "end": v(-2203.48, 1289.68) * mm});
            skLineSegment(sketch, "E1281", {"start": v(-2203.48, 1289.68) * mm, "end": v(-2182.14, 1283.97) * mm});
            skArc(sketch, "E1282", {"start": v(-2182.14, 1283.97) * mm, "mid": v(-2171.56, 1282.32) * mm, "end": v(-2160.87, 1282.96) * mm});
            skLineSegment(sketch, "E1283", {"start": v(-2160.87, 1282.96) * mm, "end": v(-2055.99, 1300.05) * mm});
            skArc(sketch, "E1284", {"start": v(-2055.99, 1300.05) * mm, "mid": v(-2031.45, 1293.05) * mm, "end": v(-2021.17, 1269.69) * mm});
            skLineSegment(sketch, "E1285", {"start": v(-2021.17, 1269.69) * mm, "end": v(-2021.94, 1239.01) * mm});
            skLineSegment(sketch, "E1286", {"start": v(-2021.94, 1239.01) * mm, "end": v(-2002.6, 1238.53) * mm});
            skArc(sketch, "E1287", {"start": v(-2002.6, 1238.53) * mm, "mid": v(-1996.95, 1238.39) * mm, "end": v(-1997.09, 1232.73) * mm});
            skLineSegment(sketch, "E1288", {"start": v(-1997.09, 1232.73) * mm, "end": v(-1997.18, 1228.85) * mm});
            skArc(sketch, "E1289", {"start": v(-1997.18, 1228.85) * mm, "mid": v(-1997.33, 1223.2) * mm, "end": v(-2002.98, 1223.33) * mm});
            skLineSegment(sketch, "E1290", {"start": v(-2002.98, 1223.33) * mm, "end": v(-2022.32, 1223.82) * mm});
            skLineSegment(sketch, "E1291", {"start": v(-2022.32, 1223.82) * mm, "end": v(-2022.81, 1204.02) * mm});
            skLineSegment(sketch, "E1292", {"start": v(-2022.81, 1204.02) * mm, "end": v(-2003.47, 1203.54) * mm});
            skArc(sketch, "E1293", {"start": v(-2003.47, 1203.54) * mm, "mid": v(-1997.82, 1203.4) * mm, "end": v(-1997.96, 1197.74) * mm});
            skLineSegment(sketch, "E1294", {"start": v(-1997.96, 1197.74) * mm, "end": v(-1998.06, 1193.86) * mm});
            skArc(sketch, "E1295", {"start": v(-1998.06, 1193.86) * mm, "mid": v(-1998.2, 1188.2) * mm, "end": v(-2003.85, 1188.34) * mm});
            skLineSegment(sketch, "E1296", {"start": v(-2003.85, 1188.34) * mm, "end": v(-2023.19, 1188.83) * mm});
            skLineSegment(sketch, "E1297", {"start": v(-2023.19, 1188.83) * mm, "end": v(-2023.68, 1169.03) * mm});
            skLineSegment(sketch, "E1298", {"start": v(-2023.68, 1169.03) * mm, "end": v(-2004.35, 1168.55) * mm});
            skArc(sketch, "E1299", {"start": v(-2004.35, 1168.55) * mm, "mid": v(-1998.7, 1168.4) * mm, "end": v(-1998.83, 1162.75) * mm});
            skLineSegment(sketch, "E1300", {"start": v(-1998.83, 1162.75) * mm, "end": v(-1998.93, 1158.87) * mm});
            skArc(sketch, "E1301", {"start": v(-1998.93, 1158.87) * mm, "mid": v(-1999.07, 1153.21) * mm, "end": v(-2004.72, 1153.35) * mm});
            skLineSegment(sketch, "E1302", {"start": v(-2004.72, 1153.35) * mm, "end": v(-2024.06, 1153.84) * mm});
            skLineSegment(sketch, "E1303", {"start": v(-2024.06, 1153.84) * mm, "end": v(-2024.56, 1134.04) * mm});
            skLineSegment(sketch, "E1304", {"start": v(-2024.56, 1134.04) * mm, "end": v(-2005.22, 1133.56) * mm});
            skArc(sketch, "E1305", {"start": v(-2005.22, 1133.56) * mm, "mid": v(-1999.56, 1133.42) * mm, "end": v(-1999.7, 1127.76) * mm});
            skLineSegment(sketch, "E1306", {"start": v(-1999.7, 1127.76) * mm, "end": v(-1999.8, 1123.88) * mm});
            skArc(sketch, "E1307", {"start": v(-1999.8, 1123.88) * mm, "mid": v(-1999.94, 1118.22) * mm, "end": v(-2005.6, 1118.37) * mm});
            skLineSegment(sketch, "E1308", {"start": v(-2005.6, 1118.37) * mm, "end": v(-2024.93, 1118.85) * mm});
            skLineSegment(sketch, "E1309", {"start": v(-2024.93, 1118.85) * mm, "end": v(-2025.43, 1099.05) * mm});
            skLineSegment(sketch, "E1310", {"start": v(-2025.43, 1099.05) * mm, "end": v(-2006.1, 1098.57) * mm});
            skArc(sketch, "E1311", {"start": v(-2006.1, 1098.57) * mm, "mid": v(-2000.44, 1098.43) * mm, "end": v(-2000.58, 1092.78) * mm});
            skLineSegment(sketch, "E1312", {"start": v(-2000.58, 1092.78) * mm, "end": v(-2000.67, 1088.9) * mm});
            skArc(sketch, "E1313", {"start": v(-2000.67, 1088.9) * mm, "mid": v(-2000.81, 1083.24) * mm, "end": v(-2006.47, 1083.38) * mm});
            skLineSegment(sketch, "E1314", {"start": v(-2006.47, 1083.38) * mm, "end": v(-2025.8, 1083.86) * mm});
            skLineSegment(sketch, "E1315", {"start": v(-2025.8, 1083.86) * mm, "end": v(-2026.3, 1064.06) * mm});
            skLineSegment(sketch, "E1316", {"start": v(-2026.3, 1064.06) * mm, "end": v(-2006.96, 1063.58) * mm});
            skArc(sketch, "E1317", {"start": v(-2006.96, 1063.58) * mm, "mid": v(-2001.3, 1063.44) * mm, "end": v(-2001.45, 1057.79) * mm});
            skLineSegment(sketch, "E1318", {"start": v(-2001.45, 1057.79) * mm, "end": v(-2001.55, 1053.9) * mm});
            skArc(sketch, "E1319", {"start": v(-2001.55, 1053.9) * mm, "mid": v(-2001.69, 1048.25) * mm, "end": v(-2007.34, 1048.39) * mm});
            skLineSegment(sketch, "E1320", {"start": v(-2007.34, 1048.39) * mm, "end": v(-2026.68, 1048.87) * mm});
            skLineSegment(sketch, "E1321", {"start": v(-2026.68, 1048.87) * mm, "end": v(-2027.17, 1029.08) * mm});
            skLineSegment(sketch, "E1322", {"start": v(-2027.17, 1029.08) * mm, "end": v(-2007.83, 1028.6) * mm});
            skArc(sketch, "E1323", {"start": v(-2007.83, 1028.6) * mm, "mid": v(-2002.18, 1028.45) * mm, "end": v(-2002.32, 1022.8) * mm});
            skLineSegment(sketch, "E1324", {"start": v(-2002.32, 1022.8) * mm, "end": v(-2002.42, 1018.91) * mm});
            skArc(sketch, "E1325", {"start": v(-2002.42, 1018.91) * mm, "mid": v(-2002.56, 1013.26) * mm, "end": v(-2008.21, 1013.4) * mm});
            skLineSegment(sketch, "E1326", {"start": v(-2008.21, 1013.4) * mm, "end": v(-2027.55, 1013.88) * mm});
            skLineSegment(sketch, "E1327", {"start": v(-2027.55, 1013.88) * mm, "end": v(-2028.04, 994.09) * mm});
            skLineSegment(sketch, "E1328", {"start": v(-2028.04, 994.09) * mm, "end": v(-2008.7, 993.6) * mm});
            skArc(sketch, "E1329", {"start": v(-2008.7, 993.6) * mm, "mid": v(-2003.05, 993.46) * mm, "end": v(-2003.2, 987.8) * mm});
            skLineSegment(sketch, "E1330", {"start": v(-2003.2, 987.8) * mm, "end": v(-2003.29, 983.92) * mm});
            skArc(sketch, "E1331", {"start": v(-2003.29, 983.92) * mm, "mid": v(-2003.43, 978.27) * mm, "end": v(-2009.09, 978.4) * mm});
            skLineSegment(sketch, "E1332", {"start": v(-2009.09, 978.4) * mm, "end": v(-2028.42, 978.9) * mm});
            skLineSegment(sketch, "E1333", {"start": v(-2028.42, 978.9) * mm, "end": v(-2028.92, 959.1) * mm});
            skLineSegment(sketch, "E1334", {"start": v(-2028.92, 959.1) * mm, "end": v(-2009.58, 958.62) * mm});
            skArc(sketch, "E1335", {"start": v(-2009.58, 958.62) * mm, "mid": v(-2003.92, 958.47) * mm, "end": v(-2004.06, 952.82) * mm});
            skLineSegment(sketch, "E1336", {"start": v(-2004.06, 952.82) * mm, "end": v(-2004.16, 948.93) * mm});
            skArc(sketch, "E1337", {"start": v(-2004.16, 948.93) * mm, "mid": v(-2004.3, 943.28) * mm, "end": v(-2009.96, 943.42) * mm});
            skLineSegment(sketch, "E1338", {"start": v(-2009.96, 943.42) * mm, "end": v(-2029.3, 943.9) * mm});
            skLineSegment(sketch, "E1339", {"start": v(-2029.3, 943.9) * mm, "end": v(-2029.79, 924.1) * mm});
            skLineSegment(sketch, "E1340", {"start": v(-2029.79, 924.1) * mm, "end": v(-2010.45, 923.63) * mm});
            skArc(sketch, "E1341", {"start": v(-2010.45, 923.63) * mm, "mid": v(-2004.8, 923.49) * mm, "end": v(-2004.94, 917.83) * mm});
            skLineSegment(sketch, "E1342", {"start": v(-2004.94, 917.83) * mm, "end": v(-2005.03, 913.95) * mm});
            skArc(sketch, "E1343", {"start": v(-2005.03, 913.95) * mm, "mid": v(-2005.17, 908.29) * mm, "end": v(-2010.83, 908.43) * mm});
            skLineSegment(sketch, "E1344", {"start": v(-2010.83, 908.43) * mm, "end": v(-2030.17, 908.91) * mm});
            skLineSegment(sketch, "E1345", {"start": v(-2030.17, 908.91) * mm, "end": v(-2030.66, 889.14) * mm});
            skLineSegment(sketch, "E1346", {"start": v(-2030.66, 889.14) * mm, "end": v(-1806.03, 868.89) * mm});
            skArc(sketch, "E1347", {"start": v(-1806.03, 868.89) * mm, "mid": v(-1800.4, 868.38) * mm, "end": v(-1800.9, 862.74) * mm});
            skLineSegment(sketch, "E1348", {"start": v(-1800.9, 862.74) * mm, "end": v(-1801.25, 858.87) * mm});
            skArc(sketch, "E1349", {"start": v(-1801.25, 858.87) * mm, "mid": v(-1801.76, 853.24) * mm, "end": v(-1807.4, 853.75) * mm});
            skLineSegment(sketch, "E1350", {"start": v(-1807.4, 853.75) * mm, "end": v(-2031.04, 873.9) * mm});
            skLineSegment(sketch, "E1351", {"start": v(-2031.04, 873.9) * mm, "end": v(-2031.04, 873.8) * mm});
            skArc(sketch, "E1352", {"start": v(-2031.04, 873.8) * mm, "mid": v(-2023.37, 853.23) * mm, "end": v(-2003.74, 843.4) * mm});
            skLineSegment(sketch, "E1353", {"start": v(-2003.74, 843.4) * mm, "end": v(-1571.12, 804.4) * mm});
            skLineSegment(sketch, "E1354", {"start": v(-1571.12, 804.4) * mm, "end": v(-1571.12, 867.67) * mm});
            skLineSegment(sketch, "E1355", {"start": v(-1571.12, 867.67) * mm, "end": v(-1952.26, 902.03) * mm});
            skArc(sketch, "E1356", {"start": v(-1952.26, 902.03) * mm, "mid": v(-1971.96, 911.95) * mm, "end": v(-1979.56, 932.66) * mm});
            skLineSegment(sketch, "E1357", {"start": v(-1979.56, 932.66) * mm, "end": v(-1971.06, 1273.77) * mm});
            skArc(sketch, "E1358", {"start": v(-1971.06, 1273.77) * mm, "mid": v(-1965.2, 1290.84) * mm, "end": v(-1950.63, 1301.46) * mm});
            skLineSegment(sketch, "E1359", {"start": v(-1950.63, 1301.46) * mm, "end": v(-1571.12, 1423.38) * mm});
            skLineSegment(sketch, "E1360", {"start": v(-1571.12, 1423.38) * mm, "end": v(-1571.12, 1473.38) * mm});
            skLineSegment(sketch, "E1361", {"start": v(-1571.12, 1473.38) * mm, "end": v(-1721.02, 1438.07) * mm});
            skLineSegment(sketch, "E1362", {"start": v(-1721.02, 1438.07) * mm, "end": v(-1716.58, 1419.24) * mm});
            skArc(sketch, "E1363", {"start": v(-1716.58, 1419.24) * mm, "mid": v(-1715.29, 1413.73) * mm, "end": v(-1720.8, 1412.44) * mm});
            skLineSegment(sketch, "E1364", {"start": v(-1720.8, 1412.44) * mm, "end": v(-1724.58, 1411.54) * mm});
            skArc(sketch, "E1365", {"start": v(-1724.58, 1411.54) * mm, "mid": v(-1730.08, 1410.25) * mm, "end": v(-1731.38, 1415.75) * mm});
            skLineSegment(sketch, "E1366", {"start": v(-1731.38, 1415.75) * mm, "end": v(-1735.82, 1434.58) * mm});
            skLineSegment(sketch, "E1367", {"start": v(-1735.82, 1434.58) * mm, "end": v(-2157.4, 1335.27) * mm});
            skArc(sketch, "E1368", {"start": v(-2157.4, 1335.27) * mm, "mid": v(-2169.62, 1333.94) * mm, "end": v(-2181.8, 1335.64) * mm});
            skLineSegment(sketch, "E1369", {"start": v(-2181.8, 1335.64) * mm, "end": v(-2388.65, 1391.06) * mm});
            skArc(sketch, "E1370", {"start": v(-2388.65, 1391.06) * mm, "mid": v(-2396.24, 1390.06) * mm, "end": v(-2400.9, 1384) * mm});
            skLineSegment(sketch, "E1371", {"start": v(-2400.9, 1384) * mm, "end": v(-2408.66, 1355.02) * mm});
            skArc(sketch, "E1372", {"start": v(-2408.66, 1355.02) * mm, "mid": v(-2407.66, 1347.43) * mm, "end": v(-2401.6, 1342.77) * mm});
            skLineSegment(sketch, "E1373", {"start": v(-2401.6, 1342.77) * mm, "end": v(-2387.2, 1338.91) * mm});
            skLineSegment(sketch, "E1374", {"start": v(-2387.2, 1338.91) * mm, "end": v(-2382.2, 1357.6) * mm});
            skArc(sketch, "E1375", {"start": v(-2382.2, 1357.6) * mm, "mid": v(-2380.73, 1363.06) * mm, "end": v(-2375.26, 1361.6) * mm});
            skLineSegment(sketch, "E1376", {"start": v(-2375.26, 1361.6) * mm, "end": v(-2371.5, 1360.59) * mm});
            skArc(sketch, "E1377", {"start": v(-2371.5, 1360.59) * mm, "mid": v(-2366.05, 1359.13) * mm, "end": v(-2367.5, 1353.66) * mm});
            skLineSegment(sketch, "E1378", {"start": v(-2367.5, 1353.66) * mm, "end": v(-2372.52, 1334.98) * mm});
            skLineSegment(sketch, "E1379", {"start": v(-2372.52, 1334.98) * mm, "end": v(-2353.49, 1329.88) * mm});
            skSolve(sketch);
        }
        {
            var Q0;
            Q0=makeQuery(id+"F0.imprint","IMPRINT",FACE,{"disambiguationData":[TD([[makeQuery(id+"F0.imprint","IMPRINT",EDGE,{"derivedFrom":sQuery(id+"F0.wireOp",EDGE,"E4")}),-1.0]])]});
            var sketch = newSketch(context, id + "F1", { "sketchPlane" : qUnion([Q0])});
            skPoint(sketch, "E1380.0", {"position": v(-2555, 1180.7) * mm});
            skPoint(sketch, "E1381.0", {"position": v(-2545, 1180.7) * mm});
            skPoint(sketch, "E1382.0", {"position": v(-2545, 1190.7) * mm});
            skPoint(sketch, "E1383.0", {"position": v(-2545, 1150.7) * mm});
            skPoint(sketch, "E1384.0", {"position": v(-2545, 1140.7) * mm});
            skPoint(sketch, "E1385.0", {"position": v(-2555, 1150.7) * mm});
            skPoint(sketch, "E1386.0", {"position": v(-2534.9, 1160.05) * mm});
            skPoint(sketch, "E1387.0", {"position": v(-2529.24, 1165.7) * mm});
            skPoint(sketch, "E1388.0", {"position": v(-2532.07, 1162.88) * mm});
            skPoint(sketch, "E1389.0", {"position": v(-2534.9, 1140.7) * mm});
            skPoint(sketch, "E1390.0", {"position": v(-2519.57, 1190.7) * mm});
            skPoint(sketch, "E1391.0", {"position": v(-2525.36, 1165.7) * mm});
            skPoint(sketch, "E1392.0", {"position": v(-2522.53, 1162.88) * mm});
            skPoint(sketch, "E1393.0", {"position": v(-2519.7, 1160.05) * mm});
            skPoint(sketch, "E1394.0", {"position": v(-2519.7, 1140.7) * mm});
            skPoint(sketch, "E1395.0", {"position": v(-2504.6, 1140.7) * mm});
            skPoint(sketch, "E1396.0", {"position": v(-2159.63, 1190.7) * mm});
            skPoint(sketch, "E1397.0", {"position": v(-2174.6, 1140.7) * mm});
            skPoint(sketch, "E1398.0", {"position": v(-2159.5, 1160.05) * mm});
            skPoint(sketch, "E1399.0", {"position": v(-2159.5, 1140.7) * mm});
            skPoint(sketch, "E1400.0", {"position": v(-2156.67, 1162.88) * mm});
            skPoint(sketch, "E1401.0", {"position": v(-2153.84, 1165.7) * mm});
            skPoint(sketch, "E1402.0", {"position": v(-2149.96, 1165.7) * mm});
            skPoint(sketch, "E1403.0", {"position": v(-2147.13, 1162.88) * mm});
            skPoint(sketch, "E1404.0", {"position": v(-2144.3, 1160.05) * mm});
            skPoint(sketch, "E1405.0", {"position": v(-2144.3, 1140.7) * mm});
            skPoint(sketch, "E1406.0", {"position": v(-2134.2, 1140.7) * mm});
            skPoint(sketch, "E1407.0", {"position": v(-2134.2, 1150.7) * mm});
            skPoint(sketch, "E1408.0", {"position": v(-2124.2, 1150.7) * mm});
            skPoint(sketch, "E1409.0", {"position": v(-2124.2, 1180.7) * mm});
            skPoint(sketch, "E1410.0", {"position": v(-2134.2, 1180.7) * mm});
            skPoint(sketch, "E1411.0", {"position": v(-2134.2, 1190.7) * mm});
            skLineSegment(sketch, "E1412", {"start": v(-2555, 1180.7) * mm, "end": v(-2555, 1150.7) * mm});
            skLineSegment(sketch, "E1413", {"start": v(-2545, 1190.7) * mm, "end": v(-2519.57, 1190.7) * mm});
            skLineSegment(sketch, "E1414", {"start": v(-2519.7, 1140.7) * mm, "end": v(-2519.7, 1160.05) * mm});
            skLineSegment(sketch, "E1415", {"start": v(-2504.6, 1140.7) * mm, "end": v(-2519.7, 1140.7) * mm});
            skLineSegment(sketch, "E1416", {"start": v(-2534.9, 1140.7) * mm, "end": v(-2545, 1140.7) * mm});
            skLineSegment(sketch, "E1417", {"start": v(-2534.9, 1160.05) * mm, "end": v(-2534.9, 1140.7) * mm});
            skLineSegment(sketch, "E1418", {"start": v(-2529.24, 1165.7) * mm, "end": v(-2525.36, 1165.7) * mm});
            skLineSegment(sketch, "E1419", {"start": v(-2149.96, 1165.7) * mm, "end": v(-2153.84, 1165.7) * mm});
            skLineSegment(sketch, "E1420", {"start": v(-2159.5, 1160.05) * mm, "end": v(-2159.5, 1140.7) * mm});
            skLineSegment(sketch, "E1421", {"start": v(-2174.6, 1140.7) * mm, "end": v(-2159.5, 1140.7) * mm});
            skLineSegment(sketch, "E1422", {"start": v(-2144.3, 1140.7) * mm, "end": v(-2134.2, 1140.7) * mm});
            skLineSegment(sketch, "E1423", {"start": v(-2144.3, 1140.7) * mm, "end": v(-2144.3, 1160.05) * mm});
            skLineSegment(sketch, "E1424", {"start": v(-2134.2, 1190.7) * mm, "end": v(-2159.63, 1190.7) * mm});
            skPoint(sketch, "E1425.0", {"position": v(-2339.6, 1170.7) * mm});
            skPoint(sketch, "E1426.0", {"position": v(-2339.6, 1123.93) * mm});
            skArc(sketch, "E1427", {"start": v(-2545, 1190.7) * mm, "mid": v(-2552.07, 1187.77) * mm, "end": v(-2555, 1180.7) * mm});
            skArc(sketch, "E1428", {"start": v(-2555, 1150.7) * mm, "mid": v(-2552.07, 1143.64) * mm, "end": v(-2545, 1140.7) * mm});
            skArc(sketch, "E1429", {"start": v(-2529.24, 1165.7) * mm, "mid": v(-2534.9, 1165.7) * mm, "end": v(-2534.9, 1160.05) * mm});
            skArc(sketch, "E1430", {"start": v(-2519.7, 1160.05) * mm, "mid": v(-2519.7, 1165.7) * mm, "end": v(-2525.36, 1165.7) * mm});
            skArc(sketch, "E1431", {"start": v(-2124.2, 1180.7) * mm, "mid": v(-2127.13, 1187.77) * mm, "end": v(-2134.2, 1190.7) * mm});
            skArc(sketch, "E1432", {"start": v(-2134.2, 1140.7) * mm, "mid": v(-2127.13, 1143.64) * mm, "end": v(-2124.2, 1150.7) * mm});
            skArc(sketch, "E1433", {"start": v(-2153.84, 1165.7) * mm, "mid": v(-2159.5, 1165.7) * mm, "end": v(-2159.5, 1160.05) * mm});
            skArc(sketch, "E1434", {"start": v(-2144.3, 1160.05) * mm, "mid": v(-2144.3, 1165.7) * mm, "end": v(-2149.96, 1165.7) * mm});
            skArc(sketch, "E1435", {"start": v(-2504.6, 1140.7) * mm, "mid": v(-2339.6, 1123.93) * mm, "end": v(-2174.6, 1140.7) * mm});
            skArc(sketch, "E1436", {"start": v(-2519.57, 1190.7) * mm, "mid": v(-2339.6, 1170.7) * mm, "end": v(-2159.63, 1190.7) * mm});
            skLineSegment(sketch, "E1437", {"start": v(-2124.2, 1180.7) * mm, "end": v(-2124.2, 1150.7) * mm});
            skSolve(sketch);
        }
        {
            var Q0;
            Q0=makeQuery(id+"F1.imprint","IMPRINT",FACE,{"disambiguationData":[TD([[makeQuery(id+"F1.imprint","IMPRINT",EDGE,{"derivedFrom":sQuery(id+"F1.wireOp",EDGE,"E1412")}),1.0]])]});
            extrude(context, id + "F2", {"entities" : qUnion([Q0]), "depth" : 15.2 * mm});
        }
    });
